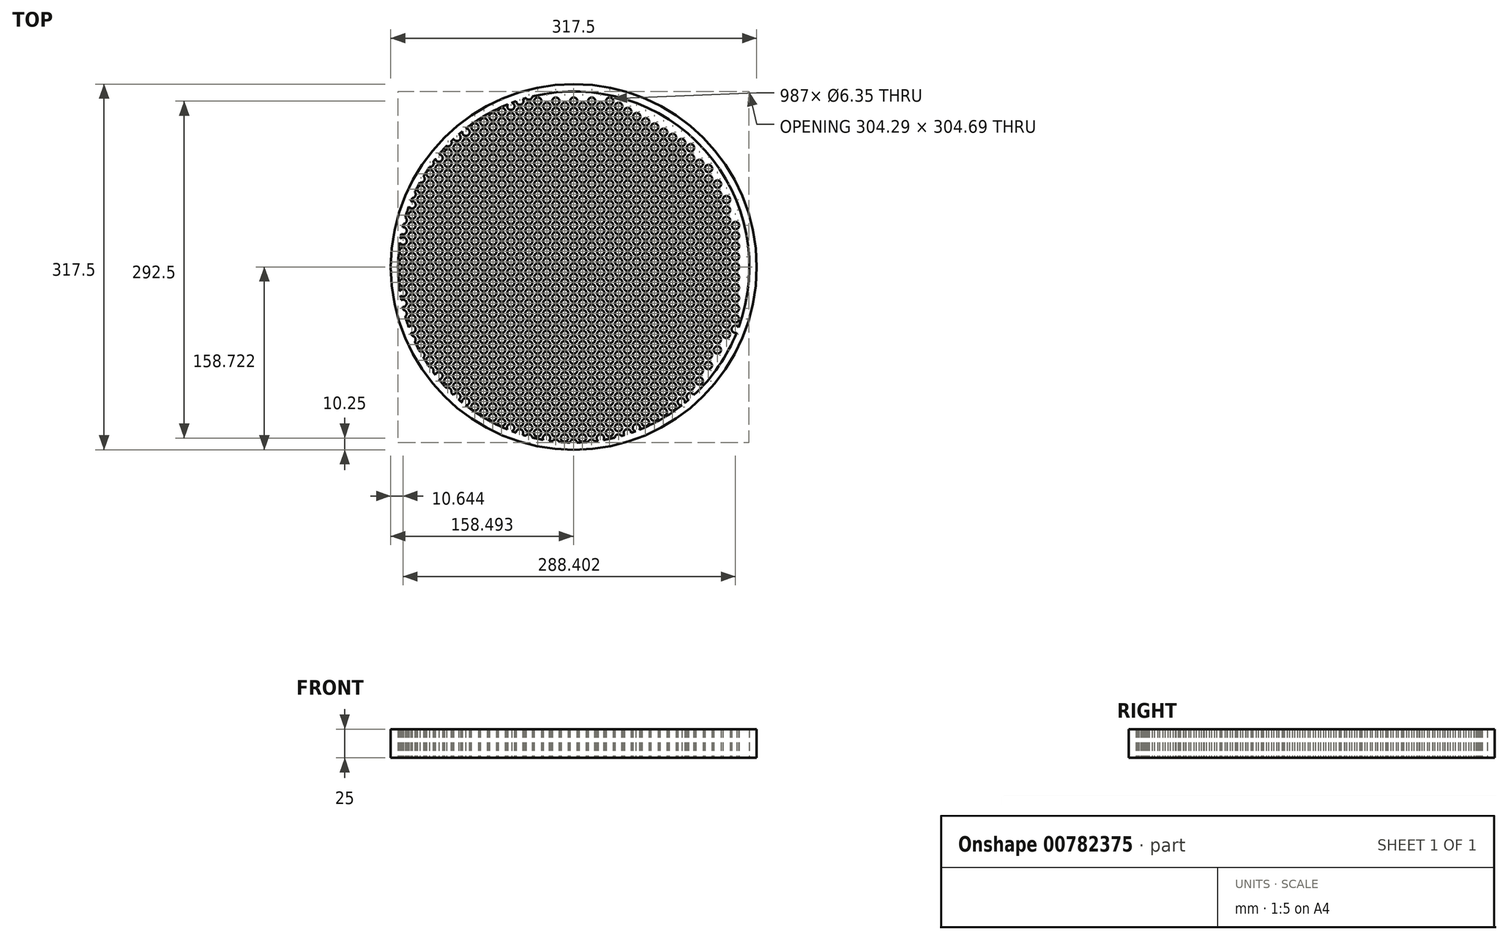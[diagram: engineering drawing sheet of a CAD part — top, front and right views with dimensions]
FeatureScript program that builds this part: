
annotation { "Feature Type Name" : "Feature", "Feature Type Description" : "" }
export const myFeature = defineFeature(function(context is Context, id is Id, definition is map)
    precondition{}
    {
        {
            var Q0;
            Q0=qCreatedBy(makeId("Top.planeOp"),FACE);
            var sketch = newSketch(context, id + "F0", { "sketchPlane" : qUnion([Q0])});
            skCircle(sketch, "E0", {"center": v(0, 0) * mm, "radius": 152.4 * mm});
            skCircle(sketch, "E1", {"center": v(0, 0) * mm, "radius": 3.18 * mm});
            skCircle(sketch, "E2", {"center": v(0, 9) * mm, "radius": 3.18 * mm});
            skCircle(sketch, "E3", {"center": v(7.8, 4.5) * mm, "radius": 3.18 * mm});
            skCircle(sketch, "E4", {"center": v(7.8, -4.5) * mm, "radius": 3.18 * mm});
            skCircle(sketch, "E5.0.1.0", {"center": v(7.8, 22.5) * mm, "radius": 3.18 * mm});
            skCircle(sketch, "E5.0.1.1", {"center": v(7.8, 13.5) * mm, "radius": 3.18 * mm});
            skCircle(sketch, "E5.0.1.2", {"center": v(0, 18) * mm, "radius": 3.18 * mm});
            skCircle(sketch, "E5.0.1.3", {"center": v(0, 27) * mm, "radius": 3.18 * mm});
            skCircle(sketch, "E5.0.2.0", {"center": v(7.8, 40.5) * mm, "radius": 3.18 * mm});
            skCircle(sketch, "E5.0.2.1", {"center": v(7.8, 31.5) * mm, "radius": 3.18 * mm});
            skCircle(sketch, "E5.0.2.2", {"center": v(0, 36) * mm, "radius": 3.18 * mm});
            skCircle(sketch, "E5.0.2.3", {"center": v(0, 45) * mm, "radius": 3.18 * mm});
            skCircle(sketch, "E5.0.3.0", {"center": v(7.8, 58.5) * mm, "radius": 3.18 * mm});
            skCircle(sketch, "E5.0.3.1", {"center": v(7.8, 49.5) * mm, "radius": 3.18 * mm});
            skCircle(sketch, "E5.0.3.2", {"center": v(0, 54) * mm, "radius": 3.18 * mm});
            skCircle(sketch, "E5.0.3.3", {"center": v(0, 63) * mm, "radius": 3.18 * mm});
            skCircle(sketch, "E5.0.4.0", {"center": v(7.8, 76.5) * mm, "radius": 3.18 * mm});
            skCircle(sketch, "E5.0.4.1", {"center": v(7.8, 67.5) * mm, "radius": 3.18 * mm});
            skCircle(sketch, "E5.0.4.2", {"center": v(0, 72) * mm, "radius": 3.18 * mm});
            skCircle(sketch, "E5.0.4.3", {"center": v(0, 81) * mm, "radius": 3.18 * mm});
            skCircle(sketch, "E5.0.5.0", {"center": v(7.8, 94.5) * mm, "radius": 3.18 * mm});
            skCircle(sketch, "E5.0.5.1", {"center": v(7.8, 85.5) * mm, "radius": 3.18 * mm});
            skCircle(sketch, "E5.0.5.2", {"center": v(0, 90) * mm, "radius": 3.18 * mm});
            skCircle(sketch, "E5.0.5.3", {"center": v(0, 99) * mm, "radius": 3.18 * mm});
            skCircle(sketch, "E5.0.6.0", {"center": v(7.8, 112.5) * mm, "radius": 3.18 * mm});
            skCircle(sketch, "E5.0.6.1", {"center": v(7.8, 103.5) * mm, "radius": 3.18 * mm});
            skCircle(sketch, "E5.0.6.2", {"center": v(0, 108) * mm, "radius": 3.18 * mm});
            skCircle(sketch, "E5.0.6.3", {"center": v(0, 117) * mm, "radius": 3.18 * mm});
            skCircle(sketch, "E5.0.7.0", {"center": v(7.8, 130.5) * mm, "radius": 3.18 * mm});
            skCircle(sketch, "E5.0.7.1", {"center": v(7.8, 121.5) * mm, "radius": 3.18 * mm});
            skCircle(sketch, "E5.0.7.2", {"center": v(0, 126) * mm, "radius": 3.18 * mm});
            skCircle(sketch, "E5.0.7.3", {"center": v(0, 135) * mm, "radius": 3.18 * mm});
            skCircle(sketch, "E5.0.8.1", {"center": v(7.8, 139.5) * mm, "radius": 3.18 * mm});
            skCircle(sketch, "E5.0.8.2", {"center": v(0, 144) * mm, "radius": 3.18 * mm});
            skCircle(sketch, "E5.1.0.0", {"center": v(23.38, 4.5) * mm, "radius": 3.18 * mm});
            skCircle(sketch, "E5.1.0.1", {"center": v(23.38, -4.5) * mm, "radius": 3.18 * mm});
            skCircle(sketch, "E5.1.0.2", {"center": v(15.59, 0) * mm, "radius": 3.18 * mm});
            skCircle(sketch, "E5.1.0.3", {"center": v(15.59, 9) * mm, "radius": 3.18 * mm});
            skCircle(sketch, "E5.1.1.0", {"center": v(23.38, 22.5) * mm, "radius": 3.18 * mm});
            skCircle(sketch, "E5.1.1.1", {"center": v(23.38, 13.5) * mm, "radius": 3.18 * mm});
            skCircle(sketch, "E5.1.1.2", {"center": v(15.59, 18) * mm, "radius": 3.18 * mm});
            skCircle(sketch, "E5.1.1.3", {"center": v(15.59, 27) * mm, "radius": 3.18 * mm});
            skCircle(sketch, "E5.1.2.0", {"center": v(23.38, 40.5) * mm, "radius": 3.18 * mm});
            skCircle(sketch, "E5.1.2.1", {"center": v(23.38, 31.5) * mm, "radius": 3.18 * mm});
            skCircle(sketch, "E5.1.2.2", {"center": v(15.59, 36) * mm, "radius": 3.18 * mm});
            skCircle(sketch, "E5.1.2.3", {"center": v(15.59, 45) * mm, "radius": 3.18 * mm});
            skCircle(sketch, "E5.1.3.0", {"center": v(23.38, 58.5) * mm, "radius": 3.18 * mm});
            skCircle(sketch, "E5.1.3.1", {"center": v(23.38, 49.5) * mm, "radius": 3.18 * mm});
            skCircle(sketch, "E5.1.3.2", {"center": v(15.59, 54) * mm, "radius": 3.18 * mm});
            skCircle(sketch, "E5.1.3.3", {"center": v(15.59, 63) * mm, "radius": 3.18 * mm});
            skCircle(sketch, "E5.1.4.0", {"center": v(23.38, 76.5) * mm, "radius": 3.18 * mm});
            skCircle(sketch, "E5.1.4.1", {"center": v(23.38, 67.5) * mm, "radius": 3.18 * mm});
            skCircle(sketch, "E5.1.4.2", {"center": v(15.59, 72) * mm, "radius": 3.18 * mm});
            skCircle(sketch, "E5.1.4.3", {"center": v(15.59, 81) * mm, "radius": 3.18 * mm});
            skCircle(sketch, "E5.1.5.0", {"center": v(23.38, 94.5) * mm, "radius": 3.18 * mm});
            skCircle(sketch, "E5.1.5.1", {"center": v(23.38, 85.5) * mm, "radius": 3.18 * mm});
            skCircle(sketch, "E5.1.5.2", {"center": v(15.59, 90) * mm, "radius": 3.18 * mm});
            skCircle(sketch, "E5.1.5.3", {"center": v(15.59, 99) * mm, "radius": 3.18 * mm});
            skCircle(sketch, "E5.1.6.0", {"center": v(23.38, 112.5) * mm, "radius": 3.18 * mm});
            skCircle(sketch, "E5.1.6.1", {"center": v(23.38, 103.5) * mm, "radius": 3.18 * mm});
            skCircle(sketch, "E5.1.6.2", {"center": v(15.59, 108) * mm, "radius": 3.18 * mm});
            skCircle(sketch, "E5.1.6.3", {"center": v(15.59, 117) * mm, "radius": 3.18 * mm});
            skCircle(sketch, "E5.1.7.0", {"center": v(23.38, 130.5) * mm, "radius": 3.18 * mm});
            skCircle(sketch, "E5.1.7.1", {"center": v(23.38, 121.5) * mm, "radius": 3.18 * mm});
            skCircle(sketch, "E5.1.7.2", {"center": v(15.59, 126) * mm, "radius": 3.18 * mm});
            skCircle(sketch, "E5.1.7.3", {"center": v(15.59, 135) * mm, "radius": 3.18 * mm});
            skCircle(sketch, "E5.1.8.1", {"center": v(23.38, 139.5) * mm, "radius": 3.18 * mm});
            skCircle(sketch, "E5.1.8.2", {"center": v(15.59, 144) * mm, "radius": 3.18 * mm});
            skCircle(sketch, "E5.2.0.0", {"center": v(38.97, 4.5) * mm, "radius": 3.18 * mm});
            skCircle(sketch, "E5.2.0.1", {"center": v(38.97, -4.5) * mm, "radius": 3.18 * mm});
            skCircle(sketch, "E5.2.0.2", {"center": v(31.18, 0) * mm, "radius": 3.18 * mm});
            skCircle(sketch, "E5.2.0.3", {"center": v(31.18, 9) * mm, "radius": 3.18 * mm});
            skCircle(sketch, "E5.2.1.0", {"center": v(38.97, 22.5) * mm, "radius": 3.18 * mm});
            skCircle(sketch, "E5.2.1.1", {"center": v(38.97, 13.5) * mm, "radius": 3.18 * mm});
            skCircle(sketch, "E5.2.1.2", {"center": v(31.18, 18) * mm, "radius": 3.18 * mm});
            skCircle(sketch, "E5.2.1.3", {"center": v(31.18, 27) * mm, "radius": 3.18 * mm});
            skCircle(sketch, "E5.2.2.0", {"center": v(38.97, 40.5) * mm, "radius": 3.18 * mm});
            skCircle(sketch, "E5.2.2.1", {"center": v(38.97, 31.5) * mm, "radius": 3.18 * mm});
            skCircle(sketch, "E5.2.2.2", {"center": v(31.18, 36) * mm, "radius": 3.18 * mm});
            skCircle(sketch, "E5.2.2.3", {"center": v(31.18, 45) * mm, "radius": 3.18 * mm});
            skCircle(sketch, "E5.2.3.0", {"center": v(38.97, 58.5) * mm, "radius": 3.18 * mm});
            skCircle(sketch, "E5.2.3.1", {"center": v(38.97, 49.5) * mm, "radius": 3.18 * mm});
            skCircle(sketch, "E5.2.3.2", {"center": v(31.18, 54) * mm, "radius": 3.18 * mm});
            skCircle(sketch, "E5.2.3.3", {"center": v(31.18, 63) * mm, "radius": 3.18 * mm});
            skCircle(sketch, "E5.2.4.0", {"center": v(38.97, 76.5) * mm, "radius": 3.18 * mm});
            skCircle(sketch, "E5.2.4.1", {"center": v(38.97, 67.5) * mm, "radius": 3.18 * mm});
            skCircle(sketch, "E5.2.4.2", {"center": v(31.18, 72) * mm, "radius": 3.18 * mm});
            skCircle(sketch, "E5.2.4.3", {"center": v(31.18, 81) * mm, "radius": 3.18 * mm});
            skCircle(sketch, "E5.2.5.0", {"center": v(38.97, 94.5) * mm, "radius": 3.18 * mm});
            skCircle(sketch, "E5.2.5.1", {"center": v(38.97, 85.5) * mm, "radius": 3.18 * mm});
            skCircle(sketch, "E5.2.5.2", {"center": v(31.18, 90) * mm, "radius": 3.18 * mm});
            skCircle(sketch, "E5.2.5.3", {"center": v(31.18, 99) * mm, "radius": 3.18 * mm});
            skCircle(sketch, "E5.2.6.0", {"center": v(38.97, 112.5) * mm, "radius": 3.18 * mm});
            skCircle(sketch, "E5.2.6.1", {"center": v(38.97, 103.5) * mm, "radius": 3.18 * mm});
            skCircle(sketch, "E5.2.6.2", {"center": v(31.18, 108) * mm, "radius": 3.18 * mm});
            skCircle(sketch, "E5.2.6.3", {"center": v(31.18, 117) * mm, "radius": 3.18 * mm});
            skCircle(sketch, "E5.2.7.0", {"center": v(38.97, 130.5) * mm, "radius": 3.18 * mm});
            skCircle(sketch, "E5.2.7.1", {"center": v(38.97, 121.5) * mm, "radius": 3.18 * mm});
            skCircle(sketch, "E5.2.7.2", {"center": v(31.18, 126) * mm, "radius": 3.18 * mm});
            skCircle(sketch, "E5.2.7.3", {"center": v(31.18, 135) * mm, "radius": 3.18 * mm});
            skCircle(sketch, "E5.2.8.1", {"center": v(38.97, 139.5) * mm, "radius": 3.18 * mm});
            skCircle(sketch, "E5.2.8.2", {"center": v(31.18, 144) * mm, "radius": 3.18 * mm});
            skCircle(sketch, "E5.3.0.0", {"center": v(54.56, 4.5) * mm, "radius": 3.18 * mm});
            skCircle(sketch, "E5.3.0.1", {"center": v(54.56, -4.5) * mm, "radius": 3.18 * mm});
            skCircle(sketch, "E5.3.0.2", {"center": v(46.77, 0) * mm, "radius": 3.18 * mm});
            skCircle(sketch, "E5.3.0.3", {"center": v(46.77, 9) * mm, "radius": 3.18 * mm});
            skCircle(sketch, "E5.3.1.0", {"center": v(54.56, 22.5) * mm, "radius": 3.18 * mm});
            skCircle(sketch, "E5.3.1.1", {"center": v(54.56, 13.5) * mm, "radius": 3.18 * mm});
            skCircle(sketch, "E5.3.1.2", {"center": v(46.77, 18) * mm, "radius": 3.18 * mm});
            skCircle(sketch, "E5.3.1.3", {"center": v(46.77, 27) * mm, "radius": 3.18 * mm});
            skCircle(sketch, "E5.3.2.0", {"center": v(54.56, 40.5) * mm, "radius": 3.18 * mm});
            skCircle(sketch, "E5.3.2.1", {"center": v(54.56, 31.5) * mm, "radius": 3.18 * mm});
            skCircle(sketch, "E5.3.2.2", {"center": v(46.77, 36) * mm, "radius": 3.18 * mm});
            skCircle(sketch, "E5.3.2.3", {"center": v(46.77, 45) * mm, "radius": 3.18 * mm});
            skCircle(sketch, "E5.3.3.0", {"center": v(54.56, 58.5) * mm, "radius": 3.18 * mm});
            skCircle(sketch, "E5.3.3.1", {"center": v(54.56, 49.5) * mm, "radius": 3.18 * mm});
            skCircle(sketch, "E5.3.3.2", {"center": v(46.77, 54) * mm, "radius": 3.18 * mm});
            skCircle(sketch, "E5.3.3.3", {"center": v(46.77, 63) * mm, "radius": 3.18 * mm});
            skCircle(sketch, "E5.3.4.0", {"center": v(54.56, 76.5) * mm, "radius": 3.18 * mm});
            skCircle(sketch, "E5.3.4.1", {"center": v(54.56, 67.5) * mm, "radius": 3.18 * mm});
            skCircle(sketch, "E5.3.4.2", {"center": v(46.77, 72) * mm, "radius": 3.18 * mm});
            skCircle(sketch, "E5.3.4.3", {"center": v(46.77, 81) * mm, "radius": 3.18 * mm});
            skCircle(sketch, "E5.3.5.0", {"center": v(54.56, 94.5) * mm, "radius": 3.18 * mm});
            skCircle(sketch, "E5.3.5.1", {"center": v(54.56, 85.5) * mm, "radius": 3.18 * mm});
            skCircle(sketch, "E5.3.5.2", {"center": v(46.77, 90) * mm, "radius": 3.18 * mm});
            skCircle(sketch, "E5.3.5.3", {"center": v(46.77, 99) * mm, "radius": 3.18 * mm});
            skCircle(sketch, "E5.3.6.0", {"center": v(54.56, 112.5) * mm, "radius": 3.18 * mm});
            skCircle(sketch, "E5.3.6.1", {"center": v(54.56, 103.5) * mm, "radius": 3.18 * mm});
            skCircle(sketch, "E5.3.6.2", {"center": v(46.77, 108) * mm, "radius": 3.18 * mm});
            skCircle(sketch, "E5.3.6.3", {"center": v(46.77, 117) * mm, "radius": 3.18 * mm});
            skCircle(sketch, "E5.3.7.0", {"center": v(54.56, 130.5) * mm, "radius": 3.18 * mm});
            skCircle(sketch, "E5.3.7.1", {"center": v(54.56, 121.5) * mm, "radius": 3.18 * mm});
            skCircle(sketch, "E5.3.7.2", {"center": v(46.77, 126) * mm, "radius": 3.18 * mm});
            skCircle(sketch, "E5.3.7.3", {"center": v(46.77, 135) * mm, "radius": 3.18 * mm});
            skCircle(sketch, "E5.4.0.0", {"center": v(70.15, 4.5) * mm, "radius": 3.18 * mm});
            skCircle(sketch, "E5.4.0.1", {"center": v(70.15, -4.5) * mm, "radius": 3.18 * mm});
            skCircle(sketch, "E5.4.0.2", {"center": v(62.35, 0) * mm, "radius": 3.18 * mm});
            skCircle(sketch, "E5.4.0.3", {"center": v(62.35, 9) * mm, "radius": 3.18 * mm});
            skCircle(sketch, "E5.4.1.0", {"center": v(70.15, 22.5) * mm, "radius": 3.18 * mm});
            skCircle(sketch, "E5.4.1.1", {"center": v(70.15, 13.5) * mm, "radius": 3.18 * mm});
            skCircle(sketch, "E5.4.1.2", {"center": v(62.35, 18) * mm, "radius": 3.18 * mm});
            skCircle(sketch, "E5.4.1.3", {"center": v(62.35, 27) * mm, "radius": 3.18 * mm});
            skCircle(sketch, "E5.4.2.0", {"center": v(70.15, 40.5) * mm, "radius": 3.18 * mm});
            skCircle(sketch, "E5.4.2.1", {"center": v(70.15, 31.5) * mm, "radius": 3.18 * mm});
            skCircle(sketch, "E5.4.2.2", {"center": v(62.35, 36) * mm, "radius": 3.18 * mm});
            skCircle(sketch, "E5.4.2.3", {"center": v(62.35, 45) * mm, "radius": 3.18 * mm});
            skCircle(sketch, "E5.4.3.0", {"center": v(70.15, 58.5) * mm, "radius": 3.18 * mm});
            skCircle(sketch, "E5.4.3.1", {"center": v(70.15, 49.5) * mm, "radius": 3.18 * mm});
            skCircle(sketch, "E5.4.3.2", {"center": v(62.35, 54) * mm, "radius": 3.18 * mm});
            skCircle(sketch, "E5.4.3.3", {"center": v(62.35, 63) * mm, "radius": 3.18 * mm});
            skCircle(sketch, "E5.4.4.0", {"center": v(70.15, 76.5) * mm, "radius": 3.18 * mm});
            skCircle(sketch, "E5.4.4.1", {"center": v(70.15, 67.5) * mm, "radius": 3.18 * mm});
            skCircle(sketch, "E5.4.4.2", {"center": v(62.35, 72) * mm, "radius": 3.18 * mm});
            skCircle(sketch, "E5.4.4.3", {"center": v(62.35, 81) * mm, "radius": 3.18 * mm});
            skCircle(sketch, "E5.4.5.0", {"center": v(70.15, 94.5) * mm, "radius": 3.18 * mm});
            skCircle(sketch, "E5.4.5.1", {"center": v(70.15, 85.5) * mm, "radius": 3.18 * mm});
            skCircle(sketch, "E5.4.5.2", {"center": v(62.35, 90) * mm, "radius": 3.18 * mm});
            skCircle(sketch, "E5.4.5.3", {"center": v(62.35, 99) * mm, "radius": 3.18 * mm});
            skCircle(sketch, "E5.4.6.0", {"center": v(70.15, 112.5) * mm, "radius": 3.18 * mm});
            skCircle(sketch, "E5.4.6.1", {"center": v(70.15, 103.5) * mm, "radius": 3.18 * mm});
            skCircle(sketch, "E5.4.6.2", {"center": v(62.35, 108) * mm, "radius": 3.18 * mm});
            skCircle(sketch, "E5.4.6.3", {"center": v(62.35, 117) * mm, "radius": 3.18 * mm});
            skCircle(sketch, "E5.4.7.1", {"center": v(70.15, 121.5) * mm, "radius": 3.18 * mm});
            skCircle(sketch, "E5.4.7.2", {"center": v(62.35, 126) * mm, "radius": 3.18 * mm});
            skCircle(sketch, "E5.5.0.0", {"center": v(85.74, 4.5) * mm, "radius": 3.18 * mm});
            skCircle(sketch, "E5.5.0.1", {"center": v(85.74, -4.5) * mm, "radius": 3.18 * mm});
            skCircle(sketch, "E5.5.0.2", {"center": v(77.94, 0) * mm, "radius": 3.18 * mm});
            skCircle(sketch, "E5.5.0.3", {"center": v(77.94, 9) * mm, "radius": 3.18 * mm});
            skCircle(sketch, "E5.5.1.0", {"center": v(85.74, 22.5) * mm, "radius": 3.18 * mm});
            skCircle(sketch, "E5.5.1.1", {"center": v(85.74, 13.5) * mm, "radius": 3.18 * mm});
            skCircle(sketch, "E5.5.1.2", {"center": v(77.94, 18) * mm, "radius": 3.18 * mm});
            skCircle(sketch, "E5.5.1.3", {"center": v(77.94, 27) * mm, "radius": 3.18 * mm});
            skCircle(sketch, "E5.5.2.0", {"center": v(85.74, 40.5) * mm, "radius": 3.18 * mm});
            skCircle(sketch, "E5.5.2.1", {"center": v(85.74, 31.5) * mm, "radius": 3.18 * mm});
            skCircle(sketch, "E5.5.2.2", {"center": v(77.94, 36) * mm, "radius": 3.18 * mm});
            skCircle(sketch, "E5.5.2.3", {"center": v(77.94, 45) * mm, "radius": 3.18 * mm});
            skCircle(sketch, "E5.5.3.0", {"center": v(85.74, 58.5) * mm, "radius": 3.18 * mm});
            skCircle(sketch, "E5.5.3.1", {"center": v(85.74, 49.5) * mm, "radius": 3.18 * mm});
            skCircle(sketch, "E5.5.3.2", {"center": v(77.94, 54) * mm, "radius": 3.18 * mm});
            skCircle(sketch, "E5.5.3.3", {"center": v(77.94, 63) * mm, "radius": 3.18 * mm});
            skCircle(sketch, "E5.5.4.0", {"center": v(85.74, 76.5) * mm, "radius": 3.18 * mm});
            skCircle(sketch, "E5.5.4.1", {"center": v(85.74, 67.5) * mm, "radius": 3.18 * mm});
            skCircle(sketch, "E5.5.4.2", {"center": v(77.94, 72) * mm, "radius": 3.18 * mm});
            skCircle(sketch, "E5.5.4.3", {"center": v(77.94, 81) * mm, "radius": 3.18 * mm});
            skCircle(sketch, "E5.5.5.0", {"center": v(85.74, 94.5) * mm, "radius": 3.18 * mm});
            skCircle(sketch, "E5.5.5.1", {"center": v(85.74, 85.5) * mm, "radius": 3.18 * mm});
            skCircle(sketch, "E5.5.5.2", {"center": v(77.94, 90) * mm, "radius": 3.18 * mm});
            skCircle(sketch, "E5.5.5.3", {"center": v(77.94, 99) * mm, "radius": 3.18 * mm});
            skCircle(sketch, "E5.5.6.0", {"center": v(85.74, 112.5) * mm, "radius": 3.18 * mm});
            skCircle(sketch, "E5.5.6.1", {"center": v(85.74, 103.5) * mm, "radius": 3.18 * mm});
            skCircle(sketch, "E5.5.6.2", {"center": v(77.94, 108) * mm, "radius": 3.18 * mm});
            skCircle(sketch, "E5.5.6.3", {"center": v(77.94, 117) * mm, "radius": 3.18 * mm});
            skCircle(sketch, "E5.6.0.0", {"center": v(101.32, 4.5) * mm, "radius": 3.18 * mm});
            skCircle(sketch, "E5.6.0.1", {"center": v(101.32, -4.5) * mm, "radius": 3.18 * mm});
            skCircle(sketch, "E5.6.0.2", {"center": v(93.53, 0) * mm, "radius": 3.18 * mm});
            skCircle(sketch, "E5.6.0.3", {"center": v(93.53, 9) * mm, "radius": 3.18 * mm});
            skCircle(sketch, "E5.6.1.0", {"center": v(101.32, 22.5) * mm, "radius": 3.18 * mm});
            skCircle(sketch, "E5.6.1.1", {"center": v(101.32, 13.5) * mm, "radius": 3.18 * mm});
            skCircle(sketch, "E5.6.1.2", {"center": v(93.53, 18) * mm, "radius": 3.18 * mm});
            skCircle(sketch, "E5.6.1.3", {"center": v(93.53, 27) * mm, "radius": 3.18 * mm});
            skCircle(sketch, "E5.6.2.0", {"center": v(101.32, 40.5) * mm, "radius": 3.18 * mm});
            skCircle(sketch, "E5.6.2.1", {"center": v(101.32, 31.5) * mm, "radius": 3.18 * mm});
            skCircle(sketch, "E5.6.2.2", {"center": v(93.53, 36) * mm, "radius": 3.18 * mm});
            skCircle(sketch, "E5.6.2.3", {"center": v(93.53, 45) * mm, "radius": 3.18 * mm});
            skCircle(sketch, "E5.6.3.0", {"center": v(101.32, 58.5) * mm, "radius": 3.18 * mm});
            skCircle(sketch, "E5.6.3.1", {"center": v(101.32, 49.5) * mm, "radius": 3.18 * mm});
            skCircle(sketch, "E5.6.3.2", {"center": v(93.53, 54) * mm, "radius": 3.18 * mm});
            skCircle(sketch, "E5.6.3.3", {"center": v(93.53, 63) * mm, "radius": 3.18 * mm});
            skCircle(sketch, "E5.6.4.0", {"center": v(101.32, 76.5) * mm, "radius": 3.18 * mm});
            skCircle(sketch, "E5.6.4.1", {"center": v(101.32, 67.5) * mm, "radius": 3.18 * mm});
            skCircle(sketch, "E5.6.4.2", {"center": v(93.53, 72) * mm, "radius": 3.18 * mm});
            skCircle(sketch, "E5.6.4.3", {"center": v(93.53, 81) * mm, "radius": 3.18 * mm});
            skCircle(sketch, "E5.6.5.0", {"center": v(101.32, 94.5) * mm, "radius": 3.18 * mm});
            skCircle(sketch, "E5.6.5.1", {"center": v(101.32, 85.5) * mm, "radius": 3.18 * mm});
            skCircle(sketch, "E5.6.5.2", {"center": v(93.53, 90) * mm, "radius": 3.18 * mm});
            skCircle(sketch, "E5.6.5.3", {"center": v(93.53, 99) * mm, "radius": 3.18 * mm});
            skCircle(sketch, "E5.6.6.1", {"center": v(101.32, 103.5) * mm, "radius": 3.18 * mm});
            skCircle(sketch, "E5.6.6.2", {"center": v(93.53, 108) * mm, "radius": 3.18 * mm});
            skCircle(sketch, "E5.7.0.0", {"center": v(116.91, 4.5) * mm, "radius": 3.18 * mm});
            skCircle(sketch, "E5.7.0.1", {"center": v(116.91, -4.5) * mm, "radius": 3.18 * mm});
            skCircle(sketch, "E5.7.0.2", {"center": v(109.12, 0) * mm, "radius": 3.18 * mm});
            skCircle(sketch, "E5.7.0.3", {"center": v(109.12, 9) * mm, "radius": 3.18 * mm});
            skCircle(sketch, "E5.7.1.0", {"center": v(116.91, 22.5) * mm, "radius": 3.18 * mm});
            skCircle(sketch, "E5.7.1.1", {"center": v(116.91, 13.5) * mm, "radius": 3.18 * mm});
            skCircle(sketch, "E5.7.1.2", {"center": v(109.12, 18) * mm, "radius": 3.18 * mm});
            skCircle(sketch, "E5.7.1.3", {"center": v(109.12, 27) * mm, "radius": 3.18 * mm});
            skCircle(sketch, "E5.7.2.0", {"center": v(116.91, 40.5) * mm, "radius": 3.18 * mm});
            skCircle(sketch, "E5.7.2.1", {"center": v(116.91, 31.5) * mm, "radius": 3.18 * mm});
            skCircle(sketch, "E5.7.2.2", {"center": v(109.12, 36) * mm, "radius": 3.18 * mm});
            skCircle(sketch, "E5.7.2.3", {"center": v(109.12, 45) * mm, "radius": 3.18 * mm});
            skCircle(sketch, "E5.7.3.0", {"center": v(116.91, 58.5) * mm, "radius": 3.18 * mm});
            skCircle(sketch, "E5.7.3.1", {"center": v(116.91, 49.5) * mm, "radius": 3.18 * mm});
            skCircle(sketch, "E5.7.3.2", {"center": v(109.12, 54) * mm, "radius": 3.18 * mm});
            skCircle(sketch, "E5.7.3.3", {"center": v(109.12, 63) * mm, "radius": 3.18 * mm});
            skCircle(sketch, "E5.7.4.0", {"center": v(116.91, 76.5) * mm, "radius": 3.18 * mm});
            skCircle(sketch, "E5.7.4.1", {"center": v(116.91, 67.5) * mm, "radius": 3.18 * mm});
            skCircle(sketch, "E5.7.4.2", {"center": v(109.12, 72) * mm, "radius": 3.18 * mm});
            skCircle(sketch, "E5.7.4.3", {"center": v(109.12, 81) * mm, "radius": 3.18 * mm});
            skCircle(sketch, "E5.7.5.1", {"center": v(116.91, 85.5) * mm, "radius": 3.18 * mm});
            skCircle(sketch, "E5.7.5.2", {"center": v(109.12, 90) * mm, "radius": 3.18 * mm});
            skCircle(sketch, "E5.8.0.0", {"center": v(132.5, 4.5) * mm, "radius": 3.18 * mm});
            skCircle(sketch, "E5.8.0.1", {"center": v(132.5, -4.5) * mm, "radius": 3.18 * mm});
            skCircle(sketch, "E5.8.0.2", {"center": v(124.7, 0) * mm, "radius": 3.18 * mm});
            skCircle(sketch, "E5.8.0.3", {"center": v(124.7, 9) * mm, "radius": 3.18 * mm});
            skCircle(sketch, "E5.8.1.0", {"center": v(132.5, 22.5) * mm, "radius": 3.18 * mm});
            skCircle(sketch, "E5.8.1.1", {"center": v(132.5, 13.5) * mm, "radius": 3.18 * mm});
            skCircle(sketch, "E5.8.1.2", {"center": v(124.7, 18) * mm, "radius": 3.18 * mm});
            skCircle(sketch, "E5.8.1.3", {"center": v(124.7, 27) * mm, "radius": 3.18 * mm});
            skCircle(sketch, "E5.8.2.0", {"center": v(132.5, 40.5) * mm, "radius": 3.18 * mm});
            skCircle(sketch, "E5.8.2.1", {"center": v(132.5, 31.5) * mm, "radius": 3.18 * mm});
            skCircle(sketch, "E5.8.2.2", {"center": v(124.7, 36) * mm, "radius": 3.18 * mm});
            skCircle(sketch, "E5.8.2.3", {"center": v(124.7, 45) * mm, "radius": 3.18 * mm});
            skCircle(sketch, "E5.8.3.0", {"center": v(132.5, 58.5) * mm, "radius": 3.18 * mm});
            skCircle(sketch, "E5.8.3.1", {"center": v(132.5, 49.5) * mm, "radius": 3.18 * mm});
            skCircle(sketch, "E5.8.3.2", {"center": v(124.7, 54) * mm, "radius": 3.18 * mm});
            skCircle(sketch, "E5.8.3.3", {"center": v(124.7, 63) * mm, "radius": 3.18 * mm});
            skCircle(sketch, "E5.8.4.2", {"center": v(124.7, 72) * mm, "radius": 3.18 * mm});
            skCircle(sketch, "E5.9.0.2", {"center": v(140.3, 0) * mm, "radius": 3.18 * mm});
            skCircle(sketch, "E5.9.0.3", {"center": v(140.3, 9) * mm, "radius": 3.18 * mm});
            skCircle(sketch, "E5.9.1.2", {"center": v(140.3, 18) * mm, "radius": 3.18 * mm});
            skCircle(sketch, "E5.9.1.3", {"center": v(140.3, 27) * mm, "radius": 3.18 * mm});
            skCircle(sketch, "E5.9.2.2", {"center": v(140.3, 36) * mm, "radius": 3.18 * mm});
            skLineSegment(sketch, "E5.direction1", {"start": v(0, 0) * mm, "end": v(15.59, 0) * mm, "construction": true});
            skLineSegment(sketch, "E5.direction2", {"start": v(0, 0) * mm, "end": v(0, 18) * mm, "construction": true});
            skCircle(sketch, "E6.1.0.0", {"center": v(-7.8, 76.5) * mm, "radius": 3.18 * mm});
            skCircle(sketch, "E6.1.0.2", {"center": v(-15.59, 135) * mm, "radius": 3.18 * mm});
            skCircle(sketch, "E6.1.0.3", {"center": v(-15.59, 63) * mm, "radius": 3.18 * mm});
            skCircle(sketch, "E6.1.0.4", {"center": v(-7.8, 139.5) * mm, "radius": 3.18 * mm});
            skCircle(sketch, "E6.1.0.5", {"center": v(-7.8, 67.5) * mm, "radius": 3.18 * mm});
            skCircle(sketch, "E6.1.0.6", {"center": v(-15.59, 144) * mm, "radius": 3.18 * mm});
            skCircle(sketch, "E6.1.0.7", {"center": v(-15.59, 72) * mm, "radius": 3.18 * mm});
            skCircle(sketch, "E6.1.0.8", {"center": v(-15.59, 81) * mm, "radius": 3.18 * mm});
            skCircle(sketch, "E6.1.0.10", {"center": v(-7.8, 94.5) * mm, "radius": 3.18 * mm});
            skCircle(sketch, "E6.1.0.12", {"center": v(-7.8, 85.5) * mm, "radius": 3.18 * mm});
            skCircle(sketch, "E6.1.0.14", {"center": v(-15.59, 90) * mm, "radius": 3.18 * mm});
            skCircle(sketch, "E6.1.0.16", {"center": v(-15.59, 99) * mm, "radius": 3.18 * mm});
            skCircle(sketch, "E6.1.0.18", {"center": v(-7.8, 130.5) * mm, "radius": 3.18 * mm});
            skCircle(sketch, "E6.1.0.19", {"center": v(-7.8, 112.5) * mm, "radius": 3.18 * mm});
            skCircle(sketch, "E6.1.0.20", {"center": v(-15.59, 108) * mm, "radius": 3.18 * mm});
            skCircle(sketch, "E6.1.0.21", {"center": v(-7.8, 103.5) * mm, "radius": 3.18 * mm});
            skCircle(sketch, "E6.1.0.22", {"center": v(-15.59, 117) * mm, "radius": 3.18 * mm});
            skCircle(sketch, "E6.1.0.23", {"center": v(-7.8, 58.5) * mm, "radius": 3.18 * mm});
            skCircle(sketch, "E6.1.0.24", {"center": v(-15.59, 36) * mm, "radius": 3.18 * mm});
            skCircle(sketch, "E6.1.0.25", {"center": v(-15.59, 45) * mm, "radius": 3.18 * mm});
            skLineSegment(sketch, "E6.1.0.26", {"start": v(-15.59, 0) * mm, "end": v(-15.59, 18) * mm, "construction": true});
            skCircle(sketch, "E6.1.0.27", {"center": v(-15.59, 9) * mm, "radius": 3.18 * mm});
            skCircle(sketch, "E6.1.0.28", {"center": v(-7.8, 4.5) * mm, "radius": 3.18 * mm});
            skCircle(sketch, "E6.1.0.29", {"center": v(-7.8, -4.5) * mm, "radius": 3.18 * mm});
            skCircle(sketch, "E6.1.0.30", {"center": v(-7.8, 22.5) * mm, "radius": 3.18 * mm});
            skCircle(sketch, "E6.1.0.31", {"center": v(-7.8, 13.5) * mm, "radius": 3.18 * mm});
            skCircle(sketch, "E6.1.0.32", {"center": v(-15.59, 27) * mm, "radius": 3.18 * mm});
            skCircle(sketch, "E6.1.0.33", {"center": v(-7.8, 40.5) * mm, "radius": 3.18 * mm});
            skCircle(sketch, "E6.1.0.34", {"center": v(-7.8, 31.5) * mm, "radius": 3.18 * mm});
            skCircle(sketch, "E6.1.0.35", {"center": v(-7.8, 121.5) * mm, "radius": 3.18 * mm});
            skCircle(sketch, "E6.1.0.36", {"center": v(-7.8, 49.5) * mm, "radius": 3.18 * mm});
            skCircle(sketch, "E6.1.0.37", {"center": v(-15.59, 126) * mm, "radius": 3.18 * mm});
            skCircle(sketch, "E6.1.0.38", {"center": v(-15.59, 54) * mm, "radius": 3.18 * mm});
            skCircle(sketch, "E6.1.0.39", {"center": v(-15.59, 18) * mm, "radius": 3.18 * mm});
            skCircle(sketch, "E6.1.0.40", {"center": v(-15.59, 0) * mm, "radius": 3.18 * mm});
            skCircle(sketch, "E6.2.0.0", {"center": v(-23.38, 76.5) * mm, "radius": 3.18 * mm});
            skCircle(sketch, "E6.2.0.2", {"center": v(-31.18, 135) * mm, "radius": 3.18 * mm});
            skCircle(sketch, "E6.2.0.3", {"center": v(-31.18, 63) * mm, "radius": 3.18 * mm});
            skCircle(sketch, "E6.2.0.4", {"center": v(-23.38, 139.5) * mm, "radius": 3.18 * mm});
            skCircle(sketch, "E6.2.0.5", {"center": v(-23.38, 67.5) * mm, "radius": 3.18 * mm});
            skCircle(sketch, "E6.2.0.6", {"center": v(-31.18, 144) * mm, "radius": 3.18 * mm});
            skCircle(sketch, "E6.2.0.7", {"center": v(-31.18, 72) * mm, "radius": 3.18 * mm});
            skCircle(sketch, "E6.2.0.8", {"center": v(-31.18, 81) * mm, "radius": 3.18 * mm});
            skCircle(sketch, "E6.2.0.10", {"center": v(-23.38, 94.5) * mm, "radius": 3.18 * mm});
            skCircle(sketch, "E6.2.0.12", {"center": v(-23.38, 85.5) * mm, "radius": 3.18 * mm});
            skCircle(sketch, "E6.2.0.14", {"center": v(-31.18, 90) * mm, "radius": 3.18 * mm});
            skCircle(sketch, "E6.2.0.16", {"center": v(-31.18, 99) * mm, "radius": 3.18 * mm});
            skCircle(sketch, "E6.2.0.18", {"center": v(-23.38, 130.5) * mm, "radius": 3.18 * mm});
            skCircle(sketch, "E6.2.0.19", {"center": v(-23.38, 112.5) * mm, "radius": 3.18 * mm});
            skCircle(sketch, "E6.2.0.20", {"center": v(-31.18, 108) * mm, "radius": 3.18 * mm});
            skCircle(sketch, "E6.2.0.21", {"center": v(-23.38, 103.5) * mm, "radius": 3.18 * mm});
            skCircle(sketch, "E6.2.0.22", {"center": v(-31.18, 117) * mm, "radius": 3.18 * mm});
            skCircle(sketch, "E6.2.0.23", {"center": v(-23.38, 58.5) * mm, "radius": 3.18 * mm});
            skCircle(sketch, "E6.2.0.24", {"center": v(-31.18, 36) * mm, "radius": 3.18 * mm});
            skCircle(sketch, "E6.2.0.25", {"center": v(-31.18, 45) * mm, "radius": 3.18 * mm});
            skLineSegment(sketch, "E6.2.0.26", {"start": v(-31.18, 0) * mm, "end": v(-31.18, 18) * mm, "construction": true});
            skCircle(sketch, "E6.2.0.27", {"center": v(-31.18, 9) * mm, "radius": 3.18 * mm});
            skCircle(sketch, "E6.2.0.28", {"center": v(-23.38, 4.5) * mm, "radius": 3.18 * mm});
            skCircle(sketch, "E6.2.0.29", {"center": v(-23.38, -4.5) * mm, "radius": 3.18 * mm});
            skCircle(sketch, "E6.2.0.30", {"center": v(-23.38, 22.5) * mm, "radius": 3.18 * mm});
            skCircle(sketch, "E6.2.0.31", {"center": v(-23.38, 13.5) * mm, "radius": 3.18 * mm});
            skCircle(sketch, "E6.2.0.32", {"center": v(-31.18, 27) * mm, "radius": 3.18 * mm});
            skCircle(sketch, "E6.2.0.33", {"center": v(-23.38, 40.5) * mm, "radius": 3.18 * mm});
            skCircle(sketch, "E6.2.0.34", {"center": v(-23.38, 31.5) * mm, "radius": 3.18 * mm});
            skCircle(sketch, "E6.2.0.35", {"center": v(-23.38, 121.5) * mm, "radius": 3.18 * mm});
            skCircle(sketch, "E6.2.0.36", {"center": v(-23.38, 49.5) * mm, "radius": 3.18 * mm});
            skCircle(sketch, "E6.2.0.37", {"center": v(-31.18, 126) * mm, "radius": 3.18 * mm});
            skCircle(sketch, "E6.2.0.38", {"center": v(-31.18, 54) * mm, "radius": 3.18 * mm});
            skCircle(sketch, "E6.2.0.39", {"center": v(-31.18, 18) * mm, "radius": 3.18 * mm});
            skCircle(sketch, "E6.2.0.40", {"center": v(-31.18, 0) * mm, "radius": 3.18 * mm});
            skCircle(sketch, "E6.3.0.0", {"center": v(-38.97, 76.5) * mm, "radius": 3.18 * mm});
            skCircle(sketch, "E6.3.0.1", {"center": v(-38.97, 148.5) * mm, "radius": 3.18 * mm});
            skCircle(sketch, "E6.3.0.2", {"center": v(-46.77, 135) * mm, "radius": 3.18 * mm});
            skCircle(sketch, "E6.3.0.3", {"center": v(-46.77, 63) * mm, "radius": 3.18 * mm});
            skCircle(sketch, "E6.3.0.4", {"center": v(-38.97, 139.5) * mm, "radius": 3.18 * mm});
            skCircle(sketch, "E6.3.0.5", {"center": v(-38.97, 67.5) * mm, "radius": 3.18 * mm});
            skCircle(sketch, "E6.3.0.6", {"center": v(-46.77, 144) * mm, "radius": 3.18 * mm});
            skCircle(sketch, "E6.3.0.7", {"center": v(-46.77, 72) * mm, "radius": 3.18 * mm});
            skCircle(sketch, "E6.3.0.8", {"center": v(-46.77, 81) * mm, "radius": 3.18 * mm});
            skCircle(sketch, "E6.3.0.9", {"center": v(-46.77, 153) * mm, "radius": 3.18 * mm});
            skCircle(sketch, "E6.3.0.10", {"center": v(-38.97, 94.5) * mm, "radius": 3.18 * mm});
            skCircle(sketch, "E6.3.0.12", {"center": v(-38.97, 85.5) * mm, "radius": 3.18 * mm});
            skCircle(sketch, "E6.3.0.14", {"center": v(-46.77, 90) * mm, "radius": 3.18 * mm});
            skCircle(sketch, "E6.3.0.15", {"center": v(-46.77, 162) * mm, "radius": 3.18 * mm});
            skCircle(sketch, "E6.3.0.16", {"center": v(-46.77, 99) * mm, "radius": 3.18 * mm});
            skCircle(sketch, "E6.3.0.17", {"center": v(-46.77, 171) * mm, "radius": 3.18 * mm});
            skCircle(sketch, "E6.3.0.18", {"center": v(-38.97, 130.5) * mm, "radius": 3.18 * mm});
            skCircle(sketch, "E6.3.0.19", {"center": v(-38.97, 112.5) * mm, "radius": 3.18 * mm});
            skCircle(sketch, "E6.3.0.20", {"center": v(-46.77, 108) * mm, "radius": 3.18 * mm});
            skCircle(sketch, "E6.3.0.21", {"center": v(-38.97, 103.5) * mm, "radius": 3.18 * mm});
            skCircle(sketch, "E6.3.0.22", {"center": v(-46.77, 117) * mm, "radius": 3.18 * mm});
            skCircle(sketch, "E6.3.0.23", {"center": v(-38.97, 58.5) * mm, "radius": 3.18 * mm});
            skCircle(sketch, "E6.3.0.24", {"center": v(-46.77, 36) * mm, "radius": 3.18 * mm});
            skCircle(sketch, "E6.3.0.25", {"center": v(-46.77, 45) * mm, "radius": 3.18 * mm});
            skLineSegment(sketch, "E6.3.0.26", {"start": v(-46.77, 0) * mm, "end": v(-46.77, 18) * mm, "construction": true});
            skCircle(sketch, "E6.3.0.27", {"center": v(-46.77, 9) * mm, "radius": 3.18 * mm});
            skCircle(sketch, "E6.3.0.28", {"center": v(-38.97, 4.5) * mm, "radius": 3.18 * mm});
            skCircle(sketch, "E6.3.0.29", {"center": v(-38.97, -4.5) * mm, "radius": 3.18 * mm});
            skCircle(sketch, "E6.3.0.30", {"center": v(-38.97, 22.5) * mm, "radius": 3.18 * mm});
            skCircle(sketch, "E6.3.0.31", {"center": v(-38.97, 13.5) * mm, "radius": 3.18 * mm});
            skCircle(sketch, "E6.3.0.32", {"center": v(-46.77, 27) * mm, "radius": 3.18 * mm});
            skCircle(sketch, "E6.3.0.33", {"center": v(-38.97, 40.5) * mm, "radius": 3.18 * mm});
            skCircle(sketch, "E6.3.0.34", {"center": v(-38.97, 31.5) * mm, "radius": 3.18 * mm});
            skCircle(sketch, "E6.3.0.35", {"center": v(-38.97, 121.5) * mm, "radius": 3.18 * mm});
            skCircle(sketch, "E6.3.0.36", {"center": v(-38.97, 49.5) * mm, "radius": 3.18 * mm});
            skCircle(sketch, "E6.3.0.37", {"center": v(-46.77, 126) * mm, "radius": 3.18 * mm});
            skCircle(sketch, "E6.3.0.38", {"center": v(-46.77, 54) * mm, "radius": 3.18 * mm});
            skCircle(sketch, "E6.3.0.39", {"center": v(-46.77, 18) * mm, "radius": 3.18 * mm});
            skCircle(sketch, "E6.3.0.40", {"center": v(-46.77, 0) * mm, "radius": 3.18 * mm});
            skCircle(sketch, "E6.4.0.0", {"center": v(-54.56, 76.5) * mm, "radius": 3.18 * mm});
            skCircle(sketch, "E6.4.0.1", {"center": v(-54.56, 148.5) * mm, "radius": 3.18 * mm});
            skCircle(sketch, "E6.4.0.2", {"center": v(-62.35, 135) * mm, "radius": 3.18 * mm});
            skCircle(sketch, "E6.4.0.3", {"center": v(-62.35, 63) * mm, "radius": 3.18 * mm});
            skCircle(sketch, "E6.4.0.4", {"center": v(-54.56, 139.5) * mm, "radius": 3.18 * mm});
            skCircle(sketch, "E6.4.0.5", {"center": v(-54.56, 67.5) * mm, "radius": 3.18 * mm});
            skCircle(sketch, "E6.4.0.6", {"center": v(-62.35, 144) * mm, "radius": 3.18 * mm});
            skCircle(sketch, "E6.4.0.7", {"center": v(-62.35, 72) * mm, "radius": 3.18 * mm});
            skCircle(sketch, "E6.4.0.8", {"center": v(-62.35, 81) * mm, "radius": 3.18 * mm});
            skCircle(sketch, "E6.4.0.9", {"center": v(-62.35, 153) * mm, "radius": 3.18 * mm});
            skCircle(sketch, "E6.4.0.10", {"center": v(-54.56, 94.5) * mm, "radius": 3.18 * mm});
            skCircle(sketch, "E6.4.0.11", {"center": v(-54.56, 166.5) * mm, "radius": 3.18 * mm});
            skCircle(sketch, "E6.4.0.12", {"center": v(-54.56, 85.5) * mm, "radius": 3.18 * mm});
            skCircle(sketch, "E6.4.0.13", {"center": v(-54.56, 157.5) * mm, "radius": 3.18 * mm});
            skCircle(sketch, "E6.4.0.14", {"center": v(-62.35, 90) * mm, "radius": 3.18 * mm});
            skCircle(sketch, "E6.4.0.15", {"center": v(-62.35, 162) * mm, "radius": 3.18 * mm});
            skCircle(sketch, "E6.4.0.16", {"center": v(-62.35, 99) * mm, "radius": 3.18 * mm});
            skCircle(sketch, "E6.4.0.17", {"center": v(-62.35, 171) * mm, "radius": 3.18 * mm});
            skCircle(sketch, "E6.4.0.18", {"center": v(-54.56, 130.5) * mm, "radius": 3.18 * mm});
            skCircle(sketch, "E6.4.0.19", {"center": v(-54.56, 112.5) * mm, "radius": 3.18 * mm});
            skCircle(sketch, "E6.4.0.20", {"center": v(-62.35, 108) * mm, "radius": 3.18 * mm});
            skCircle(sketch, "E6.4.0.21", {"center": v(-54.56, 103.5) * mm, "radius": 3.18 * mm});
            skCircle(sketch, "E6.4.0.22", {"center": v(-62.35, 117) * mm, "radius": 3.18 * mm});
            skCircle(sketch, "E6.4.0.23", {"center": v(-54.56, 58.5) * mm, "radius": 3.18 * mm});
            skCircle(sketch, "E6.4.0.24", {"center": v(-62.35, 36) * mm, "radius": 3.18 * mm});
            skCircle(sketch, "E6.4.0.25", {"center": v(-62.35, 45) * mm, "radius": 3.18 * mm});
            skLineSegment(sketch, "E6.4.0.26", {"start": v(-62.35, 0) * mm, "end": v(-62.35, 18) * mm, "construction": true});
            skCircle(sketch, "E6.4.0.27", {"center": v(-62.35, 9) * mm, "radius": 3.18 * mm});
            skCircle(sketch, "E6.4.0.28", {"center": v(-54.56, 4.5) * mm, "radius": 3.18 * mm});
            skCircle(sketch, "E6.4.0.29", {"center": v(-54.56, -4.5) * mm, "radius": 3.18 * mm});
            skCircle(sketch, "E6.4.0.30", {"center": v(-54.56, 22.5) * mm, "radius": 3.18 * mm});
            skCircle(sketch, "E6.4.0.31", {"center": v(-54.56, 13.5) * mm, "radius": 3.18 * mm});
            skCircle(sketch, "E6.4.0.32", {"center": v(-62.35, 27) * mm, "radius": 3.18 * mm});
            skCircle(sketch, "E6.4.0.33", {"center": v(-54.56, 40.5) * mm, "radius": 3.18 * mm});
            skCircle(sketch, "E6.4.0.34", {"center": v(-54.56, 31.5) * mm, "radius": 3.18 * mm});
            skCircle(sketch, "E6.4.0.35", {"center": v(-54.56, 121.5) * mm, "radius": 3.18 * mm});
            skCircle(sketch, "E6.4.0.36", {"center": v(-54.56, 49.5) * mm, "radius": 3.18 * mm});
            skCircle(sketch, "E6.4.0.37", {"center": v(-62.35, 126) * mm, "radius": 3.18 * mm});
            skCircle(sketch, "E6.4.0.38", {"center": v(-62.35, 54) * mm, "radius": 3.18 * mm});
            skCircle(sketch, "E6.4.0.39", {"center": v(-62.35, 18) * mm, "radius": 3.18 * mm});
            skCircle(sketch, "E6.4.0.40", {"center": v(-62.35, 0) * mm, "radius": 3.18 * mm});
            skCircle(sketch, "E6.5.0.0", {"center": v(-70.15, 76.5) * mm, "radius": 3.18 * mm});
            skCircle(sketch, "E6.5.0.1", {"center": v(-70.15, 148.5) * mm, "radius": 3.18 * mm});
            skCircle(sketch, "E6.5.0.2", {"center": v(-77.94, 135) * mm, "radius": 3.18 * mm});
            skCircle(sketch, "E6.5.0.3", {"center": v(-77.94, 63) * mm, "radius": 3.18 * mm});
            skCircle(sketch, "E6.5.0.4", {"center": v(-70.15, 139.5) * mm, "radius": 3.18 * mm});
            skCircle(sketch, "E6.5.0.5", {"center": v(-70.15, 67.5) * mm, "radius": 3.18 * mm});
            skCircle(sketch, "E6.5.0.6", {"center": v(-77.94, 144) * mm, "radius": 3.18 * mm});
            skCircle(sketch, "E6.5.0.7", {"center": v(-77.94, 72) * mm, "radius": 3.18 * mm});
            skCircle(sketch, "E6.5.0.8", {"center": v(-77.94, 81) * mm, "radius": 3.18 * mm});
            skCircle(sketch, "E6.5.0.9", {"center": v(-77.94, 153) * mm, "radius": 3.18 * mm});
            skCircle(sketch, "E6.5.0.10", {"center": v(-70.15, 94.5) * mm, "radius": 3.18 * mm});
            skCircle(sketch, "E6.5.0.11", {"center": v(-70.15, 166.5) * mm, "radius": 3.18 * mm});
            skCircle(sketch, "E6.5.0.12", {"center": v(-70.15, 85.5) * mm, "radius": 3.18 * mm});
            skCircle(sketch, "E6.5.0.13", {"center": v(-70.15, 157.5) * mm, "radius": 3.18 * mm});
            skCircle(sketch, "E6.5.0.14", {"center": v(-77.94, 90) * mm, "radius": 3.18 * mm});
            skCircle(sketch, "E6.5.0.15", {"center": v(-77.94, 162) * mm, "radius": 3.18 * mm});
            skCircle(sketch, "E6.5.0.16", {"center": v(-77.94, 99) * mm, "radius": 3.18 * mm});
            skCircle(sketch, "E6.5.0.17", {"center": v(-77.94, 171) * mm, "radius": 3.18 * mm});
            skCircle(sketch, "E6.5.0.18", {"center": v(-70.15, 130.5) * mm, "radius": 3.18 * mm});
            skCircle(sketch, "E6.5.0.19", {"center": v(-70.15, 112.5) * mm, "radius": 3.18 * mm});
            skCircle(sketch, "E6.5.0.20", {"center": v(-77.94, 108) * mm, "radius": 3.18 * mm});
            skCircle(sketch, "E6.5.0.21", {"center": v(-70.15, 103.5) * mm, "radius": 3.18 * mm});
            skCircle(sketch, "E6.5.0.22", {"center": v(-77.94, 117) * mm, "radius": 3.18 * mm});
            skCircle(sketch, "E6.5.0.23", {"center": v(-70.15, 58.5) * mm, "radius": 3.18 * mm});
            skCircle(sketch, "E6.5.0.24", {"center": v(-77.94, 36) * mm, "radius": 3.18 * mm});
            skCircle(sketch, "E6.5.0.25", {"center": v(-77.94, 45) * mm, "radius": 3.18 * mm});
            skLineSegment(sketch, "E6.5.0.26", {"start": v(-77.94, 0) * mm, "end": v(-77.94, 18) * mm, "construction": true});
            skCircle(sketch, "E6.5.0.27", {"center": v(-77.94, 9) * mm, "radius": 3.18 * mm});
            skCircle(sketch, "E6.5.0.28", {"center": v(-70.15, 4.5) * mm, "radius": 3.18 * mm});
            skCircle(sketch, "E6.5.0.29", {"center": v(-70.15, -4.5) * mm, "radius": 3.18 * mm});
            skCircle(sketch, "E6.5.0.30", {"center": v(-70.15, 22.5) * mm, "radius": 3.18 * mm});
            skCircle(sketch, "E6.5.0.31", {"center": v(-70.15, 13.5) * mm, "radius": 3.18 * mm});
            skCircle(sketch, "E6.5.0.32", {"center": v(-77.94, 27) * mm, "radius": 3.18 * mm});
            skCircle(sketch, "E6.5.0.33", {"center": v(-70.15, 40.5) * mm, "radius": 3.18 * mm});
            skCircle(sketch, "E6.5.0.34", {"center": v(-70.15, 31.5) * mm, "radius": 3.18 * mm});
            skCircle(sketch, "E6.5.0.35", {"center": v(-70.15, 121.5) * mm, "radius": 3.18 * mm});
            skCircle(sketch, "E6.5.0.36", {"center": v(-70.15, 49.5) * mm, "radius": 3.18 * mm});
            skCircle(sketch, "E6.5.0.37", {"center": v(-77.94, 126) * mm, "radius": 3.18 * mm});
            skCircle(sketch, "E6.5.0.38", {"center": v(-77.94, 54) * mm, "radius": 3.18 * mm});
            skCircle(sketch, "E6.5.0.39", {"center": v(-77.94, 18) * mm, "radius": 3.18 * mm});
            skCircle(sketch, "E6.5.0.40", {"center": v(-77.94, 0) * mm, "radius": 3.18 * mm});
            skCircle(sketch, "E6.6.0.0", {"center": v(-85.74, 76.5) * mm, "radius": 3.18 * mm});
            skCircle(sketch, "E6.6.0.1", {"center": v(-85.74, 148.5) * mm, "radius": 3.18 * mm});
            skCircle(sketch, "E6.6.0.2", {"center": v(-93.53, 135) * mm, "radius": 3.18 * mm});
            skCircle(sketch, "E6.6.0.3", {"center": v(-93.53, 63) * mm, "radius": 3.18 * mm});
            skCircle(sketch, "E6.6.0.4", {"center": v(-85.74, 139.5) * mm, "radius": 3.18 * mm});
            skCircle(sketch, "E6.6.0.5", {"center": v(-85.74, 67.5) * mm, "radius": 3.18 * mm});
            skCircle(sketch, "E6.6.0.6", {"center": v(-93.53, 144) * mm, "radius": 3.18 * mm});
            skCircle(sketch, "E6.6.0.7", {"center": v(-93.53, 72) * mm, "radius": 3.18 * mm});
            skCircle(sketch, "E6.6.0.8", {"center": v(-93.53, 81) * mm, "radius": 3.18 * mm});
            skCircle(sketch, "E6.6.0.9", {"center": v(-93.53, 153) * mm, "radius": 3.18 * mm});
            skCircle(sketch, "E6.6.0.10", {"center": v(-85.74, 94.5) * mm, "radius": 3.18 * mm});
            skCircle(sketch, "E6.6.0.11", {"center": v(-85.74, 166.5) * mm, "radius": 3.18 * mm});
            skCircle(sketch, "E6.6.0.12", {"center": v(-85.74, 85.5) * mm, "radius": 3.18 * mm});
            skCircle(sketch, "E6.6.0.13", {"center": v(-85.74, 157.5) * mm, "radius": 3.18 * mm});
            skCircle(sketch, "E6.6.0.14", {"center": v(-93.53, 90) * mm, "radius": 3.18 * mm});
            skCircle(sketch, "E6.6.0.15", {"center": v(-93.53, 162) * mm, "radius": 3.18 * mm});
            skCircle(sketch, "E6.6.0.16", {"center": v(-93.53, 99) * mm, "radius": 3.18 * mm});
            skCircle(sketch, "E6.6.0.17", {"center": v(-93.53, 171) * mm, "radius": 3.18 * mm});
            skCircle(sketch, "E6.6.0.18", {"center": v(-85.74, 130.5) * mm, "radius": 3.18 * mm});
            skCircle(sketch, "E6.6.0.19", {"center": v(-85.74, 112.5) * mm, "radius": 3.18 * mm});
            skCircle(sketch, "E6.6.0.20", {"center": v(-93.53, 108) * mm, "radius": 3.18 * mm});
            skCircle(sketch, "E6.6.0.21", {"center": v(-85.74, 103.5) * mm, "radius": 3.18 * mm});
            skCircle(sketch, "E6.6.0.22", {"center": v(-93.53, 117) * mm, "radius": 3.18 * mm});
            skCircle(sketch, "E6.6.0.23", {"center": v(-85.74, 58.5) * mm, "radius": 3.18 * mm});
            skCircle(sketch, "E6.6.0.24", {"center": v(-93.53, 36) * mm, "radius": 3.18 * mm});
            skCircle(sketch, "E6.6.0.25", {"center": v(-93.53, 45) * mm, "radius": 3.18 * mm});
            skLineSegment(sketch, "E6.6.0.26", {"start": v(-93.53, 0) * mm, "end": v(-93.53, 18) * mm, "construction": true});
            skCircle(sketch, "E6.6.0.27", {"center": v(-93.53, 9) * mm, "radius": 3.18 * mm});
            skCircle(sketch, "E6.6.0.28", {"center": v(-85.74, 4.5) * mm, "radius": 3.18 * mm});
            skCircle(sketch, "E6.6.0.29", {"center": v(-85.74, -4.5) * mm, "radius": 3.18 * mm});
            skCircle(sketch, "E6.6.0.30", {"center": v(-85.74, 22.5) * mm, "radius": 3.18 * mm});
            skCircle(sketch, "E6.6.0.31", {"center": v(-85.74, 13.5) * mm, "radius": 3.18 * mm});
            skCircle(sketch, "E6.6.0.32", {"center": v(-93.53, 27) * mm, "radius": 3.18 * mm});
            skCircle(sketch, "E6.6.0.33", {"center": v(-85.74, 40.5) * mm, "radius": 3.18 * mm});
            skCircle(sketch, "E6.6.0.34", {"center": v(-85.74, 31.5) * mm, "radius": 3.18 * mm});
            skCircle(sketch, "E6.6.0.35", {"center": v(-85.74, 121.5) * mm, "radius": 3.18 * mm});
            skCircle(sketch, "E6.6.0.36", {"center": v(-85.74, 49.5) * mm, "radius": 3.18 * mm});
            skCircle(sketch, "E6.6.0.37", {"center": v(-93.53, 126) * mm, "radius": 3.18 * mm});
            skCircle(sketch, "E6.6.0.38", {"center": v(-93.53, 54) * mm, "radius": 3.18 * mm});
            skCircle(sketch, "E6.6.0.39", {"center": v(-93.53, 18) * mm, "radius": 3.18 * mm});
            skCircle(sketch, "E6.6.0.40", {"center": v(-93.53, 0) * mm, "radius": 3.18 * mm});
            skCircle(sketch, "E6.7.0.0", {"center": v(-101.32, 76.5) * mm, "radius": 3.18 * mm});
            skCircle(sketch, "E6.7.0.1", {"center": v(-101.32, 148.5) * mm, "radius": 3.18 * mm});
            skCircle(sketch, "E6.7.0.2", {"center": v(-109.12, 135) * mm, "radius": 3.18 * mm});
            skCircle(sketch, "E6.7.0.3", {"center": v(-109.12, 63) * mm, "radius": 3.18 * mm});
            skCircle(sketch, "E6.7.0.4", {"center": v(-101.32, 139.5) * mm, "radius": 3.18 * mm});
            skCircle(sketch, "E6.7.0.5", {"center": v(-101.32, 67.5) * mm, "radius": 3.18 * mm});
            skCircle(sketch, "E6.7.0.6", {"center": v(-109.12, 144) * mm, "radius": 3.18 * mm});
            skCircle(sketch, "E6.7.0.7", {"center": v(-109.12, 72) * mm, "radius": 3.18 * mm});
            skCircle(sketch, "E6.7.0.8", {"center": v(-109.12, 81) * mm, "radius": 3.18 * mm});
            skCircle(sketch, "E6.7.0.9", {"center": v(-109.12, 153) * mm, "radius": 3.18 * mm});
            skCircle(sketch, "E6.7.0.10", {"center": v(-101.32, 94.5) * mm, "radius": 3.18 * mm});
            skCircle(sketch, "E6.7.0.11", {"center": v(-101.32, 166.5) * mm, "radius": 3.18 * mm});
            skCircle(sketch, "E6.7.0.12", {"center": v(-101.32, 85.5) * mm, "radius": 3.18 * mm});
            skCircle(sketch, "E6.7.0.13", {"center": v(-101.32, 157.5) * mm, "radius": 3.18 * mm});
            skCircle(sketch, "E6.7.0.14", {"center": v(-109.12, 90) * mm, "radius": 3.18 * mm});
            skCircle(sketch, "E6.7.0.15", {"center": v(-109.12, 162) * mm, "radius": 3.18 * mm});
            skCircle(sketch, "E6.7.0.16", {"center": v(-109.12, 99) * mm, "radius": 3.18 * mm});
            skCircle(sketch, "E6.7.0.17", {"center": v(-109.12, 171) * mm, "radius": 3.18 * mm});
            skCircle(sketch, "E6.7.0.18", {"center": v(-101.32, 130.5) * mm, "radius": 3.18 * mm});
            skCircle(sketch, "E6.7.0.19", {"center": v(-101.32, 112.5) * mm, "radius": 3.18 * mm});
            skCircle(sketch, "E6.7.0.20", {"center": v(-109.12, 108) * mm, "radius": 3.18 * mm});
            skCircle(sketch, "E6.7.0.21", {"center": v(-101.32, 103.5) * mm, "radius": 3.18 * mm});
            skCircle(sketch, "E6.7.0.22", {"center": v(-109.12, 117) * mm, "radius": 3.18 * mm});
            skCircle(sketch, "E6.7.0.23", {"center": v(-101.32, 58.5) * mm, "radius": 3.18 * mm});
            skCircle(sketch, "E6.7.0.24", {"center": v(-109.12, 36) * mm, "radius": 3.18 * mm});
            skCircle(sketch, "E6.7.0.25", {"center": v(-109.12, 45) * mm, "radius": 3.18 * mm});
            skLineSegment(sketch, "E6.7.0.26", {"start": v(-109.12, 0) * mm, "end": v(-109.12, 18) * mm, "construction": true});
            skCircle(sketch, "E6.7.0.27", {"center": v(-109.12, 9) * mm, "radius": 3.18 * mm});
            skCircle(sketch, "E6.7.0.28", {"center": v(-101.32, 4.5) * mm, "radius": 3.18 * mm});
            skCircle(sketch, "E6.7.0.29", {"center": v(-101.32, -4.5) * mm, "radius": 3.18 * mm});
            skCircle(sketch, "E6.7.0.30", {"center": v(-101.32, 22.5) * mm, "radius": 3.18 * mm});
            skCircle(sketch, "E6.7.0.31", {"center": v(-101.32, 13.5) * mm, "radius": 3.18 * mm});
            skCircle(sketch, "E6.7.0.32", {"center": v(-109.12, 27) * mm, "radius": 3.18 * mm});
            skCircle(sketch, "E6.7.0.33", {"center": v(-101.32, 40.5) * mm, "radius": 3.18 * mm});
            skCircle(sketch, "E6.7.0.34", {"center": v(-101.32, 31.5) * mm, "radius": 3.18 * mm});
            skCircle(sketch, "E6.7.0.35", {"center": v(-101.32, 121.5) * mm, "radius": 3.18 * mm});
            skCircle(sketch, "E6.7.0.36", {"center": v(-101.32, 49.5) * mm, "radius": 3.18 * mm});
            skCircle(sketch, "E6.7.0.37", {"center": v(-109.12, 126) * mm, "radius": 3.18 * mm});
            skCircle(sketch, "E6.7.0.38", {"center": v(-109.12, 54) * mm, "radius": 3.18 * mm});
            skCircle(sketch, "E6.7.0.39", {"center": v(-109.12, 18) * mm, "radius": 3.18 * mm});
            skCircle(sketch, "E6.7.0.40", {"center": v(-109.12, 0) * mm, "radius": 3.18 * mm});
            skCircle(sketch, "E6.8.0.0", {"center": v(-116.91, 76.5) * mm, "radius": 3.18 * mm});
            skCircle(sketch, "E6.8.0.1", {"center": v(-116.91, 148.5) * mm, "radius": 3.18 * mm});
            skCircle(sketch, "E6.8.0.2", {"center": v(-124.7, 135) * mm, "radius": 3.18 * mm});
            skCircle(sketch, "E6.8.0.3", {"center": v(-124.7, 63) * mm, "radius": 3.18 * mm});
            skCircle(sketch, "E6.8.0.4", {"center": v(-116.91, 139.5) * mm, "radius": 3.18 * mm});
            skCircle(sketch, "E6.8.0.5", {"center": v(-116.91, 67.5) * mm, "radius": 3.18 * mm});
            skCircle(sketch, "E6.8.0.6", {"center": v(-124.7, 144) * mm, "radius": 3.18 * mm});
            skCircle(sketch, "E6.8.0.7", {"center": v(-124.7, 72) * mm, "radius": 3.18 * mm});
            skCircle(sketch, "E6.8.0.8", {"center": v(-124.7, 81) * mm, "radius": 3.18 * mm});
            skCircle(sketch, "E6.8.0.9", {"center": v(-124.7, 153) * mm, "radius": 3.18 * mm});
            skCircle(sketch, "E6.8.0.10", {"center": v(-116.91, 94.5) * mm, "radius": 3.18 * mm});
            skCircle(sketch, "E6.8.0.11", {"center": v(-116.91, 166.5) * mm, "radius": 3.18 * mm});
            skCircle(sketch, "E6.8.0.12", {"center": v(-116.91, 85.5) * mm, "radius": 3.18 * mm});
            skCircle(sketch, "E6.8.0.13", {"center": v(-116.91, 157.5) * mm, "radius": 3.18 * mm});
            skCircle(sketch, "E6.8.0.14", {"center": v(-124.7, 90) * mm, "radius": 3.18 * mm});
            skCircle(sketch, "E6.8.0.15", {"center": v(-124.7, 162) * mm, "radius": 3.18 * mm});
            skCircle(sketch, "E6.8.0.16", {"center": v(-124.7, 99) * mm, "radius": 3.18 * mm});
            skCircle(sketch, "E6.8.0.17", {"center": v(-124.7, 171) * mm, "radius": 3.18 * mm});
            skCircle(sketch, "E6.8.0.18", {"center": v(-116.91, 130.5) * mm, "radius": 3.18 * mm});
            skCircle(sketch, "E6.8.0.19", {"center": v(-116.91, 112.5) * mm, "radius": 3.18 * mm});
            skCircle(sketch, "E6.8.0.20", {"center": v(-124.7, 108) * mm, "radius": 3.18 * mm});
            skCircle(sketch, "E6.8.0.21", {"center": v(-116.91, 103.5) * mm, "radius": 3.18 * mm});
            skCircle(sketch, "E6.8.0.22", {"center": v(-124.7, 117) * mm, "radius": 3.18 * mm});
            skCircle(sketch, "E6.8.0.23", {"center": v(-116.91, 58.5) * mm, "radius": 3.18 * mm});
            skCircle(sketch, "E6.8.0.24", {"center": v(-124.7, 36) * mm, "radius": 3.18 * mm});
            skCircle(sketch, "E6.8.0.25", {"center": v(-124.7, 45) * mm, "radius": 3.18 * mm});
            skLineSegment(sketch, "E6.8.0.26", {"start": v(-124.7, 0) * mm, "end": v(-124.7, 18) * mm, "construction": true});
            skCircle(sketch, "E6.8.0.27", {"center": v(-124.7, 9) * mm, "radius": 3.18 * mm});
            skCircle(sketch, "E6.8.0.28", {"center": v(-116.91, 4.5) * mm, "radius": 3.18 * mm});
            skCircle(sketch, "E6.8.0.29", {"center": v(-116.91, -4.5) * mm, "radius": 3.18 * mm});
            skCircle(sketch, "E6.8.0.30", {"center": v(-116.91, 22.5) * mm, "radius": 3.18 * mm});
            skCircle(sketch, "E6.8.0.31", {"center": v(-116.91, 13.5) * mm, "radius": 3.18 * mm});
            skCircle(sketch, "E6.8.0.32", {"center": v(-124.7, 27) * mm, "radius": 3.18 * mm});
            skCircle(sketch, "E6.8.0.33", {"center": v(-116.91, 40.5) * mm, "radius": 3.18 * mm});
            skCircle(sketch, "E6.8.0.34", {"center": v(-116.91, 31.5) * mm, "radius": 3.18 * mm});
            skCircle(sketch, "E6.8.0.35", {"center": v(-116.91, 121.5) * mm, "radius": 3.18 * mm});
            skCircle(sketch, "E6.8.0.36", {"center": v(-116.91, 49.5) * mm, "radius": 3.18 * mm});
            skCircle(sketch, "E6.8.0.37", {"center": v(-124.7, 126) * mm, "radius": 3.18 * mm});
            skCircle(sketch, "E6.8.0.38", {"center": v(-124.7, 54) * mm, "radius": 3.18 * mm});
            skCircle(sketch, "E6.8.0.39", {"center": v(-124.7, 18) * mm, "radius": 3.18 * mm});
            skCircle(sketch, "E6.8.0.40", {"center": v(-124.7, 0) * mm, "radius": 3.18 * mm});
            skCircle(sketch, "E6.9.0.0", {"center": v(-132.5, 76.5) * mm, "radius": 3.18 * mm});
            skCircle(sketch, "E6.9.0.1", {"center": v(-132.5, 148.5) * mm, "radius": 3.18 * mm});
            skCircle(sketch, "E6.9.0.2", {"center": v(-140.3, 135) * mm, "radius": 3.18 * mm});
            skCircle(sketch, "E6.9.0.3", {"center": v(-140.3, 63) * mm, "radius": 3.18 * mm});
            skCircle(sketch, "E6.9.0.4", {"center": v(-132.5, 139.5) * mm, "radius": 3.18 * mm});
            skCircle(sketch, "E6.9.0.5", {"center": v(-132.5, 67.5) * mm, "radius": 3.18 * mm});
            skCircle(sketch, "E6.9.0.6", {"center": v(-140.3, 144) * mm, "radius": 3.18 * mm});
            skCircle(sketch, "E6.9.0.7", {"center": v(-140.3, 72) * mm, "radius": 3.18 * mm});
            skCircle(sketch, "E6.9.0.8", {"center": v(-140.3, 81) * mm, "radius": 3.18 * mm});
            skCircle(sketch, "E6.9.0.9", {"center": v(-140.3, 153) * mm, "radius": 3.18 * mm});
            skCircle(sketch, "E6.9.0.10", {"center": v(-132.5, 94.5) * mm, "radius": 3.18 * mm});
            skCircle(sketch, "E6.9.0.11", {"center": v(-132.5, 166.5) * mm, "radius": 3.18 * mm});
            skCircle(sketch, "E6.9.0.12", {"center": v(-132.5, 85.5) * mm, "radius": 3.18 * mm});
            skCircle(sketch, "E6.9.0.13", {"center": v(-132.5, 157.5) * mm, "radius": 3.18 * mm});
            skCircle(sketch, "E6.9.0.14", {"center": v(-140.3, 90) * mm, "radius": 3.18 * mm});
            skCircle(sketch, "E6.9.0.15", {"center": v(-140.3, 162) * mm, "radius": 3.18 * mm});
            skCircle(sketch, "E6.9.0.16", {"center": v(-140.3, 99) * mm, "radius": 3.18 * mm});
            skCircle(sketch, "E6.9.0.17", {"center": v(-140.3, 171) * mm, "radius": 3.18 * mm});
            skCircle(sketch, "E6.9.0.18", {"center": v(-132.5, 130.5) * mm, "radius": 3.18 * mm});
            skCircle(sketch, "E6.9.0.19", {"center": v(-132.5, 112.5) * mm, "radius": 3.18 * mm});
            skCircle(sketch, "E6.9.0.20", {"center": v(-140.3, 108) * mm, "radius": 3.18 * mm});
            skCircle(sketch, "E6.9.0.21", {"center": v(-132.5, 103.5) * mm, "radius": 3.18 * mm});
            skCircle(sketch, "E6.9.0.22", {"center": v(-140.3, 117) * mm, "radius": 3.18 * mm});
            skCircle(sketch, "E6.9.0.23", {"center": v(-132.5, 58.5) * mm, "radius": 3.18 * mm});
            skCircle(sketch, "E6.9.0.24", {"center": v(-140.3, 36) * mm, "radius": 3.18 * mm});
            skCircle(sketch, "E6.9.0.25", {"center": v(-140.3, 45) * mm, "radius": 3.18 * mm});
            skLineSegment(sketch, "E6.9.0.26", {"start": v(-140.3, 0) * mm, "end": v(-140.3, 18) * mm, "construction": true});
            skCircle(sketch, "E6.9.0.27", {"center": v(-140.3, 9) * mm, "radius": 3.18 * mm});
            skCircle(sketch, "E6.9.0.28", {"center": v(-132.5, 4.5) * mm, "radius": 3.18 * mm});
            skCircle(sketch, "E6.9.0.29", {"center": v(-132.5, -4.5) * mm, "radius": 3.18 * mm});
            skCircle(sketch, "E6.9.0.30", {"center": v(-132.5, 22.5) * mm, "radius": 3.18 * mm});
            skCircle(sketch, "E6.9.0.31", {"center": v(-132.5, 13.5) * mm, "radius": 3.18 * mm});
            skCircle(sketch, "E6.9.0.32", {"center": v(-140.3, 27) * mm, "radius": 3.18 * mm});
            skCircle(sketch, "E6.9.0.33", {"center": v(-132.5, 40.5) * mm, "radius": 3.18 * mm});
            skCircle(sketch, "E6.9.0.34", {"center": v(-132.5, 31.5) * mm, "radius": 3.18 * mm});
            skCircle(sketch, "E6.9.0.35", {"center": v(-132.5, 121.5) * mm, "radius": 3.18 * mm});
            skCircle(sketch, "E6.9.0.36", {"center": v(-132.5, 49.5) * mm, "radius": 3.18 * mm});
            skCircle(sketch, "E6.9.0.37", {"center": v(-140.3, 126) * mm, "radius": 3.18 * mm});
            skCircle(sketch, "E6.9.0.38", {"center": v(-140.3, 54) * mm, "radius": 3.18 * mm});
            skCircle(sketch, "E6.9.0.39", {"center": v(-140.3, 18) * mm, "radius": 3.18 * mm});
            skCircle(sketch, "E6.9.0.40", {"center": v(-140.3, 0) * mm, "radius": 3.18 * mm});
            skCircle(sketch, "E6.10.0.0", {"center": v(-148.1, 76.5) * mm, "radius": 3.18 * mm});
            skCircle(sketch, "E6.10.0.1", {"center": v(-148.1, 148.5) * mm, "radius": 3.18 * mm});
            skCircle(sketch, "E6.10.0.2", {"center": v(-155.88, 135) * mm, "radius": 3.18 * mm});
            skCircle(sketch, "E6.10.0.3", {"center": v(-155.88, 63) * mm, "radius": 3.18 * mm});
            skCircle(sketch, "E6.10.0.4", {"center": v(-148.1, 139.5) * mm, "radius": 3.18 * mm});
            skCircle(sketch, "E6.10.0.5", {"center": v(-148.1, 67.5) * mm, "radius": 3.18 * mm});
            skCircle(sketch, "E6.10.0.6", {"center": v(-155.88, 144) * mm, "radius": 3.18 * mm});
            skCircle(sketch, "E6.10.0.7", {"center": v(-155.88, 72) * mm, "radius": 3.18 * mm});
            skCircle(sketch, "E6.10.0.8", {"center": v(-155.88, 81) * mm, "radius": 3.18 * mm});
            skCircle(sketch, "E6.10.0.9", {"center": v(-155.88, 153) * mm, "radius": 3.18 * mm});
            skCircle(sketch, "E6.10.0.10", {"center": v(-148.1, 94.5) * mm, "radius": 3.18 * mm});
            skCircle(sketch, "E6.10.0.11", {"center": v(-148.1, 166.5) * mm, "radius": 3.18 * mm});
            skCircle(sketch, "E6.10.0.12", {"center": v(-148.1, 85.5) * mm, "radius": 3.18 * mm});
            skCircle(sketch, "E6.10.0.13", {"center": v(-148.1, 157.5) * mm, "radius": 3.18 * mm});
            skCircle(sketch, "E6.10.0.14", {"center": v(-155.88, 90) * mm, "radius": 3.18 * mm});
            skCircle(sketch, "E6.10.0.15", {"center": v(-155.88, 162) * mm, "radius": 3.18 * mm});
            skCircle(sketch, "E6.10.0.16", {"center": v(-155.88, 99) * mm, "radius": 3.18 * mm});
            skCircle(sketch, "E6.10.0.17", {"center": v(-155.88, 171) * mm, "radius": 3.18 * mm});
            skCircle(sketch, "E6.10.0.18", {"center": v(-148.1, 130.5) * mm, "radius": 3.18 * mm});
            skCircle(sketch, "E6.10.0.19", {"center": v(-148.1, 112.5) * mm, "radius": 3.18 * mm});
            skCircle(sketch, "E6.10.0.20", {"center": v(-155.88, 108) * mm, "radius": 3.18 * mm});
            skCircle(sketch, "E6.10.0.21", {"center": v(-148.1, 103.5) * mm, "radius": 3.18 * mm});
            skCircle(sketch, "E6.10.0.22", {"center": v(-155.88, 117) * mm, "radius": 3.18 * mm});
            skCircle(sketch, "E6.10.0.23", {"center": v(-148.1, 58.5) * mm, "radius": 3.18 * mm});
            skCircle(sketch, "E6.10.0.24", {"center": v(-155.88, 36) * mm, "radius": 3.18 * mm});
            skCircle(sketch, "E6.10.0.25", {"center": v(-155.88, 45) * mm, "radius": 3.18 * mm});
            skLineSegment(sketch, "E6.10.0.26", {"start": v(-155.88, 0) * mm, "end": v(-155.88, 18) * mm, "construction": true});
            skCircle(sketch, "E6.10.0.27", {"center": v(-155.88, 9) * mm, "radius": 3.18 * mm});
            skCircle(sketch, "E6.10.0.28", {"center": v(-148.1, 4.5) * mm, "radius": 3.18 * mm});
            skCircle(sketch, "E6.10.0.29", {"center": v(-148.1, -4.5) * mm, "radius": 3.18 * mm});
            skCircle(sketch, "E6.10.0.30", {"center": v(-148.1, 22.5) * mm, "radius": 3.18 * mm});
            skCircle(sketch, "E6.10.0.31", {"center": v(-148.1, 13.5) * mm, "radius": 3.18 * mm});
            skCircle(sketch, "E6.10.0.32", {"center": v(-155.88, 27) * mm, "radius": 3.18 * mm});
            skCircle(sketch, "E6.10.0.33", {"center": v(-148.1, 40.5) * mm, "radius": 3.18 * mm});
            skCircle(sketch, "E6.10.0.34", {"center": v(-148.1, 31.5) * mm, "radius": 3.18 * mm});
            skCircle(sketch, "E6.10.0.35", {"center": v(-148.1, 121.5) * mm, "radius": 3.18 * mm});
            skCircle(sketch, "E6.10.0.36", {"center": v(-148.1, 49.5) * mm, "radius": 3.18 * mm});
            skCircle(sketch, "E6.10.0.37", {"center": v(-155.88, 126) * mm, "radius": 3.18 * mm});
            skCircle(sketch, "E6.10.0.38", {"center": v(-155.88, 54) * mm, "radius": 3.18 * mm});
            skCircle(sketch, "E6.10.0.39", {"center": v(-155.88, 18) * mm, "radius": 3.18 * mm});
            skCircle(sketch, "E6.10.0.40", {"center": v(-155.88, 0) * mm, "radius": 3.18 * mm});
            skLineSegment(sketch, "E6.direction1", {"start": v(0, 0) * mm, "end": v(-15.59, 0) * mm, "construction": true});
            skCircle(sketch, "E7.0.1.0", {"center": v(54.54, -13.5) * mm, "radius": 3.18 * mm});
            skCircle(sketch, "E7.0.1.1", {"center": v(23.37, -13.5) * mm, "radius": 3.18 * mm});
            skCircle(sketch, "E7.0.1.2", {"center": v(-7.8, -13.5) * mm, "radius": 3.18 * mm});
            skCircle(sketch, "E7.0.1.3", {"center": v(-70.16, -13.5) * mm, "radius": 3.18 * mm});
            skCircle(sketch, "E7.0.1.4", {"center": v(-38.99, -13.5) * mm, "radius": 3.18 * mm});
            skCircle(sketch, "E7.0.1.5", {"center": v(7.78, -13.5) * mm, "radius": 3.18 * mm});
            skCircle(sketch, "E7.0.1.6", {"center": v(124.7, -9) * mm, "radius": 3.18 * mm});
            skCircle(sketch, "E7.0.1.8", {"center": v(-132.52, -13.5) * mm, "radius": 3.18 * mm});
            skCircle(sketch, "E7.0.1.9", {"center": v(-101.34, -13.5) * mm, "radius": 3.18 * mm});
            skCircle(sketch, "E7.0.1.10", {"center": v(31.16, -9) * mm, "radius": 3.18 * mm});
            skCircle(sketch, "E7.0.1.11", {"center": v(101.3, -13.5) * mm, "radius": 3.18 * mm});
            skCircle(sketch, "E7.0.1.12", {"center": v(93.52, -9) * mm, "radius": 3.18 * mm});
            skCircle(sketch, "E7.0.1.13", {"center": v(62.34, -9) * mm, "radius": 3.18 * mm});
            skCircle(sketch, "E7.0.1.14", {"center": v(70.13, -13.5) * mm, "radius": 3.18 * mm});
            skCircle(sketch, "E7.0.1.15", {"center": v(38.96, -13.5) * mm, "radius": 3.18 * mm});
            skCircle(sketch, "E7.0.1.17", {"center": v(132.49, -13.5) * mm, "radius": 3.18 * mm});
            skCircle(sketch, "E7.0.1.18", {"center": v(85.72, -13.5) * mm, "radius": 3.18 * mm});
            skCircle(sketch, "E7.0.1.19", {"center": v(116.9, -13.5) * mm, "radius": 3.18 * mm});
            skCircle(sketch, "E7.0.1.21", {"center": v(46.75, -9) * mm, "radius": 3.18 * mm});
            skCircle(sketch, "E7.0.1.22", {"center": v(77.93, -9) * mm, "radius": 3.18 * mm});
            skCircle(sketch, "E7.0.1.23", {"center": v(109.1, -9) * mm, "radius": 3.18 * mm});
            skCircle(sketch, "E7.0.1.24", {"center": v(140.28, -9) * mm, "radius": 3.18 * mm});
            skCircle(sketch, "E7.0.1.25", {"center": v(-148.1, -13.5) * mm, "radius": 3.18 * mm});
            skCircle(sketch, "E7.0.1.26", {"center": v(-23.4, -13.5) * mm, "radius": 3.18 * mm});
            skCircle(sketch, "E7.0.1.27", {"center": v(-54.57, -13.5) * mm, "radius": 3.18 * mm});
            skCircle(sketch, "E7.0.1.28", {"center": v(-85.75, -13.5) * mm, "radius": 3.18 * mm});
            skCircle(sketch, "E7.0.1.29", {"center": v(-116.93, -13.5) * mm, "radius": 3.18 * mm});
            skLineSegment(sketch, "E7.0.1.30", {"start": v(-0.02, -9) * mm, "end": v(15.57, -9) * mm, "construction": true});
            skLineSegment(sketch, "E7.0.1.31", {"start": v(-0.02, -9) * mm, "end": v(-15.6, -9) * mm, "construction": true});
            skCircle(sketch, "E7.0.1.32", {"center": v(-31.2, -9) * mm, "radius": 3.18 * mm});
            skCircle(sketch, "E7.0.1.33", {"center": v(-155.9, -9) * mm, "radius": 3.18 * mm});
            skCircle(sketch, "E7.0.1.34", {"center": v(-62.37, -9) * mm, "radius": 3.18 * mm});
            skCircle(sketch, "E7.0.1.35", {"center": v(-140.31, -9) * mm, "radius": 3.18 * mm});
            skCircle(sketch, "E7.0.1.36", {"center": v(-77.96, -9) * mm, "radius": 3.18 * mm});
            skCircle(sketch, "E7.0.1.37", {"center": v(-46.78, -9) * mm, "radius": 3.18 * mm});
            skCircle(sketch, "E7.0.1.38", {"center": v(-109.13, -9) * mm, "radius": 3.18 * mm});
            skCircle(sketch, "E7.0.1.39", {"center": v(-124.72, -9) * mm, "radius": 3.18 * mm});
            skCircle(sketch, "E7.0.1.40", {"center": v(-93.55, -9) * mm, "radius": 3.18 * mm});
            skCircle(sketch, "E7.0.1.41", {"center": v(15.57, -9) * mm, "radius": 3.18 * mm});
            skCircle(sketch, "E7.0.1.42", {"center": v(-15.6, -9) * mm, "radius": 3.18 * mm});
            skCircle(sketch, "E7.0.1.43", {"center": v(-0.02, -9) * mm, "radius": 3.18 * mm});
            skCircle(sketch, "E7.0.2.0", {"center": v(54.53, -22.5) * mm, "radius": 3.18 * mm});
            skCircle(sketch, "E7.0.2.1", {"center": v(23.35, -22.5) * mm, "radius": 3.18 * mm});
            skCircle(sketch, "E7.0.2.2", {"center": v(-7.82, -22.5) * mm, "radius": 3.18 * mm});
            skCircle(sketch, "E7.0.2.3", {"center": v(-70.18, -22.5) * mm, "radius": 3.18 * mm});
            skCircle(sketch, "E7.0.2.4", {"center": v(-39, -22.5) * mm, "radius": 3.18 * mm});
            skCircle(sketch, "E7.0.2.5", {"center": v(7.76, -22.5) * mm, "radius": 3.18 * mm});
            skCircle(sketch, "E7.0.2.6", {"center": v(124.68, -18) * mm, "radius": 3.18 * mm});
            skCircle(sketch, "E7.0.2.8", {"center": v(-132.53, -22.5) * mm, "radius": 3.18 * mm});
            skCircle(sketch, "E7.0.2.9", {"center": v(-101.36, -22.5) * mm, "radius": 3.18 * mm});
            skCircle(sketch, "E7.0.2.10", {"center": v(31.15, -18) * mm, "radius": 3.18 * mm});
            skCircle(sketch, "E7.0.2.11", {"center": v(101.3, -22.5) * mm, "radius": 3.18 * mm});
            skCircle(sketch, "E7.0.2.12", {"center": v(93.5, -18) * mm, "radius": 3.18 * mm});
            skCircle(sketch, "E7.0.2.13", {"center": v(62.32, -18) * mm, "radius": 3.18 * mm});
            skCircle(sketch, "E7.0.2.14", {"center": v(70.12, -22.5) * mm, "radius": 3.18 * mm});
            skCircle(sketch, "E7.0.2.15", {"center": v(38.94, -22.5) * mm, "radius": 3.18 * mm});
            skCircle(sketch, "E7.0.2.17", {"center": v(132.47, -22.5) * mm, "radius": 3.18 * mm});
            skCircle(sketch, "E7.0.2.18", {"center": v(85.7, -22.5) * mm, "radius": 3.18 * mm});
            skCircle(sketch, "E7.0.2.19", {"center": v(116.88, -22.5) * mm, "radius": 3.18 * mm});
            skCircle(sketch, "E7.0.2.21", {"center": v(46.73, -18) * mm, "radius": 3.18 * mm});
            skCircle(sketch, "E7.0.2.22", {"center": v(77.91, -18) * mm, "radius": 3.18 * mm});
            skCircle(sketch, "E7.0.2.23", {"center": v(109.09, -18) * mm, "radius": 3.18 * mm});
            skCircle(sketch, "E7.0.2.24", {"center": v(140.27, -18) * mm, "radius": 3.18 * mm});
            skCircle(sketch, "E7.0.2.25", {"center": v(-148.12, -22.5) * mm, "radius": 3.18 * mm});
            skCircle(sketch, "E7.0.2.26", {"center": v(-23.41, -22.5) * mm, "radius": 3.18 * mm});
            skCircle(sketch, "E7.0.2.27", {"center": v(-54.6, -22.5) * mm, "radius": 3.18 * mm});
            skCircle(sketch, "E7.0.2.28", {"center": v(-85.77, -22.5) * mm, "radius": 3.18 * mm});
            skCircle(sketch, "E7.0.2.29", {"center": v(-116.94, -22.5) * mm, "radius": 3.18 * mm});
            skLineSegment(sketch, "E7.0.2.30", {"start": v(-0.03, -18) * mm, "end": v(15.56, -18) * mm, "construction": true});
            skLineSegment(sketch, "E7.0.2.31", {"start": v(-0.03, -18) * mm, "end": v(-15.62, -18) * mm, "construction": true});
            skCircle(sketch, "E7.0.2.32", {"center": v(-31.2, -18) * mm, "radius": 3.18 * mm});
            skCircle(sketch, "E7.0.2.33", {"center": v(-155.92, -18) * mm, "radius": 3.18 * mm});
            skCircle(sketch, "E7.0.2.34", {"center": v(-62.38, -18) * mm, "radius": 3.18 * mm});
            skCircle(sketch, "E7.0.2.35", {"center": v(-140.33, -18) * mm, "radius": 3.18 * mm});
            skCircle(sketch, "E7.0.2.36", {"center": v(-77.97, -18) * mm, "radius": 3.18 * mm});
            skCircle(sketch, "E7.0.2.37", {"center": v(-46.8, -18) * mm, "radius": 3.18 * mm});
            skCircle(sketch, "E7.0.2.38", {"center": v(-109.15, -18) * mm, "radius": 3.18 * mm});
            skCircle(sketch, "E7.0.2.39", {"center": v(-124.74, -18) * mm, "radius": 3.18 * mm});
            skCircle(sketch, "E7.0.2.40", {"center": v(-93.56, -18) * mm, "radius": 3.18 * mm});
            skCircle(sketch, "E7.0.2.41", {"center": v(15.56, -18) * mm, "radius": 3.18 * mm});
            skCircle(sketch, "E7.0.2.42", {"center": v(-15.62, -18) * mm, "radius": 3.18 * mm});
            skCircle(sketch, "E7.0.2.43", {"center": v(-0.03, -18) * mm, "radius": 3.18 * mm});
            skCircle(sketch, "E7.0.3.0", {"center": v(54.51, -31.5) * mm, "radius": 3.18 * mm});
            skCircle(sketch, "E7.0.3.1", {"center": v(23.34, -31.5) * mm, "radius": 3.18 * mm});
            skCircle(sketch, "E7.0.3.2", {"center": v(-7.84, -31.5) * mm, "radius": 3.18 * mm});
            skCircle(sketch, "E7.0.3.3", {"center": v(-70.2, -31.5) * mm, "radius": 3.18 * mm});
            skCircle(sketch, "E7.0.3.4", {"center": v(-39.02, -31.5) * mm, "radius": 3.18 * mm});
            skCircle(sketch, "E7.0.3.5", {"center": v(7.75, -31.5) * mm, "radius": 3.18 * mm});
            skCircle(sketch, "E7.0.3.6", {"center": v(124.66, -27) * mm, "radius": 3.18 * mm});
            skCircle(sketch, "E7.0.3.8", {"center": v(-132.55, -31.5) * mm, "radius": 3.18 * mm});
            skCircle(sketch, "E7.0.3.9", {"center": v(-101.37, -31.5) * mm, "radius": 3.18 * mm});
            skCircle(sketch, "E7.0.3.10", {"center": v(31.13, -27) * mm, "radius": 3.18 * mm});
            skCircle(sketch, "E7.0.3.11", {"center": v(101.28, -31.5) * mm, "radius": 3.18 * mm});
            skCircle(sketch, "E7.0.3.12", {"center": v(93.48, -27) * mm, "radius": 3.18 * mm});
            skCircle(sketch, "E7.0.3.13", {"center": v(62.3, -27) * mm, "radius": 3.18 * mm});
            skCircle(sketch, "E7.0.3.14", {"center": v(70.1, -31.5) * mm, "radius": 3.18 * mm});
            skCircle(sketch, "E7.0.3.15", {"center": v(38.93, -31.5) * mm, "radius": 3.18 * mm});
            skCircle(sketch, "E7.0.3.17", {"center": v(132.46, -31.5) * mm, "radius": 3.18 * mm});
            skCircle(sketch, "E7.0.3.18", {"center": v(85.7, -31.5) * mm, "radius": 3.18 * mm});
            skCircle(sketch, "E7.0.3.19", {"center": v(116.87, -31.5) * mm, "radius": 3.18 * mm});
            skCircle(sketch, "E7.0.3.21", {"center": v(46.72, -27) * mm, "radius": 3.18 * mm});
            skCircle(sketch, "E7.0.3.22", {"center": v(77.9, -27) * mm, "radius": 3.18 * mm});
            skCircle(sketch, "E7.0.3.23", {"center": v(109.07, -27) * mm, "radius": 3.18 * mm});
            skCircle(sketch, "E7.0.3.24", {"center": v(140.25, -27) * mm, "radius": 3.18 * mm});
            skCircle(sketch, "E7.0.3.25", {"center": v(-148.14, -31.5) * mm, "radius": 3.18 * mm});
            skCircle(sketch, "E7.0.3.26", {"center": v(-23.43, -31.5) * mm, "radius": 3.18 * mm});
            skCircle(sketch, "E7.0.3.27", {"center": v(-54.6, -31.5) * mm, "radius": 3.18 * mm});
            skCircle(sketch, "E7.0.3.28", {"center": v(-85.78, -31.5) * mm, "radius": 3.18 * mm});
            skCircle(sketch, "E7.0.3.29", {"center": v(-116.96, -31.5) * mm, "radius": 3.18 * mm});
            skLineSegment(sketch, "E7.0.3.30", {"start": v(-0.05, -27) * mm, "end": v(15.54, -27) * mm, "construction": true});
            skLineSegment(sketch, "E7.0.3.31", {"start": v(-0.05, -27) * mm, "end": v(-15.63, -27) * mm, "construction": true});
            skCircle(sketch, "E7.0.3.32", {"center": v(-31.22, -27) * mm, "radius": 3.18 * mm});
            skCircle(sketch, "E7.0.3.33", {"center": v(-155.93, -27) * mm, "radius": 3.18 * mm});
            skCircle(sketch, "E7.0.3.34", {"center": v(-62.4, -27) * mm, "radius": 3.18 * mm});
            skCircle(sketch, "E7.0.3.35", {"center": v(-140.34, -27) * mm, "radius": 3.18 * mm});
            skCircle(sketch, "E7.0.3.36", {"center": v(-77.99, -27) * mm, "radius": 3.18 * mm});
            skCircle(sketch, "E7.0.3.37", {"center": v(-46.81, -27) * mm, "radius": 3.18 * mm});
            skCircle(sketch, "E7.0.3.38", {"center": v(-109.17, -27) * mm, "radius": 3.18 * mm});
            skCircle(sketch, "E7.0.3.39", {"center": v(-124.75, -27) * mm, "radius": 3.18 * mm});
            skCircle(sketch, "E7.0.3.40", {"center": v(-93.58, -27) * mm, "radius": 3.18 * mm});
            skCircle(sketch, "E7.0.3.41", {"center": v(15.54, -27) * mm, "radius": 3.18 * mm});
            skCircle(sketch, "E7.0.3.42", {"center": v(-15.63, -27) * mm, "radius": 3.18 * mm});
            skCircle(sketch, "E7.0.3.43", {"center": v(-0.05, -27) * mm, "radius": 3.18 * mm});
            skCircle(sketch, "E7.0.4.0", {"center": v(54.5, -40.5) * mm, "radius": 3.18 * mm});
            skCircle(sketch, "E7.0.4.1", {"center": v(23.32, -40.5) * mm, "radius": 3.18 * mm});
            skCircle(sketch, "E7.0.4.2", {"center": v(-7.86, -40.5) * mm, "radius": 3.18 * mm});
            skCircle(sketch, "E7.0.4.3", {"center": v(-70.2, -40.5) * mm, "radius": 3.18 * mm});
            skCircle(sketch, "E7.0.4.4", {"center": v(-39.03, -40.5) * mm, "radius": 3.18 * mm});
            skCircle(sketch, "E7.0.4.5", {"center": v(7.73, -40.5) * mm, "radius": 3.18 * mm});
            skCircle(sketch, "E7.0.4.6", {"center": v(124.65, -36) * mm, "radius": 3.18 * mm});
            skCircle(sketch, "E7.0.4.8", {"center": v(-132.56, -40.5) * mm, "radius": 3.18 * mm});
            skCircle(sketch, "E7.0.4.9", {"center": v(-101.39, -40.5) * mm, "radius": 3.18 * mm});
            skCircle(sketch, "E7.0.4.10", {"center": v(31.12, -36) * mm, "radius": 3.18 * mm});
            skCircle(sketch, "E7.0.4.11", {"center": v(101.26, -40.5) * mm, "radius": 3.18 * mm});
            skCircle(sketch, "E7.0.4.12", {"center": v(93.47, -36) * mm, "radius": 3.18 * mm});
            skCircle(sketch, "E7.0.4.13", {"center": v(62.3, -36) * mm, "radius": 3.18 * mm});
            skCircle(sketch, "E7.0.4.14", {"center": v(70.09, -40.5) * mm, "radius": 3.18 * mm});
            skCircle(sketch, "E7.0.4.15", {"center": v(38.91, -40.5) * mm, "radius": 3.18 * mm});
            skCircle(sketch, "E7.0.4.17", {"center": v(132.44, -40.5) * mm, "radius": 3.18 * mm});
            skCircle(sketch, "E7.0.4.18", {"center": v(85.68, -40.5) * mm, "radius": 3.18 * mm});
            skCircle(sketch, "E7.0.4.19", {"center": v(116.85, -40.5) * mm, "radius": 3.18 * mm});
            skCircle(sketch, "E7.0.4.21", {"center": v(46.7, -36) * mm, "radius": 3.18 * mm});
            skCircle(sketch, "E7.0.4.22", {"center": v(77.88, -36) * mm, "radius": 3.18 * mm});
            skCircle(sketch, "E7.0.4.23", {"center": v(109.06, -36) * mm, "radius": 3.18 * mm});
            skCircle(sketch, "E7.0.4.24", {"center": v(140.24, -36) * mm, "radius": 3.18 * mm});
            skCircle(sketch, "E7.0.4.25", {"center": v(-148.15, -40.5) * mm, "radius": 3.18 * mm});
            skCircle(sketch, "E7.0.4.26", {"center": v(-23.44, -40.5) * mm, "radius": 3.18 * mm});
            skCircle(sketch, "E7.0.4.27", {"center": v(-54.62, -40.5) * mm, "radius": 3.18 * mm});
            skCircle(sketch, "E7.0.4.28", {"center": v(-85.8, -40.5) * mm, "radius": 3.18 * mm});
            skCircle(sketch, "E7.0.4.29", {"center": v(-116.97, -40.5) * mm, "radius": 3.18 * mm});
            skLineSegment(sketch, "E7.0.4.30", {"start": v(-0.06, -36) * mm, "end": v(15.53, -36) * mm, "construction": true});
            skLineSegment(sketch, "E7.0.4.31", {"start": v(-0.06, -36) * mm, "end": v(-15.65, -36) * mm, "construction": true});
            skCircle(sketch, "E7.0.4.32", {"center": v(-31.24, -36) * mm, "radius": 3.18 * mm});
            skCircle(sketch, "E7.0.4.33", {"center": v(-155.95, -36) * mm, "radius": 3.18 * mm});
            skCircle(sketch, "E7.0.4.34", {"center": v(-62.41, -36) * mm, "radius": 3.18 * mm});
            skCircle(sketch, "E7.0.4.35", {"center": v(-140.36, -36) * mm, "radius": 3.18 * mm});
            skCircle(sketch, "E7.0.4.36", {"center": v(-78, -36) * mm, "radius": 3.18 * mm});
            skCircle(sketch, "E7.0.4.37", {"center": v(-46.83, -36) * mm, "radius": 3.18 * mm});
            skCircle(sketch, "E7.0.4.38", {"center": v(-109.18, -36) * mm, "radius": 3.18 * mm});
            skCircle(sketch, "E7.0.4.39", {"center": v(-124.77, -36) * mm, "radius": 3.18 * mm});
            skCircle(sketch, "E7.0.4.40", {"center": v(-93.6, -36) * mm, "radius": 3.18 * mm});
            skCircle(sketch, "E7.0.4.41", {"center": v(15.53, -36) * mm, "radius": 3.18 * mm});
            skCircle(sketch, "E7.0.4.42", {"center": v(-15.65, -36) * mm, "radius": 3.18 * mm});
            skCircle(sketch, "E7.0.4.43", {"center": v(-0.06, -36) * mm, "radius": 3.18 * mm});
            skCircle(sketch, "E7.0.5.0", {"center": v(54.48, -49.5) * mm, "radius": 3.18 * mm});
            skCircle(sketch, "E7.0.5.1", {"center": v(23.3, -49.5) * mm, "radius": 3.18 * mm});
            skCircle(sketch, "E7.0.5.2", {"center": v(-7.87, -49.5) * mm, "radius": 3.18 * mm});
            skCircle(sketch, "E7.0.5.3", {"center": v(-70.22, -49.5) * mm, "radius": 3.18 * mm});
            skCircle(sketch, "E7.0.5.4", {"center": v(-39.05, -49.5) * mm, "radius": 3.18 * mm});
            skCircle(sketch, "E7.0.5.5", {"center": v(7.72, -49.5) * mm, "radius": 3.18 * mm});
            skCircle(sketch, "E7.0.5.6", {"center": v(124.63, -45) * mm, "radius": 3.18 * mm});
            skCircle(sketch, "E7.0.5.8", {"center": v(-132.58, -49.5) * mm, "radius": 3.18 * mm});
            skCircle(sketch, "E7.0.5.9", {"center": v(-101.4, -49.5) * mm, "radius": 3.18 * mm});
            skCircle(sketch, "E7.0.5.10", {"center": v(31.1, -45) * mm, "radius": 3.18 * mm});
            skCircle(sketch, "E7.0.5.11", {"center": v(101.25, -49.5) * mm, "radius": 3.18 * mm});
            skCircle(sketch, "E7.0.5.12", {"center": v(93.45, -45) * mm, "radius": 3.18 * mm});
            skCircle(sketch, "E7.0.5.13", {"center": v(62.28, -45) * mm, "radius": 3.18 * mm});
            skCircle(sketch, "E7.0.5.14", {"center": v(70.07, -49.5) * mm, "radius": 3.18 * mm});
            skCircle(sketch, "E7.0.5.15", {"center": v(38.9, -49.5) * mm, "radius": 3.18 * mm});
            skCircle(sketch, "E7.0.5.17", {"center": v(132.43, -49.5) * mm, "radius": 3.18 * mm});
            skCircle(sketch, "E7.0.5.18", {"center": v(85.66, -49.5) * mm, "radius": 3.18 * mm});
            skCircle(sketch, "E7.0.5.19", {"center": v(116.84, -49.5) * mm, "radius": 3.18 * mm});
            skCircle(sketch, "E7.0.5.21", {"center": v(46.69, -45) * mm, "radius": 3.18 * mm});
            skCircle(sketch, "E7.0.5.22", {"center": v(77.87, -45) * mm, "radius": 3.18 * mm});
            skCircle(sketch, "E7.0.5.23", {"center": v(109.04, -45) * mm, "radius": 3.18 * mm});
            skCircle(sketch, "E7.0.5.24", {"center": v(140.22, -45) * mm, "radius": 3.18 * mm});
            skCircle(sketch, "E7.0.5.25", {"center": v(-148.17, -49.5) * mm, "radius": 3.18 * mm});
            skCircle(sketch, "E7.0.5.26", {"center": v(-23.46, -49.5) * mm, "radius": 3.18 * mm});
            skCircle(sketch, "E7.0.5.27", {"center": v(-54.64, -49.5) * mm, "radius": 3.18 * mm});
            skCircle(sketch, "E7.0.5.28", {"center": v(-85.81, -49.5) * mm, "radius": 3.18 * mm});
            skCircle(sketch, "E7.0.5.29", {"center": v(-116.99, -49.5) * mm, "radius": 3.18 * mm});
            skLineSegment(sketch, "E7.0.5.30", {"start": v(-0.08, -45) * mm, "end": v(15.51, -45) * mm, "construction": true});
            skLineSegment(sketch, "E7.0.5.31", {"start": v(-0.08, -45) * mm, "end": v(-15.66, -45) * mm, "construction": true});
            skCircle(sketch, "E7.0.5.32", {"center": v(-31.25, -45) * mm, "radius": 3.18 * mm});
            skCircle(sketch, "E7.0.5.33", {"center": v(-155.96, -45) * mm, "radius": 3.18 * mm});
            skCircle(sketch, "E7.0.5.34", {"center": v(-62.43, -45) * mm, "radius": 3.18 * mm});
            skCircle(sketch, "E7.0.5.35", {"center": v(-140.37, -45) * mm, "radius": 3.18 * mm});
            skCircle(sketch, "E7.0.5.36", {"center": v(-78.02, -45) * mm, "radius": 3.18 * mm});
            skCircle(sketch, "E7.0.5.37", {"center": v(-46.84, -45) * mm, "radius": 3.18 * mm});
            skCircle(sketch, "E7.0.5.38", {"center": v(-109.2, -45) * mm, "radius": 3.18 * mm});
            skCircle(sketch, "E7.0.5.39", {"center": v(-124.78, -45) * mm, "radius": 3.18 * mm});
            skCircle(sketch, "E7.0.5.40", {"center": v(-93.6, -45) * mm, "radius": 3.18 * mm});
            skCircle(sketch, "E7.0.5.41", {"center": v(15.51, -45) * mm, "radius": 3.18 * mm});
            skCircle(sketch, "E7.0.5.42", {"center": v(-15.66, -45) * mm, "radius": 3.18 * mm});
            skCircle(sketch, "E7.0.5.43", {"center": v(-0.08, -45) * mm, "radius": 3.18 * mm});
            skCircle(sketch, "E7.0.6.0", {"center": v(54.47, -58.5) * mm, "radius": 3.18 * mm});
            skCircle(sketch, "E7.0.6.1", {"center": v(23.3, -58.5) * mm, "radius": 3.18 * mm});
            skCircle(sketch, "E7.0.6.2", {"center": v(-7.89, -58.5) * mm, "radius": 3.18 * mm});
            skCircle(sketch, "E7.0.6.3", {"center": v(-70.24, -58.5) * mm, "radius": 3.18 * mm});
            skCircle(sketch, "E7.0.6.4", {"center": v(-39.06, -58.5) * mm, "radius": 3.18 * mm});
            skCircle(sketch, "E7.0.6.5", {"center": v(7.7, -58.5) * mm, "radius": 3.18 * mm});
            skCircle(sketch, "E7.0.6.6", {"center": v(124.62, -54) * mm, "radius": 3.18 * mm});
            skCircle(sketch, "E7.0.6.8", {"center": v(-132.6, -58.5) * mm, "radius": 3.18 * mm});
            skCircle(sketch, "E7.0.6.9", {"center": v(-101.42, -58.5) * mm, "radius": 3.18 * mm});
            skCircle(sketch, "E7.0.6.10", {"center": v(31.09, -54) * mm, "radius": 3.18 * mm});
            skCircle(sketch, "E7.0.6.11", {"center": v(101.23, -58.5) * mm, "radius": 3.18 * mm});
            skCircle(sketch, "E7.0.6.12", {"center": v(93.44, -54) * mm, "radius": 3.18 * mm});
            skCircle(sketch, "E7.0.6.13", {"center": v(62.26, -54) * mm, "radius": 3.18 * mm});
            skCircle(sketch, "E7.0.6.14", {"center": v(70.06, -58.5) * mm, "radius": 3.18 * mm});
            skCircle(sketch, "E7.0.6.15", {"center": v(38.88, -58.5) * mm, "radius": 3.18 * mm});
            skCircle(sketch, "E7.0.6.17", {"center": v(132.41, -58.5) * mm, "radius": 3.18 * mm});
            skCircle(sketch, "E7.0.6.18", {"center": v(85.64, -58.5) * mm, "radius": 3.18 * mm});
            skCircle(sketch, "E7.0.6.19", {"center": v(116.82, -58.5) * mm, "radius": 3.18 * mm});
            skCircle(sketch, "E7.0.6.21", {"center": v(46.67, -54) * mm, "radius": 3.18 * mm});
            skCircle(sketch, "E7.0.6.22", {"center": v(77.85, -54) * mm, "radius": 3.18 * mm});
            skCircle(sketch, "E7.0.6.23", {"center": v(109.03, -54) * mm, "radius": 3.18 * mm});
            skCircle(sketch, "E7.0.6.24", {"center": v(140.2, -54) * mm, "radius": 3.18 * mm});
            skCircle(sketch, "E7.0.6.25", {"center": v(-148.18, -58.5) * mm, "radius": 3.18 * mm});
            skCircle(sketch, "E7.0.6.26", {"center": v(-23.47, -58.5) * mm, "radius": 3.18 * mm});
            skCircle(sketch, "E7.0.6.27", {"center": v(-54.65, -58.5) * mm, "radius": 3.18 * mm});
            skCircle(sketch, "E7.0.6.28", {"center": v(-85.83, -58.5) * mm, "radius": 3.18 * mm});
            skCircle(sketch, "E7.0.6.29", {"center": v(-117, -58.5) * mm, "radius": 3.18 * mm});
            skLineSegment(sketch, "E7.0.6.30", {"start": v(-0.1, -54) * mm, "end": v(15.5, -54) * mm, "construction": true});
            skLineSegment(sketch, "E7.0.6.31", {"start": v(-0.1, -54) * mm, "end": v(-15.68, -54) * mm, "construction": true});
            skCircle(sketch, "E7.0.6.32", {"center": v(-31.27, -54) * mm, "radius": 3.18 * mm});
            skCircle(sketch, "E7.0.6.33", {"center": v(-155.98, -54) * mm, "radius": 3.18 * mm});
            skCircle(sketch, "E7.0.6.34", {"center": v(-62.45, -54) * mm, "radius": 3.18 * mm});
            skCircle(sketch, "E7.0.6.35", {"center": v(-140.39, -54) * mm, "radius": 3.18 * mm});
            skCircle(sketch, "E7.0.6.36", {"center": v(-78.03, -54) * mm, "radius": 3.18 * mm});
            skCircle(sketch, "E7.0.6.37", {"center": v(-46.86, -54) * mm, "radius": 3.18 * mm});
            skCircle(sketch, "E7.0.6.38", {"center": v(-109.21, -54) * mm, "radius": 3.18 * mm});
            skCircle(sketch, "E7.0.6.39", {"center": v(-124.8, -54) * mm, "radius": 3.18 * mm});
            skCircle(sketch, "E7.0.6.40", {"center": v(-93.62, -54) * mm, "radius": 3.18 * mm});
            skCircle(sketch, "E7.0.6.41", {"center": v(15.5, -54) * mm, "radius": 3.18 * mm});
            skCircle(sketch, "E7.0.6.42", {"center": v(-15.68, -54) * mm, "radius": 3.18 * mm});
            skCircle(sketch, "E7.0.6.43", {"center": v(-0.1, -54) * mm, "radius": 3.18 * mm});
            skCircle(sketch, "E7.0.7.0", {"center": v(54.45, -67.5) * mm, "radius": 3.18 * mm});
            skCircle(sketch, "E7.0.7.1", {"center": v(23.28, -67.5) * mm, "radius": 3.18 * mm});
            skCircle(sketch, "E7.0.7.2", {"center": v(-7.9, -67.5) * mm, "radius": 3.18 * mm});
            skCircle(sketch, "E7.0.7.3", {"center": v(-70.25, -67.5) * mm, "radius": 3.18 * mm});
            skCircle(sketch, "E7.0.7.4", {"center": v(-39.08, -67.5) * mm, "radius": 3.18 * mm});
            skCircle(sketch, "E7.0.7.5", {"center": v(7.69, -67.5) * mm, "radius": 3.18 * mm});
            skCircle(sketch, "E7.0.7.6", {"center": v(124.6, -63) * mm, "radius": 3.18 * mm});
            skCircle(sketch, "E7.0.7.8", {"center": v(-132.6, -67.5) * mm, "radius": 3.18 * mm});
            skCircle(sketch, "E7.0.7.9", {"center": v(-101.43, -67.5) * mm, "radius": 3.18 * mm});
            skCircle(sketch, "E7.0.7.10", {"center": v(31.07, -63) * mm, "radius": 3.18 * mm});
            skCircle(sketch, "E7.0.7.11", {"center": v(101.22, -67.5) * mm, "radius": 3.18 * mm});
            skCircle(sketch, "E7.0.7.12", {"center": v(93.42, -63) * mm, "radius": 3.18 * mm});
            skCircle(sketch, "E7.0.7.13", {"center": v(62.25, -63) * mm, "radius": 3.18 * mm});
            skCircle(sketch, "E7.0.7.14", {"center": v(70.04, -67.5) * mm, "radius": 3.18 * mm});
            skCircle(sketch, "E7.0.7.15", {"center": v(38.86, -67.5) * mm, "radius": 3.18 * mm});
            skCircle(sketch, "E7.0.7.18", {"center": v(85.63, -67.5) * mm, "radius": 3.18 * mm});
            skCircle(sketch, "E7.0.7.19", {"center": v(116.8, -67.5) * mm, "radius": 3.18 * mm});
            skCircle(sketch, "E7.0.7.21", {"center": v(46.66, -63) * mm, "radius": 3.18 * mm});
            skCircle(sketch, "E7.0.7.22", {"center": v(77.84, -63) * mm, "radius": 3.18 * mm});
            skCircle(sketch, "E7.0.7.23", {"center": v(109.01, -63) * mm, "radius": 3.18 * mm});
            skCircle(sketch, "E7.0.7.25", {"center": v(-148.2, -67.5) * mm, "radius": 3.18 * mm});
            skCircle(sketch, "E7.0.7.26", {"center": v(-23.49, -67.5) * mm, "radius": 3.18 * mm});
            skCircle(sketch, "E7.0.7.27", {"center": v(-54.67, -67.5) * mm, "radius": 3.18 * mm});
            skCircle(sketch, "E7.0.7.28", {"center": v(-85.84, -67.5) * mm, "radius": 3.18 * mm});
            skCircle(sketch, "E7.0.7.29", {"center": v(-117.02, -67.5) * mm, "radius": 3.18 * mm});
            skLineSegment(sketch, "E7.0.7.30", {"start": v(-0.1, -63) * mm, "end": v(15.48, -63) * mm, "construction": true});
            skLineSegment(sketch, "E7.0.7.31", {"start": v(-0.1, -63) * mm, "end": v(-15.7, -63) * mm, "construction": true});
            skCircle(sketch, "E7.0.7.32", {"center": v(-31.28, -63) * mm, "radius": 3.18 * mm});
            skCircle(sketch, "E7.0.7.33", {"center": v(-156, -63) * mm, "radius": 3.18 * mm});
            skCircle(sketch, "E7.0.7.34", {"center": v(-62.46, -63) * mm, "radius": 3.18 * mm});
            skCircle(sketch, "E7.0.7.35", {"center": v(-140.4, -63) * mm, "radius": 3.18 * mm});
            skCircle(sketch, "E7.0.7.36", {"center": v(-78.05, -63) * mm, "radius": 3.18 * mm});
            skCircle(sketch, "E7.0.7.37", {"center": v(-46.87, -63) * mm, "radius": 3.18 * mm});
            skCircle(sketch, "E7.0.7.38", {"center": v(-109.23, -63) * mm, "radius": 3.18 * mm});
            skCircle(sketch, "E7.0.7.39", {"center": v(-124.81, -63) * mm, "radius": 3.18 * mm});
            skCircle(sketch, "E7.0.7.40", {"center": v(-93.64, -63) * mm, "radius": 3.18 * mm});
            skCircle(sketch, "E7.0.7.41", {"center": v(15.48, -63) * mm, "radius": 3.18 * mm});
            skCircle(sketch, "E7.0.7.42", {"center": v(-15.7, -63) * mm, "radius": 3.18 * mm});
            skCircle(sketch, "E7.0.7.43", {"center": v(-0.1, -63) * mm, "radius": 3.18 * mm});
            skCircle(sketch, "E7.0.8.0", {"center": v(54.44, -76.5) * mm, "radius": 3.18 * mm});
            skCircle(sketch, "E7.0.8.1", {"center": v(23.26, -76.5) * mm, "radius": 3.18 * mm});
            skCircle(sketch, "E7.0.8.2", {"center": v(-7.92, -76.5) * mm, "radius": 3.18 * mm});
            skCircle(sketch, "E7.0.8.3", {"center": v(-70.27, -76.5) * mm, "radius": 3.18 * mm});
            skCircle(sketch, "E7.0.8.4", {"center": v(-39.1, -76.5) * mm, "radius": 3.18 * mm});
            skCircle(sketch, "E7.0.8.5", {"center": v(7.67, -76.5) * mm, "radius": 3.18 * mm});
            skCircle(sketch, "E7.0.8.6", {"center": v(124.59, -72) * mm, "radius": 3.18 * mm});
            skCircle(sketch, "E7.0.8.8", {"center": v(-132.62, -76.5) * mm, "radius": 3.18 * mm});
            skCircle(sketch, "E7.0.8.9", {"center": v(-101.45, -76.5) * mm, "radius": 3.18 * mm});
            skCircle(sketch, "E7.0.8.10", {"center": v(31.05, -72) * mm, "radius": 3.18 * mm});
            skCircle(sketch, "E7.0.8.11", {"center": v(101.2, -76.5) * mm, "radius": 3.18 * mm});
            skCircle(sketch, "E7.0.8.12", {"center": v(93.4, -72) * mm, "radius": 3.18 * mm});
            skCircle(sketch, "E7.0.8.13", {"center": v(62.23, -72) * mm, "radius": 3.18 * mm});
            skCircle(sketch, "E7.0.8.14", {"center": v(70.03, -76.5) * mm, "radius": 3.18 * mm});
            skCircle(sketch, "E7.0.8.15", {"center": v(38.85, -76.5) * mm, "radius": 3.18 * mm});
            skCircle(sketch, "E7.0.8.18", {"center": v(85.61, -76.5) * mm, "radius": 3.18 * mm});
            skCircle(sketch, "E7.0.8.19", {"center": v(116.8, -76.5) * mm, "radius": 3.18 * mm});
            skCircle(sketch, "E7.0.8.21", {"center": v(46.64, -72) * mm, "radius": 3.18 * mm});
            skCircle(sketch, "E7.0.8.22", {"center": v(77.82, -72) * mm, "radius": 3.18 * mm});
            skCircle(sketch, "E7.0.8.23", {"center": v(109, -72) * mm, "radius": 3.18 * mm});
            skCircle(sketch, "E7.0.8.25", {"center": v(-148.21, -76.5) * mm, "radius": 3.18 * mm});
            skCircle(sketch, "E7.0.8.26", {"center": v(-23.5, -76.5) * mm, "radius": 3.18 * mm});
            skCircle(sketch, "E7.0.8.27", {"center": v(-54.68, -76.5) * mm, "radius": 3.18 * mm});
            skCircle(sketch, "E7.0.8.28", {"center": v(-85.86, -76.5) * mm, "radius": 3.18 * mm});
            skCircle(sketch, "E7.0.8.29", {"center": v(-117.04, -76.5) * mm, "radius": 3.18 * mm});
            skLineSegment(sketch, "E7.0.8.30", {"start": v(-0.12, -72) * mm, "end": v(15.47, -72) * mm, "construction": true});
            skLineSegment(sketch, "E7.0.8.31", {"start": v(-0.12, -72) * mm, "end": v(-15.71, -72) * mm, "construction": true});
            skCircle(sketch, "E7.0.8.32", {"center": v(-31.3, -72) * mm, "radius": 3.18 * mm});
            skCircle(sketch, "E7.0.8.33", {"center": v(-156, -72) * mm, "radius": 3.18 * mm});
            skCircle(sketch, "E7.0.8.34", {"center": v(-62.48, -72) * mm, "radius": 3.18 * mm});
            skCircle(sketch, "E7.0.8.35", {"center": v(-140.42, -72) * mm, "radius": 3.18 * mm});
            skCircle(sketch, "E7.0.8.36", {"center": v(-78.06, -72) * mm, "radius": 3.18 * mm});
            skCircle(sketch, "E7.0.8.37", {"center": v(-46.89, -72) * mm, "radius": 3.18 * mm});
            skCircle(sketch, "E7.0.8.38", {"center": v(-109.24, -72) * mm, "radius": 3.18 * mm});
            skCircle(sketch, "E7.0.8.39", {"center": v(-124.83, -72) * mm, "radius": 3.18 * mm});
            skCircle(sketch, "E7.0.8.40", {"center": v(-93.65, -72) * mm, "radius": 3.18 * mm});
            skCircle(sketch, "E7.0.8.41", {"center": v(15.47, -72) * mm, "radius": 3.18 * mm});
            skCircle(sketch, "E7.0.8.42", {"center": v(-15.71, -72) * mm, "radius": 3.18 * mm});
            skCircle(sketch, "E7.0.8.43", {"center": v(-0.12, -72) * mm, "radius": 3.18 * mm});
            skCircle(sketch, "E7.0.9.0", {"center": v(54.42, -85.5) * mm, "radius": 3.18 * mm});
            skCircle(sketch, "E7.0.9.1", {"center": v(23.25, -85.5) * mm, "radius": 3.18 * mm});
            skCircle(sketch, "E7.0.9.2", {"center": v(-7.93, -85.5) * mm, "radius": 3.18 * mm});
            skCircle(sketch, "E7.0.9.3", {"center": v(-70.29, -85.5) * mm, "radius": 3.18 * mm});
            skCircle(sketch, "E7.0.9.4", {"center": v(-39.1, -85.5) * mm, "radius": 3.18 * mm});
            skCircle(sketch, "E7.0.9.5", {"center": v(7.66, -85.5) * mm, "radius": 3.18 * mm});
            skCircle(sketch, "E7.0.9.8", {"center": v(-132.64, -85.5) * mm, "radius": 3.18 * mm});
            skCircle(sketch, "E7.0.9.9", {"center": v(-101.46, -85.5) * mm, "radius": 3.18 * mm});
            skCircle(sketch, "E7.0.9.10", {"center": v(31.04, -81) * mm, "radius": 3.18 * mm});
            skCircle(sketch, "E7.0.9.11", {"center": v(101.19, -85.5) * mm, "radius": 3.18 * mm});
            skCircle(sketch, "E7.0.9.12", {"center": v(93.4, -81) * mm, "radius": 3.18 * mm});
            skCircle(sketch, "E7.0.9.13", {"center": v(62.22, -81) * mm, "radius": 3.18 * mm});
            skCircle(sketch, "E7.0.9.14", {"center": v(70.01, -85.5) * mm, "radius": 3.18 * mm});
            skCircle(sketch, "E7.0.9.15", {"center": v(38.83, -85.5) * mm, "radius": 3.18 * mm});
            skCircle(sketch, "E7.0.9.18", {"center": v(85.6, -85.5) * mm, "radius": 3.18 * mm});
            skCircle(sketch, "E7.0.9.19", {"center": v(116.78, -85.5) * mm, "radius": 3.18 * mm});
            skCircle(sketch, "E7.0.9.21", {"center": v(46.63, -81) * mm, "radius": 3.18 * mm});
            skCircle(sketch, "E7.0.9.22", {"center": v(77.8, -81) * mm, "radius": 3.18 * mm});
            skCircle(sketch, "E7.0.9.23", {"center": v(108.98, -81) * mm, "radius": 3.18 * mm});
            skCircle(sketch, "E7.0.9.25", {"center": v(-148.23, -85.5) * mm, "radius": 3.18 * mm});
            skCircle(sketch, "E7.0.9.26", {"center": v(-23.52, -85.5) * mm, "radius": 3.18 * mm});
            skCircle(sketch, "E7.0.9.27", {"center": v(-54.7, -85.5) * mm, "radius": 3.18 * mm});
            skCircle(sketch, "E7.0.9.28", {"center": v(-85.87, -85.5) * mm, "radius": 3.18 * mm});
            skCircle(sketch, "E7.0.9.29", {"center": v(-117.05, -85.5) * mm, "radius": 3.18 * mm});
            skLineSegment(sketch, "E7.0.9.30", {"start": v(-0.14, -81) * mm, "end": v(15.45, -81) * mm, "construction": true});
            skLineSegment(sketch, "E7.0.9.31", {"start": v(-0.14, -81) * mm, "end": v(-15.73, -81) * mm, "construction": true});
            skCircle(sketch, "E7.0.9.32", {"center": v(-31.31, -81) * mm, "radius": 3.18 * mm});
            skCircle(sketch, "E7.0.9.33", {"center": v(-156.02, -81) * mm, "radius": 3.18 * mm});
            skCircle(sketch, "E7.0.9.34", {"center": v(-62.5, -81) * mm, "radius": 3.18 * mm});
            skCircle(sketch, "E7.0.9.35", {"center": v(-140.43, -81) * mm, "radius": 3.18 * mm});
            skCircle(sketch, "E7.0.9.36", {"center": v(-78.08, -81) * mm, "radius": 3.18 * mm});
            skCircle(sketch, "E7.0.9.37", {"center": v(-46.9, -81) * mm, "radius": 3.18 * mm});
            skCircle(sketch, "E7.0.9.38", {"center": v(-109.26, -81) * mm, "radius": 3.18 * mm});
            skCircle(sketch, "E7.0.9.39", {"center": v(-124.85, -81) * mm, "radius": 3.18 * mm});
            skCircle(sketch, "E7.0.9.40", {"center": v(-93.67, -81) * mm, "radius": 3.18 * mm});
            skCircle(sketch, "E7.0.9.41", {"center": v(15.45, -81) * mm, "radius": 3.18 * mm});
            skCircle(sketch, "E7.0.9.42", {"center": v(-15.73, -81) * mm, "radius": 3.18 * mm});
            skCircle(sketch, "E7.0.9.43", {"center": v(-0.14, -81) * mm, "radius": 3.18 * mm});
            skCircle(sketch, "E7.0.10.0", {"center": v(54.4, -94.5) * mm, "radius": 3.18 * mm});
            skCircle(sketch, "E7.0.10.1", {"center": v(23.23, -94.5) * mm, "radius": 3.18 * mm});
            skCircle(sketch, "E7.0.10.2", {"center": v(-7.95, -94.5) * mm, "radius": 3.18 * mm});
            skCircle(sketch, "E7.0.10.3", {"center": v(-70.3, -94.5) * mm, "radius": 3.18 * mm});
            skCircle(sketch, "E7.0.10.4", {"center": v(-39.12, -94.5) * mm, "radius": 3.18 * mm});
            skCircle(sketch, "E7.0.10.5", {"center": v(7.64, -94.5) * mm, "radius": 3.18 * mm});
            skCircle(sketch, "E7.0.10.8", {"center": v(-132.65, -94.5) * mm, "radius": 3.18 * mm});
            skCircle(sketch, "E7.0.10.9", {"center": v(-101.48, -94.5) * mm, "radius": 3.18 * mm});
            skCircle(sketch, "E7.0.10.10", {"center": v(31.02, -90) * mm, "radius": 3.18 * mm});
            skCircle(sketch, "E7.0.10.11", {"center": v(101.17, -94.5) * mm, "radius": 3.18 * mm});
            skCircle(sketch, "E7.0.10.12", {"center": v(93.38, -90) * mm, "radius": 3.18 * mm});
            skCircle(sketch, "E7.0.10.13", {"center": v(62.2, -90) * mm, "radius": 3.18 * mm});
            skCircle(sketch, "E7.0.10.14", {"center": v(70, -94.5) * mm, "radius": 3.18 * mm});
            skCircle(sketch, "E7.0.10.15", {"center": v(38.82, -94.5) * mm, "radius": 3.18 * mm});
            skCircle(sketch, "E7.0.10.18", {"center": v(85.58, -94.5) * mm, "radius": 3.18 * mm});
            skCircle(sketch, "E7.0.10.21", {"center": v(46.61, -90) * mm, "radius": 3.18 * mm});
            skCircle(sketch, "E7.0.10.22", {"center": v(77.79, -90) * mm, "radius": 3.18 * mm});
            skCircle(sketch, "E7.0.10.23", {"center": v(108.97, -90) * mm, "radius": 3.18 * mm});
            skCircle(sketch, "E7.0.10.25", {"center": v(-148.24, -94.5) * mm, "radius": 3.18 * mm});
            skCircle(sketch, "E7.0.10.26", {"center": v(-23.54, -94.5) * mm, "radius": 3.18 * mm});
            skCircle(sketch, "E7.0.10.27", {"center": v(-54.71, -94.5) * mm, "radius": 3.18 * mm});
            skCircle(sketch, "E7.0.10.28", {"center": v(-85.89, -94.5) * mm, "radius": 3.18 * mm});
            skCircle(sketch, "E7.0.10.29", {"center": v(-117.07, -94.5) * mm, "radius": 3.18 * mm});
            skLineSegment(sketch, "E7.0.10.30", {"start": v(-0.15, -90) * mm, "end": v(15.44, -90) * mm, "construction": true});
            skLineSegment(sketch, "E7.0.10.31", {"start": v(-0.15, -90) * mm, "end": v(-15.74, -90) * mm, "construction": true});
            skCircle(sketch, "E7.0.10.32", {"center": v(-31.33, -90) * mm, "radius": 3.18 * mm});
            skCircle(sketch, "E7.0.10.33", {"center": v(-156.04, -90) * mm, "radius": 3.18 * mm});
            skCircle(sketch, "E7.0.10.34", {"center": v(-62.5, -90) * mm, "radius": 3.18 * mm});
            skCircle(sketch, "E7.0.10.35", {"center": v(-140.45, -90) * mm, "radius": 3.18 * mm});
            skCircle(sketch, "E7.0.10.36", {"center": v(-78.1, -90) * mm, "radius": 3.18 * mm});
            skCircle(sketch, "E7.0.10.37", {"center": v(-46.92, -90) * mm, "radius": 3.18 * mm});
            skCircle(sketch, "E7.0.10.38", {"center": v(-109.27, -90) * mm, "radius": 3.18 * mm});
            skCircle(sketch, "E7.0.10.39", {"center": v(-124.86, -90) * mm, "radius": 3.18 * mm});
            skCircle(sketch, "E7.0.10.40", {"center": v(-93.68, -90) * mm, "radius": 3.18 * mm});
            skCircle(sketch, "E7.0.10.41", {"center": v(15.44, -90) * mm, "radius": 3.18 * mm});
            skCircle(sketch, "E7.0.10.42", {"center": v(-15.74, -90) * mm, "radius": 3.18 * mm});
            skCircle(sketch, "E7.0.10.43", {"center": v(-0.15, -90) * mm, "radius": 3.18 * mm});
            skCircle(sketch, "E7.0.11.0", {"center": v(54.4, -103.5) * mm, "radius": 3.18 * mm});
            skCircle(sketch, "E7.0.11.1", {"center": v(23.21, -103.5) * mm, "radius": 3.18 * mm});
            skCircle(sketch, "E7.0.11.2", {"center": v(-7.96, -103.5) * mm, "radius": 3.18 * mm});
            skCircle(sketch, "E7.0.11.3", {"center": v(-70.32, -103.5) * mm, "radius": 3.18 * mm});
            skCircle(sketch, "E7.0.11.4", {"center": v(-39.14, -103.5) * mm, "radius": 3.18 * mm});
            skCircle(sketch, "E7.0.11.5", {"center": v(7.63, -103.5) * mm, "radius": 3.18 * mm});
            skCircle(sketch, "E7.0.11.8", {"center": v(-132.67, -103.5) * mm, "radius": 3.18 * mm});
            skCircle(sketch, "E7.0.11.9", {"center": v(-101.5, -103.5) * mm, "radius": 3.18 * mm});
            skCircle(sketch, "E7.0.11.10", {"center": v(31, -99) * mm, "radius": 3.18 * mm});
            skCircle(sketch, "E7.0.11.11", {"center": v(101.16, -103.5) * mm, "radius": 3.18 * mm});
            skCircle(sketch, "E7.0.11.12", {"center": v(93.36, -99) * mm, "radius": 3.18 * mm});
            skCircle(sketch, "E7.0.11.13", {"center": v(62.19, -99) * mm, "radius": 3.18 * mm});
            skCircle(sketch, "E7.0.11.14", {"center": v(69.98, -103.5) * mm, "radius": 3.18 * mm});
            skCircle(sketch, "E7.0.11.15", {"center": v(38.8, -103.5) * mm, "radius": 3.18 * mm});
            skCircle(sketch, "E7.0.11.18", {"center": v(85.57, -103.5) * mm, "radius": 3.18 * mm});
            skCircle(sketch, "E7.0.11.21", {"center": v(46.6, -99) * mm, "radius": 3.18 * mm});
            skCircle(sketch, "E7.0.11.22", {"center": v(77.77, -99) * mm, "radius": 3.18 * mm});
            skCircle(sketch, "E7.0.11.23", {"center": v(108.95, -99) * mm, "radius": 3.18 * mm});
            skCircle(sketch, "E7.0.11.25", {"center": v(-148.26, -103.5) * mm, "radius": 3.18 * mm});
            skCircle(sketch, "E7.0.11.26", {"center": v(-23.55, -103.5) * mm, "radius": 3.18 * mm});
            skCircle(sketch, "E7.0.11.27", {"center": v(-54.73, -103.5) * mm, "radius": 3.18 * mm});
            skCircle(sketch, "E7.0.11.28", {"center": v(-85.9, -103.5) * mm, "radius": 3.18 * mm});
            skCircle(sketch, "E7.0.11.29", {"center": v(-117.08, -103.5) * mm, "radius": 3.18 * mm});
            skLineSegment(sketch, "E7.0.11.30", {"start": v(-0.17, -99) * mm, "end": v(15.42, -99) * mm, "construction": true});
            skLineSegment(sketch, "E7.0.11.31", {"start": v(-0.17, -99) * mm, "end": v(-15.76, -99) * mm, "construction": true});
            skCircle(sketch, "E7.0.11.32", {"center": v(-31.34, -99) * mm, "radius": 3.18 * mm});
            skCircle(sketch, "E7.0.11.33", {"center": v(-156.05, -99) * mm, "radius": 3.18 * mm});
            skCircle(sketch, "E7.0.11.34", {"center": v(-62.52, -99) * mm, "radius": 3.18 * mm});
            skCircle(sketch, "E7.0.11.35", {"center": v(-140.46, -99) * mm, "radius": 3.18 * mm});
            skCircle(sketch, "E7.0.11.36", {"center": v(-78.11, -99) * mm, "radius": 3.18 * mm});
            skCircle(sketch, "E7.0.11.37", {"center": v(-46.93, -99) * mm, "radius": 3.18 * mm});
            skCircle(sketch, "E7.0.11.38", {"center": v(-109.29, -99) * mm, "radius": 3.18 * mm});
            skCircle(sketch, "E7.0.11.39", {"center": v(-124.88, -99) * mm, "radius": 3.18 * mm});
            skCircle(sketch, "E7.0.11.40", {"center": v(-93.7, -99) * mm, "radius": 3.18 * mm});
            skCircle(sketch, "E7.0.11.41", {"center": v(15.42, -99) * mm, "radius": 3.18 * mm});
            skCircle(sketch, "E7.0.11.42", {"center": v(-15.76, -99) * mm, "radius": 3.18 * mm});
            skCircle(sketch, "E7.0.11.43", {"center": v(-0.17, -99) * mm, "radius": 3.18 * mm});
            skCircle(sketch, "E7.0.12.0", {"center": v(54.38, -112.5) * mm, "radius": 3.18 * mm});
            skCircle(sketch, "E7.0.12.1", {"center": v(23.2, -112.5) * mm, "radius": 3.18 * mm});
            skCircle(sketch, "E7.0.12.2", {"center": v(-7.98, -112.5) * mm, "radius": 3.18 * mm});
            skCircle(sketch, "E7.0.12.3", {"center": v(-70.33, -112.5) * mm, "radius": 3.18 * mm});
            skCircle(sketch, "E7.0.12.4", {"center": v(-39.15, -112.5) * mm, "radius": 3.18 * mm});
            skCircle(sketch, "E7.0.12.5", {"center": v(7.61, -112.5) * mm, "radius": 3.18 * mm});
            skCircle(sketch, "E7.0.12.8", {"center": v(-132.69, -112.5) * mm, "radius": 3.18 * mm});
            skCircle(sketch, "E7.0.12.9", {"center": v(-101.5, -112.5) * mm, "radius": 3.18 * mm});
            skCircle(sketch, "E7.0.12.10", {"center": v(31, -108) * mm, "radius": 3.18 * mm});
            skCircle(sketch, "E7.0.12.11", {"center": v(101.14, -112.5) * mm, "radius": 3.18 * mm});
            skCircle(sketch, "E7.0.12.12", {"center": v(93.35, -108) * mm, "radius": 3.18 * mm});
            skCircle(sketch, "E7.0.12.13", {"center": v(62.17, -108) * mm, "radius": 3.18 * mm});
            skCircle(sketch, "E7.0.12.14", {"center": v(69.96, -112.5) * mm, "radius": 3.18 * mm});
            skCircle(sketch, "E7.0.12.15", {"center": v(38.79, -112.5) * mm, "radius": 3.18 * mm});
            skCircle(sketch, "E7.0.12.18", {"center": v(85.55, -112.5) * mm, "radius": 3.18 * mm});
            skCircle(sketch, "E7.0.12.21", {"center": v(46.58, -108) * mm, "radius": 3.18 * mm});
            skCircle(sketch, "E7.0.12.22", {"center": v(77.76, -108) * mm, "radius": 3.18 * mm});
            skCircle(sketch, "E7.0.12.25", {"center": v(-148.27, -112.5) * mm, "radius": 3.18 * mm});
            skCircle(sketch, "E7.0.12.26", {"center": v(-23.57, -112.5) * mm, "radius": 3.18 * mm});
            skCircle(sketch, "E7.0.12.27", {"center": v(-54.74, -112.5) * mm, "radius": 3.18 * mm});
            skCircle(sketch, "E7.0.12.28", {"center": v(-85.92, -112.5) * mm, "radius": 3.18 * mm});
            skCircle(sketch, "E7.0.12.29", {"center": v(-117.1, -112.5) * mm, "radius": 3.18 * mm});
            skLineSegment(sketch, "E7.0.12.30", {"start": v(-0.18, -108) * mm, "end": v(15.4, -108) * mm, "construction": true});
            skLineSegment(sketch, "E7.0.12.31", {"start": v(-0.18, -108) * mm, "end": v(-15.77, -108) * mm, "construction": true});
            skCircle(sketch, "E7.0.12.32", {"center": v(-31.36, -108) * mm, "radius": 3.18 * mm});
            skCircle(sketch, "E7.0.12.33", {"center": v(-156.07, -108) * mm, "radius": 3.18 * mm});
            skCircle(sketch, "E7.0.12.34", {"center": v(-62.54, -108) * mm, "radius": 3.18 * mm});
            skCircle(sketch, "E7.0.12.35", {"center": v(-140.48, -108) * mm, "radius": 3.18 * mm});
            skCircle(sketch, "E7.0.12.36", {"center": v(-78.13, -108) * mm, "radius": 3.18 * mm});
            skCircle(sketch, "E7.0.12.37", {"center": v(-46.95, -108) * mm, "radius": 3.18 * mm});
            skCircle(sketch, "E7.0.12.38", {"center": v(-109.3, -108) * mm, "radius": 3.18 * mm});
            skCircle(sketch, "E7.0.12.39", {"center": v(-124.9, -108) * mm, "radius": 3.18 * mm});
            skCircle(sketch, "E7.0.12.40", {"center": v(-93.71, -108) * mm, "radius": 3.18 * mm});
            skCircle(sketch, "E7.0.12.41", {"center": v(15.4, -108) * mm, "radius": 3.18 * mm});
            skCircle(sketch, "E7.0.12.42", {"center": v(-15.77, -108) * mm, "radius": 3.18 * mm});
            skCircle(sketch, "E7.0.12.43", {"center": v(-0.18, -108) * mm, "radius": 3.18 * mm});
            skCircle(sketch, "E7.0.13.0", {"center": v(54.36, -121.5) * mm, "radius": 3.18 * mm});
            skCircle(sketch, "E7.0.13.1", {"center": v(23.18, -121.5) * mm, "radius": 3.18 * mm});
            skCircle(sketch, "E7.0.13.2", {"center": v(-8, -121.5) * mm, "radius": 3.18 * mm});
            skCircle(sketch, "E7.0.13.3", {"center": v(-70.35, -121.5) * mm, "radius": 3.18 * mm});
            skCircle(sketch, "E7.0.13.4", {"center": v(-39.17, -121.5) * mm, "radius": 3.18 * mm});
            skCircle(sketch, "E7.0.13.5", {"center": v(7.6, -121.5) * mm, "radius": 3.18 * mm});
            skCircle(sketch, "E7.0.13.8", {"center": v(-132.7, -121.5) * mm, "radius": 3.18 * mm});
            skCircle(sketch, "E7.0.13.9", {"center": v(-101.52, -121.5) * mm, "radius": 3.18 * mm});
            skCircle(sketch, "E7.0.13.10", {"center": v(30.98, -117) * mm, "radius": 3.18 * mm});
            skCircle(sketch, "E7.0.13.11", {"center": v(101.13, -121.5) * mm, "radius": 3.18 * mm});
            skCircle(sketch, "E7.0.13.12", {"center": v(93.33, -117) * mm, "radius": 3.18 * mm});
            skCircle(sketch, "E7.0.13.13", {"center": v(62.16, -117) * mm, "radius": 3.18 * mm});
            skCircle(sketch, "E7.0.13.14", {"center": v(69.95, -121.5) * mm, "radius": 3.18 * mm});
            skCircle(sketch, "E7.0.13.15", {"center": v(38.77, -121.5) * mm, "radius": 3.18 * mm});
            skCircle(sketch, "E7.0.13.18", {"center": v(85.54, -121.5) * mm, "radius": 3.18 * mm});
            skCircle(sketch, "E7.0.13.21", {"center": v(46.57, -117) * mm, "radius": 3.18 * mm});
            skCircle(sketch, "E7.0.13.22", {"center": v(77.74, -117) * mm, "radius": 3.18 * mm});
            skCircle(sketch, "E7.0.13.25", {"center": v(-148.29, -121.5) * mm, "radius": 3.18 * mm});
            skCircle(sketch, "E7.0.13.26", {"center": v(-23.58, -121.5) * mm, "radius": 3.18 * mm});
            skCircle(sketch, "E7.0.13.27", {"center": v(-54.76, -121.5) * mm, "radius": 3.18 * mm});
            skCircle(sketch, "E7.0.13.28", {"center": v(-85.94, -121.5) * mm, "radius": 3.18 * mm});
            skCircle(sketch, "E7.0.13.29", {"center": v(-117.11, -121.5) * mm, "radius": 3.18 * mm});
            skLineSegment(sketch, "E7.0.13.30", {"start": v(-0.2, -117) * mm, "end": v(15.39, -117) * mm, "construction": true});
            skLineSegment(sketch, "E7.0.13.31", {"start": v(-0.2, -117) * mm, "end": v(-15.79, -117) * mm, "construction": true});
            skCircle(sketch, "E7.0.13.32", {"center": v(-31.38, -117) * mm, "radius": 3.18 * mm});
            skCircle(sketch, "E7.0.13.33", {"center": v(-156.08, -117) * mm, "radius": 3.18 * mm});
            skCircle(sketch, "E7.0.13.34", {"center": v(-62.55, -117) * mm, "radius": 3.18 * mm});
            skCircle(sketch, "E7.0.13.35", {"center": v(-140.5, -117) * mm, "radius": 3.18 * mm});
            skCircle(sketch, "E7.0.13.36", {"center": v(-78.14, -117) * mm, "radius": 3.18 * mm});
            skCircle(sketch, "E7.0.13.37", {"center": v(-46.96, -117) * mm, "radius": 3.18 * mm});
            skCircle(sketch, "E7.0.13.38", {"center": v(-109.32, -117) * mm, "radius": 3.18 * mm});
            skCircle(sketch, "E7.0.13.39", {"center": v(-124.9, -117) * mm, "radius": 3.18 * mm});
            skCircle(sketch, "E7.0.13.40", {"center": v(-93.73, -117) * mm, "radius": 3.18 * mm});
            skCircle(sketch, "E7.0.13.41", {"center": v(15.39, -117) * mm, "radius": 3.18 * mm});
            skCircle(sketch, "E7.0.13.42", {"center": v(-15.79, -117) * mm, "radius": 3.18 * mm});
            skCircle(sketch, "E7.0.13.43", {"center": v(-0.2, -117) * mm, "radius": 3.18 * mm});
            skCircle(sketch, "E7.0.14.0", {"center": v(54.35, -130.5) * mm, "radius": 3.18 * mm});
            skCircle(sketch, "E7.0.14.1", {"center": v(23.17, -130.5) * mm, "radius": 3.18 * mm});
            skCircle(sketch, "E7.0.14.2", {"center": v(-8, -130.5) * mm, "radius": 3.18 * mm});
            skCircle(sketch, "E7.0.14.3", {"center": v(-70.36, -130.5) * mm, "radius": 3.18 * mm});
            skCircle(sketch, "E7.0.14.4", {"center": v(-39.18, -130.5) * mm, "radius": 3.18 * mm});
            skCircle(sketch, "E7.0.14.5", {"center": v(7.58, -130.5) * mm, "radius": 3.18 * mm});
            skCircle(sketch, "E7.0.14.8", {"center": v(-132.72, -130.5) * mm, "radius": 3.18 * mm});
            skCircle(sketch, "E7.0.14.9", {"center": v(-101.54, -130.5) * mm, "radius": 3.18 * mm});
            skCircle(sketch, "E7.0.14.10", {"center": v(30.96, -126) * mm, "radius": 3.18 * mm});
            skCircle(sketch, "E7.0.14.11", {"center": v(101.11, -130.5) * mm, "radius": 3.18 * mm});
            skCircle(sketch, "E7.0.14.12", {"center": v(93.32, -126) * mm, "radius": 3.18 * mm});
            skCircle(sketch, "E7.0.14.13", {"center": v(62.14, -126) * mm, "radius": 3.18 * mm});
            skCircle(sketch, "E7.0.14.14", {"center": v(69.93, -130.5) * mm, "radius": 3.18 * mm});
            skCircle(sketch, "E7.0.14.15", {"center": v(38.76, -130.5) * mm, "radius": 3.18 * mm});
            skCircle(sketch, "E7.0.14.18", {"center": v(85.52, -130.5) * mm, "radius": 3.18 * mm});
            skCircle(sketch, "E7.0.14.21", {"center": v(46.55, -126) * mm, "radius": 3.18 * mm});
            skCircle(sketch, "E7.0.14.22", {"center": v(77.73, -126) * mm, "radius": 3.18 * mm});
            skCircle(sketch, "E7.0.14.25", {"center": v(-148.3, -130.5) * mm, "radius": 3.18 * mm});
            skCircle(sketch, "E7.0.14.26", {"center": v(-23.6, -130.5) * mm, "radius": 3.18 * mm});
            skCircle(sketch, "E7.0.14.27", {"center": v(-54.77, -130.5) * mm, "radius": 3.18 * mm});
            skCircle(sketch, "E7.0.14.28", {"center": v(-85.95, -130.5) * mm, "radius": 3.18 * mm});
            skCircle(sketch, "E7.0.14.29", {"center": v(-117.13, -130.5) * mm, "radius": 3.18 * mm});
            skLineSegment(sketch, "E7.0.14.30", {"start": v(-0.21, -126) * mm, "end": v(15.37, -126) * mm, "construction": true});
            skLineSegment(sketch, "E7.0.14.31", {"start": v(-0.21, -126) * mm, "end": v(-15.8, -126) * mm, "construction": true});
            skCircle(sketch, "E7.0.14.32", {"center": v(-31.4, -126) * mm, "radius": 3.18 * mm});
            skCircle(sketch, "E7.0.14.33", {"center": v(-156.1, -126) * mm, "radius": 3.18 * mm});
            skCircle(sketch, "E7.0.14.34", {"center": v(-62.57, -126) * mm, "radius": 3.18 * mm});
            skCircle(sketch, "E7.0.14.35", {"center": v(-140.5, -126) * mm, "radius": 3.18 * mm});
            skCircle(sketch, "E7.0.14.36", {"center": v(-78.16, -126) * mm, "radius": 3.18 * mm});
            skCircle(sketch, "E7.0.14.37", {"center": v(-46.98, -126) * mm, "radius": 3.18 * mm});
            skCircle(sketch, "E7.0.14.38", {"center": v(-109.33, -126) * mm, "radius": 3.18 * mm});
            skCircle(sketch, "E7.0.14.39", {"center": v(-124.92, -126) * mm, "radius": 3.18 * mm});
            skCircle(sketch, "E7.0.14.40", {"center": v(-93.74, -126) * mm, "radius": 3.18 * mm});
            skCircle(sketch, "E7.0.14.41", {"center": v(15.37, -126) * mm, "radius": 3.18 * mm});
            skCircle(sketch, "E7.0.14.42", {"center": v(-15.8, -126) * mm, "radius": 3.18 * mm});
            skCircle(sketch, "E7.0.14.43", {"center": v(-0.21, -126) * mm, "radius": 3.18 * mm});
            skCircle(sketch, "E7.0.15.0", {"center": v(54.33, -139.5) * mm, "radius": 3.18 * mm});
            skCircle(sketch, "E7.0.15.1", {"center": v(23.15, -139.5) * mm, "radius": 3.18 * mm});
            skCircle(sketch, "E7.0.15.2", {"center": v(-8.02, -139.5) * mm, "radius": 3.18 * mm});
            skCircle(sketch, "E7.0.15.3", {"center": v(-70.38, -139.5) * mm, "radius": 3.18 * mm});
            skCircle(sketch, "E7.0.15.4", {"center": v(-39.2, -139.5) * mm, "radius": 3.18 * mm});
            skCircle(sketch, "E7.0.15.5", {"center": v(7.57, -139.5) * mm, "radius": 3.18 * mm});
            skCircle(sketch, "E7.0.15.8", {"center": v(-132.73, -139.5) * mm, "radius": 3.18 * mm});
            skCircle(sketch, "E7.0.15.9", {"center": v(-101.55, -139.5) * mm, "radius": 3.18 * mm});
            skCircle(sketch, "E7.0.15.10", {"center": v(30.95, -135) * mm, "radius": 3.18 * mm});
            skCircle(sketch, "E7.0.15.11", {"center": v(101.1, -139.5) * mm, "radius": 3.18 * mm});
            skCircle(sketch, "E7.0.15.12", {"center": v(93.3, -135) * mm, "radius": 3.18 * mm});
            skCircle(sketch, "E7.0.15.13", {"center": v(62.12, -135) * mm, "radius": 3.18 * mm});
            skCircle(sketch, "E7.0.15.14", {"center": v(69.92, -139.5) * mm, "radius": 3.18 * mm});
            skCircle(sketch, "E7.0.15.15", {"center": v(38.74, -139.5) * mm, "radius": 3.18 * mm});
            skCircle(sketch, "E7.0.15.18", {"center": v(85.5, -139.5) * mm, "radius": 3.18 * mm});
            skCircle(sketch, "E7.0.15.21", {"center": v(46.54, -135) * mm, "radius": 3.18 * mm});
            skCircle(sketch, "E7.0.15.22", {"center": v(77.71, -135) * mm, "radius": 3.18 * mm});
            skCircle(sketch, "E7.0.15.25", {"center": v(-148.32, -139.5) * mm, "radius": 3.18 * mm});
            skCircle(sketch, "E7.0.15.26", {"center": v(-23.61, -139.5) * mm, "radius": 3.18 * mm});
            skCircle(sketch, "E7.0.15.27", {"center": v(-54.79, -139.5) * mm, "radius": 3.18 * mm});
            skCircle(sketch, "E7.0.15.28", {"center": v(-85.97, -139.5) * mm, "radius": 3.18 * mm});
            skCircle(sketch, "E7.0.15.29", {"center": v(-117.14, -139.5) * mm, "radius": 3.18 * mm});
            skLineSegment(sketch, "E7.0.15.30", {"start": v(-0.23, -135) * mm, "end": v(15.36, -135) * mm, "construction": true});
            skLineSegment(sketch, "E7.0.15.31", {"start": v(-0.23, -135) * mm, "end": v(-15.82, -135) * mm, "construction": true});
            skCircle(sketch, "E7.0.15.32", {"center": v(-31.4, -135) * mm, "radius": 3.18 * mm});
            skCircle(sketch, "E7.0.15.33", {"center": v(-156.11, -135) * mm, "radius": 3.18 * mm});
            skCircle(sketch, "E7.0.15.34", {"center": v(-62.58, -135) * mm, "radius": 3.18 * mm});
            skCircle(sketch, "E7.0.15.35", {"center": v(-140.53, -135) * mm, "radius": 3.18 * mm});
            skCircle(sketch, "E7.0.15.36", {"center": v(-78.17, -135) * mm, "radius": 3.18 * mm});
            skCircle(sketch, "E7.0.15.37", {"center": v(-47, -135) * mm, "radius": 3.18 * mm});
            skCircle(sketch, "E7.0.15.38", {"center": v(-109.35, -135) * mm, "radius": 3.18 * mm});
            skCircle(sketch, "E7.0.15.39", {"center": v(-124.94, -135) * mm, "radius": 3.18 * mm});
            skCircle(sketch, "E7.0.15.40", {"center": v(-93.76, -135) * mm, "radius": 3.18 * mm});
            skCircle(sketch, "E7.0.15.41", {"center": v(15.36, -135) * mm, "radius": 3.18 * mm});
            skCircle(sketch, "E7.0.15.42", {"center": v(-15.82, -135) * mm, "radius": 3.18 * mm});
            skCircle(sketch, "E7.0.15.43", {"center": v(-0.23, -135) * mm, "radius": 3.18 * mm});
            skCircle(sketch, "E7.0.16.0", {"center": v(54.32, -148.5) * mm, "radius": 3.18 * mm});
            skCircle(sketch, "E7.0.16.1", {"center": v(23.14, -148.5) * mm, "radius": 3.18 * mm});
            skCircle(sketch, "E7.0.16.2", {"center": v(-8.04, -148.5) * mm, "radius": 3.18 * mm});
            skCircle(sketch, "E7.0.16.3", {"center": v(-70.4, -148.5) * mm, "radius": 3.18 * mm});
            skCircle(sketch, "E7.0.16.4", {"center": v(-39.22, -148.5) * mm, "radius": 3.18 * mm});
            skCircle(sketch, "E7.0.16.5", {"center": v(7.55, -148.5) * mm, "radius": 3.18 * mm});
            skCircle(sketch, "E7.0.16.8", {"center": v(-132.75, -148.5) * mm, "radius": 3.18 * mm});
            skCircle(sketch, "E7.0.16.9", {"center": v(-101.57, -148.5) * mm, "radius": 3.18 * mm});
            skCircle(sketch, "E7.0.16.10", {"center": v(30.93, -144) * mm, "radius": 3.18 * mm});
            skCircle(sketch, "E7.0.16.11", {"center": v(101.08, -148.5) * mm, "radius": 3.18 * mm});
            skCircle(sketch, "E7.0.16.12", {"center": v(93.29, -144) * mm, "radius": 3.18 * mm});
            skCircle(sketch, "E7.0.16.13", {"center": v(62.1, -144) * mm, "radius": 3.18 * mm});
            skCircle(sketch, "E7.0.16.14", {"center": v(69.9, -148.5) * mm, "radius": 3.18 * mm});
            skCircle(sketch, "E7.0.16.15", {"center": v(38.73, -148.5) * mm, "radius": 3.18 * mm});
            skCircle(sketch, "E7.0.16.18", {"center": v(85.5, -148.5) * mm, "radius": 3.18 * mm});
            skCircle(sketch, "E7.0.16.21", {"center": v(46.52, -144) * mm, "radius": 3.18 * mm});
            skCircle(sketch, "E7.0.16.22", {"center": v(77.7, -144) * mm, "radius": 3.18 * mm});
            skCircle(sketch, "E7.0.16.25", {"center": v(-148.33, -148.5) * mm, "radius": 3.18 * mm});
            skCircle(sketch, "E7.0.16.26", {"center": v(-23.63, -148.5) * mm, "radius": 3.18 * mm});
            skCircle(sketch, "E7.0.16.27", {"center": v(-54.8, -148.5) * mm, "radius": 3.18 * mm});
            skCircle(sketch, "E7.0.16.28", {"center": v(-85.98, -148.5) * mm, "radius": 3.18 * mm});
            skCircle(sketch, "E7.0.16.29", {"center": v(-117.16, -148.5) * mm, "radius": 3.18 * mm});
            skLineSegment(sketch, "E7.0.16.30", {"start": v(-0.24, -144) * mm, "end": v(15.34, -144) * mm, "construction": true});
            skLineSegment(sketch, "E7.0.16.31", {"start": v(-0.24, -144) * mm, "end": v(-15.83, -144) * mm, "construction": true});
            skCircle(sketch, "E7.0.16.32", {"center": v(-31.42, -144) * mm, "radius": 3.18 * mm});
            skCircle(sketch, "E7.0.16.33", {"center": v(-156.13, -144) * mm, "radius": 3.18 * mm});
            skCircle(sketch, "E7.0.16.34", {"center": v(-62.6, -144) * mm, "radius": 3.18 * mm});
            skCircle(sketch, "E7.0.16.35", {"center": v(-140.54, -144) * mm, "radius": 3.18 * mm});
            skCircle(sketch, "E7.0.16.36", {"center": v(-78.19, -144) * mm, "radius": 3.18 * mm});
            skCircle(sketch, "E7.0.16.37", {"center": v(-47, -144) * mm, "radius": 3.18 * mm});
            skCircle(sketch, "E7.0.16.38", {"center": v(-109.36, -144) * mm, "radius": 3.18 * mm});
            skCircle(sketch, "E7.0.16.39", {"center": v(-124.95, -144) * mm, "radius": 3.18 * mm});
            skCircle(sketch, "E7.0.16.40", {"center": v(-93.78, -144) * mm, "radius": 3.18 * mm});
            skCircle(sketch, "E7.0.16.41", {"center": v(15.34, -144) * mm, "radius": 3.18 * mm});
            skCircle(sketch, "E7.0.16.42", {"center": v(-15.83, -144) * mm, "radius": 3.18 * mm});
            skCircle(sketch, "E7.0.16.43", {"center": v(-0.24, -144) * mm, "radius": 3.18 * mm});
            skCircle(sketch, "E7.0.17.0", {"center": v(54.3, -157.5) * mm, "radius": 3.18 * mm});
            skCircle(sketch, "E7.0.17.1", {"center": v(23.12, -157.5) * mm, "radius": 3.18 * mm});
            skCircle(sketch, "E7.0.17.2", {"center": v(-8.05, -157.5) * mm, "radius": 3.18 * mm});
            skCircle(sketch, "E7.0.17.3", {"center": v(-70.4, -157.5) * mm, "radius": 3.18 * mm});
            skCircle(sketch, "E7.0.17.4", {"center": v(-39.23, -157.5) * mm, "radius": 3.18 * mm});
            skCircle(sketch, "E7.0.17.5", {"center": v(7.53, -157.5) * mm, "radius": 3.18 * mm});
            skCircle(sketch, "E7.0.17.8", {"center": v(-132.76, -157.5) * mm, "radius": 3.18 * mm});
            skCircle(sketch, "E7.0.17.9", {"center": v(-101.58, -157.5) * mm, "radius": 3.18 * mm});
            skCircle(sketch, "E7.0.17.10", {"center": v(30.92, -153) * mm, "radius": 3.18 * mm});
            skCircle(sketch, "E7.0.17.11", {"center": v(101.07, -157.5) * mm, "radius": 3.18 * mm});
            skCircle(sketch, "E7.0.17.12", {"center": v(93.27, -153) * mm, "radius": 3.18 * mm});
            skCircle(sketch, "E7.0.17.13", {"center": v(62.1, -153) * mm, "radius": 3.18 * mm});
            skCircle(sketch, "E7.0.17.14", {"center": v(69.89, -157.5) * mm, "radius": 3.18 * mm});
            skCircle(sketch, "E7.0.17.15", {"center": v(38.71, -157.5) * mm, "radius": 3.18 * mm});
            skCircle(sketch, "E7.0.17.18", {"center": v(85.48, -157.5) * mm, "radius": 3.18 * mm});
            skCircle(sketch, "E7.0.17.21", {"center": v(46.5, -153) * mm, "radius": 3.18 * mm});
            skCircle(sketch, "E7.0.17.22", {"center": v(77.68, -153) * mm, "radius": 3.18 * mm});
            skCircle(sketch, "E7.0.17.25", {"center": v(-148.35, -157.5) * mm, "radius": 3.18 * mm});
            skCircle(sketch, "E7.0.17.26", {"center": v(-23.64, -157.5) * mm, "radius": 3.18 * mm});
            skCircle(sketch, "E7.0.17.27", {"center": v(-54.82, -157.5) * mm, "radius": 3.18 * mm});
            skCircle(sketch, "E7.0.17.28", {"center": v(-86, -157.5) * mm, "radius": 3.18 * mm});
            skCircle(sketch, "E7.0.17.29", {"center": v(-117.17, -157.5) * mm, "radius": 3.18 * mm});
            skLineSegment(sketch, "E7.0.17.30", {"start": v(-0.26, -153) * mm, "end": v(15.33, -153) * mm, "construction": true});
            skLineSegment(sketch, "E7.0.17.31", {"start": v(-0.26, -153) * mm, "end": v(-15.85, -153) * mm, "construction": true});
            skCircle(sketch, "E7.0.17.32", {"center": v(-31.44, -153) * mm, "radius": 3.18 * mm});
            skCircle(sketch, "E7.0.17.33", {"center": v(-156.14, -153) * mm, "radius": 3.18 * mm});
            skCircle(sketch, "E7.0.17.34", {"center": v(-62.61, -153) * mm, "radius": 3.18 * mm});
            skCircle(sketch, "E7.0.17.35", {"center": v(-140.56, -153) * mm, "radius": 3.18 * mm});
            skCircle(sketch, "E7.0.17.36", {"center": v(-78.2, -153) * mm, "radius": 3.18 * mm});
            skCircle(sketch, "E7.0.17.37", {"center": v(-47.03, -153) * mm, "radius": 3.18 * mm});
            skCircle(sketch, "E7.0.17.38", {"center": v(-109.38, -153) * mm, "radius": 3.18 * mm});
            skCircle(sketch, "E7.0.17.39", {"center": v(-124.97, -153) * mm, "radius": 3.18 * mm});
            skCircle(sketch, "E7.0.17.40", {"center": v(-93.8, -153) * mm, "radius": 3.18 * mm});
            skCircle(sketch, "E7.0.17.41", {"center": v(15.33, -153) * mm, "radius": 3.18 * mm});
            skCircle(sketch, "E7.0.17.42", {"center": v(-15.85, -153) * mm, "radius": 3.18 * mm});
            skCircle(sketch, "E7.0.17.43", {"center": v(-0.26, -153) * mm, "radius": 3.18 * mm});
            skLineSegment(sketch, "E7.direction1", {"start": v(-155.88, 0) * mm, "end": v(-130.88, 0) * mm, "construction": true});
            skLineSegment(sketch, "E7.direction2", {"start": v(-155.88, 0) * mm, "end": v(-155.9, -9) * mm, "construction": true});
            skSolve(sketch);
        }
        {
            var Q0;
            Q0=makeQuery(id+"F0.imprint","IMPRINT",FACE,{"disambiguationData":[TD([[makeQuery(id+"F0.imprint","IMPRINT",EDGE,{"derivedFrom":sQuery(id+"F0.wireOp",EDGE,"E1")}),-1.0]])]});
            extrude(context, id + "F1", {"entities" : qUnion([Q0]), "depth" : 25 * mm, "offsetDistance" : 25 * mm});
        }
        {
            var Q0;
            Q0=makeQuery(id+"F1.opExtrude","CAP_FACE",FACE,{"disambiguationData":[OSD([sQuery(id+"F0.wireOp",EDGE,"E0"),sQuery(id+"F0.wireOp",EDGE,"E1"),sQuery(id+"F0.wireOp",EDGE,"E2"),sQuery(id+"F0.wireOp",EDGE,"E3"),sQuery(id+"F0.wireOp",EDGE,"E4"),sQuery(id+"F0.wireOp",EDGE,"E5.0.1.0"),sQuery(id+"F0.wireOp",EDGE,"E5.0.1.1"),sQuery(id+"F0.wireOp",EDGE,"E5.0.1.2"),sQuery(id+"F0.wireOp",EDGE,"E5.0.1.3"),sQuery(id+"F0.wireOp",EDGE,"E5.0.2.0"),sQuery(id+"F0.wireOp",EDGE,"E5.0.2.1"),sQuery(id+"F0.wireOp",EDGE,"E5.0.2.2"),sQuery(id+"F0.wireOp",EDGE,"E5.0.2.3"),sQuery(id+"F0.wireOp",EDGE,"E5.0.3.0"),sQuery(id+"F0.wireOp",EDGE,"E5.0.3.1"),sQuery(id+"F0.wireOp",EDGE,"E5.0.3.2"),sQuery(id+"F0.wireOp",EDGE,"E5.0.3.3"),sQuery(id+"F0.wireOp",EDGE,"E5.0.4.0"),sQuery(id+"F0.wireOp",EDGE,"E5.0.4.1"),sQuery(id+"F0.wireOp",EDGE,"E5.0.4.2"),sQuery(id+"F0.wireOp",EDGE,"E5.0.4.3"),sQuery(id+"F0.wireOp",EDGE,"E5.0.5.0"),sQuery(id+"F0.wireOp",EDGE,"E5.0.5.1"),sQuery(id+"F0.wireOp",EDGE,"E5.0.5.2"),sQuery(id+"F0.wireOp",EDGE,"E5.0.5.3"),sQuery(id+"F0.wireOp",EDGE,"E5.0.6.0"),sQuery(id+"F0.wireOp",EDGE,"E5.0.6.1"),sQuery(id+"F0.wireOp",EDGE,"E5.0.6.2"),sQuery(id+"F0.wireOp",EDGE,"E5.0.6.3"),sQuery(id+"F0.wireOp",EDGE,"E5.0.7.0"),sQuery(id+"F0.wireOp",EDGE,"E5.0.7.1"),sQuery(id+"F0.wireOp",EDGE,"E5.0.7.2"),sQuery(id+"F0.wireOp",EDGE,"E5.0.7.3"),sQuery(id+"F0.wireOp",EDGE,"E5.0.8.1"),sQuery(id+"F0.wireOp",EDGE,"E5.0.8.2"),sQuery(id+"F0.wireOp",EDGE,"E5.1.0.0"),sQuery(id+"F0.wireOp",EDGE,"E5.1.0.1"),sQuery(id+"F0.wireOp",EDGE,"E5.1.0.2"),sQuery(id+"F0.wireOp",EDGE,"E5.1.0.3"),sQuery(id+"F0.wireOp",EDGE,"E5.1.1.0"),sQuery(id+"F0.wireOp",EDGE,"E5.1.1.1"),sQuery(id+"F0.wireOp",EDGE,"E5.1.1.2"),sQuery(id+"F0.wireOp",EDGE,"E5.1.1.3"),sQuery(id+"F0.wireOp",EDGE,"E5.1.2.0"),sQuery(id+"F0.wireOp",EDGE,"E5.1.2.1"),sQuery(id+"F0.wireOp",EDGE,"E5.1.2.2"),sQuery(id+"F0.wireOp",EDGE,"E5.1.2.3"),sQuery(id+"F0.wireOp",EDGE,"E5.1.3.0"),sQuery(id+"F0.wireOp",EDGE,"E5.1.3.1"),sQuery(id+"F0.wireOp",EDGE,"E5.1.3.2"),sQuery(id+"F0.wireOp",EDGE,"E5.1.3.3"),sQuery(id+"F0.wireOp",EDGE,"E5.1.4.0"),sQuery(id+"F0.wireOp",EDGE,"E5.1.4.1"),sQuery(id+"F0.wireOp",EDGE,"E5.1.4.2"),sQuery(id+"F0.wireOp",EDGE,"E5.1.4.3"),sQuery(id+"F0.wireOp",EDGE,"E5.1.5.0"),sQuery(id+"F0.wireOp",EDGE,"E5.1.5.1"),sQuery(id+"F0.wireOp",EDGE,"E5.1.5.2"),sQuery(id+"F0.wireOp",EDGE,"E5.1.5.3"),sQuery(id+"F0.wireOp",EDGE,"E5.1.6.0"),sQuery(id+"F0.wireOp",EDGE,"E5.1.6.1"),sQuery(id+"F0.wireOp",EDGE,"E5.1.6.2"),sQuery(id+"F0.wireOp",EDGE,"E5.1.6.3"),sQuery(id+"F0.wireOp",EDGE,"E5.1.7.0"),sQuery(id+"F0.wireOp",EDGE,"E5.1.7.1"),sQuery(id+"F0.wireOp",EDGE,"E5.1.7.2"),sQuery(id+"F0.wireOp",EDGE,"E5.1.7.3"),sQuery(id+"F0.wireOp",EDGE,"E5.1.8.1"),sQuery(id+"F0.wireOp",EDGE,"E5.1.8.2"),sQuery(id+"F0.wireOp",EDGE,"E5.2.0.0"),sQuery(id+"F0.wireOp",EDGE,"E5.2.0.1"),sQuery(id+"F0.wireOp",EDGE,"E5.2.0.2"),sQuery(id+"F0.wireOp",EDGE,"E5.2.0.3"),sQuery(id+"F0.wireOp",EDGE,"E5.2.1.0"),sQuery(id+"F0.wireOp",EDGE,"E5.2.1.1"),sQuery(id+"F0.wireOp",EDGE,"E5.2.1.2"),sQuery(id+"F0.wireOp",EDGE,"E5.2.1.3"),sQuery(id+"F0.wireOp",EDGE,"E5.2.2.0"),sQuery(id+"F0.wireOp",EDGE,"E5.2.2.1"),sQuery(id+"F0.wireOp",EDGE,"E5.2.2.2"),sQuery(id+"F0.wireOp",EDGE,"E5.2.2.3"),sQuery(id+"F0.wireOp",EDGE,"E5.2.3.0"),sQuery(id+"F0.wireOp",EDGE,"E5.2.3.1"),sQuery(id+"F0.wireOp",EDGE,"E5.2.3.2"),sQuery(id+"F0.wireOp",EDGE,"E5.2.3.3"),sQuery(id+"F0.wireOp",EDGE,"E5.2.4.0"),sQuery(id+"F0.wireOp",EDGE,"E5.2.4.1"),sQuery(id+"F0.wireOp",EDGE,"E5.2.4.2"),sQuery(id+"F0.wireOp",EDGE,"E5.2.4.3"),sQuery(id+"F0.wireOp",EDGE,"E5.2.5.0"),sQuery(id+"F0.wireOp",EDGE,"E5.2.5.1"),sQuery(id+"F0.wireOp",EDGE,"E5.2.5.2"),sQuery(id+"F0.wireOp",EDGE,"E5.2.5.3"),sQuery(id+"F0.wireOp",EDGE,"E5.2.6.0"),sQuery(id+"F0.wireOp",EDGE,"E5.2.6.1"),sQuery(id+"F0.wireOp",EDGE,"E5.2.6.2"),sQuery(id+"F0.wireOp",EDGE,"E5.2.6.3"),sQuery(id+"F0.wireOp",EDGE,"E5.2.7.0"),sQuery(id+"F0.wireOp",EDGE,"E5.2.7.1"),sQuery(id+"F0.wireOp",EDGE,"E5.2.7.2"),sQuery(id+"F0.wireOp",EDGE,"E5.2.7.3"),sQuery(id+"F0.wireOp",EDGE,"E5.2.8.1"),sQuery(id+"F0.wireOp",EDGE,"E5.2.8.2"),sQuery(id+"F0.wireOp",EDGE,"E5.3.0.0"),sQuery(id+"F0.wireOp",EDGE,"E5.3.0.1"),sQuery(id+"F0.wireOp",EDGE,"E5.3.0.2"),sQuery(id+"F0.wireOp",EDGE,"E5.3.0.3"),sQuery(id+"F0.wireOp",EDGE,"E5.3.1.0"),sQuery(id+"F0.wireOp",EDGE,"E5.3.1.1"),sQuery(id+"F0.wireOp",EDGE,"E5.3.1.2"),sQuery(id+"F0.wireOp",EDGE,"E5.3.1.3"),sQuery(id+"F0.wireOp",EDGE,"E5.3.2.0"),sQuery(id+"F0.wireOp",EDGE,"E5.3.2.1"),sQuery(id+"F0.wireOp",EDGE,"E5.3.2.2"),sQuery(id+"F0.wireOp",EDGE,"E5.3.2.3"),sQuery(id+"F0.wireOp",EDGE,"E5.3.3.0"),sQuery(id+"F0.wireOp",EDGE,"E5.3.3.1"),sQuery(id+"F0.wireOp",EDGE,"E5.3.3.2"),sQuery(id+"F0.wireOp",EDGE,"E5.3.3.3"),sQuery(id+"F0.wireOp",EDGE,"E5.3.4.0"),sQuery(id+"F0.wireOp",EDGE,"E5.3.4.1"),sQuery(id+"F0.wireOp",EDGE,"E5.3.4.2"),sQuery(id+"F0.wireOp",EDGE,"E5.3.4.3"),sQuery(id+"F0.wireOp",EDGE,"E5.3.5.0"),sQuery(id+"F0.wireOp",EDGE,"E5.3.5.1"),sQuery(id+"F0.wireOp",EDGE,"E5.3.5.2"),sQuery(id+"F0.wireOp",EDGE,"E5.3.5.3"),sQuery(id+"F0.wireOp",EDGE,"E5.3.6.0"),sQuery(id+"F0.wireOp",EDGE,"E5.3.6.1"),sQuery(id+"F0.wireOp",EDGE,"E5.3.6.2"),sQuery(id+"F0.wireOp",EDGE,"E5.3.6.3"),sQuery(id+"F0.wireOp",EDGE,"E5.3.7.0"),sQuery(id+"F0.wireOp",EDGE,"E5.3.7.1"),sQuery(id+"F0.wireOp",EDGE,"E5.3.7.2"),sQuery(id+"F0.wireOp",EDGE,"E5.3.7.3"),sQuery(id+"F0.wireOp",EDGE,"E5.4.0.0"),sQuery(id+"F0.wireOp",EDGE,"E5.4.0.1"),sQuery(id+"F0.wireOp",EDGE,"E5.4.0.2"),sQuery(id+"F0.wireOp",EDGE,"E5.4.0.3"),sQuery(id+"F0.wireOp",EDGE,"E5.4.1.0"),sQuery(id+"F0.wireOp",EDGE,"E5.4.1.1"),sQuery(id+"F0.wireOp",EDGE,"E5.4.1.2"),sQuery(id+"F0.wireOp",EDGE,"E5.4.1.3"),sQuery(id+"F0.wireOp",EDGE,"E5.4.2.0"),sQuery(id+"F0.wireOp",EDGE,"E5.4.2.1"),sQuery(id+"F0.wireOp",EDGE,"E5.4.2.2"),sQuery(id+"F0.wireOp",EDGE,"E5.4.2.3"),sQuery(id+"F0.wireOp",EDGE,"E5.4.3.0"),sQuery(id+"F0.wireOp",EDGE,"E5.4.3.1"),sQuery(id+"F0.wireOp",EDGE,"E5.4.3.2"),sQuery(id+"F0.wireOp",EDGE,"E5.4.3.3"),sQuery(id+"F0.wireOp",EDGE,"E5.4.4.0"),sQuery(id+"F0.wireOp",EDGE,"E5.4.4.1"),sQuery(id+"F0.wireOp",EDGE,"E5.4.4.2"),sQuery(id+"F0.wireOp",EDGE,"E5.4.4.3"),sQuery(id+"F0.wireOp",EDGE,"E5.4.5.0"),sQuery(id+"F0.wireOp",EDGE,"E5.4.5.1"),sQuery(id+"F0.wireOp",EDGE,"E5.4.5.2"),sQuery(id+"F0.wireOp",EDGE,"E5.4.5.3"),sQuery(id+"F0.wireOp",EDGE,"E5.4.6.0"),sQuery(id+"F0.wireOp",EDGE,"E5.4.6.1"),sQuery(id+"F0.wireOp",EDGE,"E5.4.6.2"),sQuery(id+"F0.wireOp",EDGE,"E5.4.6.3"),sQuery(id+"F0.wireOp",EDGE,"E5.4.7.1"),sQuery(id+"F0.wireOp",EDGE,"E5.4.7.2"),sQuery(id+"F0.wireOp",EDGE,"E5.5.0.0"),sQuery(id+"F0.wireOp",EDGE,"E5.5.0.1"),sQuery(id+"F0.wireOp",EDGE,"E5.5.0.2"),sQuery(id+"F0.wireOp",EDGE,"E5.5.0.3"),sQuery(id+"F0.wireOp",EDGE,"E5.5.1.0"),sQuery(id+"F0.wireOp",EDGE,"E5.5.1.1"),sQuery(id+"F0.wireOp",EDGE,"E5.5.1.2"),sQuery(id+"F0.wireOp",EDGE,"E5.5.1.3"),sQuery(id+"F0.wireOp",EDGE,"E5.5.2.0"),sQuery(id+"F0.wireOp",EDGE,"E5.5.2.1"),sQuery(id+"F0.wireOp",EDGE,"E5.5.2.2"),sQuery(id+"F0.wireOp",EDGE,"E5.5.2.3"),sQuery(id+"F0.wireOp",EDGE,"E5.5.3.0"),sQuery(id+"F0.wireOp",EDGE,"E5.5.3.1"),sQuery(id+"F0.wireOp",EDGE,"E5.5.3.2"),sQuery(id+"F0.wireOp",EDGE,"E5.5.3.3"),sQuery(id+"F0.wireOp",EDGE,"E5.5.4.0"),sQuery(id+"F0.wireOp",EDGE,"E5.5.4.1"),sQuery(id+"F0.wireOp",EDGE,"E5.5.4.2"),sQuery(id+"F0.wireOp",EDGE,"E5.5.4.3"),sQuery(id+"F0.wireOp",EDGE,"E5.5.5.0"),sQuery(id+"F0.wireOp",EDGE,"E5.5.5.1"),sQuery(id+"F0.wireOp",EDGE,"E5.5.5.2"),sQuery(id+"F0.wireOp",EDGE,"E5.5.5.3"),sQuery(id+"F0.wireOp",EDGE,"E5.5.6.0"),sQuery(id+"F0.wireOp",EDGE,"E5.5.6.1"),sQuery(id+"F0.wireOp",EDGE,"E5.5.6.2"),sQuery(id+"F0.wireOp",EDGE,"E5.5.6.3"),sQuery(id+"F0.wireOp",EDGE,"E5.6.0.0"),sQuery(id+"F0.wireOp",EDGE,"E5.6.0.1"),sQuery(id+"F0.wireOp",EDGE,"E5.6.0.2"),sQuery(id+"F0.wireOp",EDGE,"E5.6.0.3"),sQuery(id+"F0.wireOp",EDGE,"E5.6.1.0"),sQuery(id+"F0.wireOp",EDGE,"E5.6.1.1"),sQuery(id+"F0.wireOp",EDGE,"E5.6.1.2"),sQuery(id+"F0.wireOp",EDGE,"E5.6.1.3"),sQuery(id+"F0.wireOp",EDGE,"E5.6.2.0"),sQuery(id+"F0.wireOp",EDGE,"E5.6.2.1"),sQuery(id+"F0.wireOp",EDGE,"E5.6.2.2"),sQuery(id+"F0.wireOp",EDGE,"E5.6.2.3"),sQuery(id+"F0.wireOp",EDGE,"E5.6.3.0"),sQuery(id+"F0.wireOp",EDGE,"E5.6.3.1"),sQuery(id+"F0.wireOp",EDGE,"E5.6.3.2"),sQuery(id+"F0.wireOp",EDGE,"E5.6.3.3"),sQuery(id+"F0.wireOp",EDGE,"E5.6.4.0"),sQuery(id+"F0.wireOp",EDGE,"E5.6.4.1"),sQuery(id+"F0.wireOp",EDGE,"E5.6.4.2"),sQuery(id+"F0.wireOp",EDGE,"E5.6.4.3"),sQuery(id+"F0.wireOp",EDGE,"E5.6.5.0"),sQuery(id+"F0.wireOp",EDGE,"E5.6.5.1"),sQuery(id+"F0.wireOp",EDGE,"E5.6.5.2"),sQuery(id+"F0.wireOp",EDGE,"E5.6.5.3"),sQuery(id+"F0.wireOp",EDGE,"E5.6.6.1"),sQuery(id+"F0.wireOp",EDGE,"E5.6.6.2"),sQuery(id+"F0.wireOp",EDGE,"E5.7.0.0"),sQuery(id+"F0.wireOp",EDGE,"E5.7.0.1"),sQuery(id+"F0.wireOp",EDGE,"E5.7.0.2"),sQuery(id+"F0.wireOp",EDGE,"E5.7.0.3"),sQuery(id+"F0.wireOp",EDGE,"E5.7.1.0"),sQuery(id+"F0.wireOp",EDGE,"E5.7.1.1"),sQuery(id+"F0.wireOp",EDGE,"E5.7.1.2"),sQuery(id+"F0.wireOp",EDGE,"E5.7.1.3"),sQuery(id+"F0.wireOp",EDGE,"E5.7.2.0"),sQuery(id+"F0.wireOp",EDGE,"E5.7.2.1"),sQuery(id+"F0.wireOp",EDGE,"E5.7.2.2"),sQuery(id+"F0.wireOp",EDGE,"E5.7.2.3"),sQuery(id+"F0.wireOp",EDGE,"E5.7.3.0"),sQuery(id+"F0.wireOp",EDGE,"E5.7.3.1"),sQuery(id+"F0.wireOp",EDGE,"E5.7.3.2"),sQuery(id+"F0.wireOp",EDGE,"E5.7.3.3"),sQuery(id+"F0.wireOp",EDGE,"E5.7.4.0"),sQuery(id+"F0.wireOp",EDGE,"E5.7.4.1"),sQuery(id+"F0.wireOp",EDGE,"E5.7.4.2"),sQuery(id+"F0.wireOp",EDGE,"E5.7.4.3"),sQuery(id+"F0.wireOp",EDGE,"E5.7.5.1"),sQuery(id+"F0.wireOp",EDGE,"E5.7.5.2"),sQuery(id+"F0.wireOp",EDGE,"E5.8.0.0"),sQuery(id+"F0.wireOp",EDGE,"E5.8.0.1"),sQuery(id+"F0.wireOp",EDGE,"E5.8.0.2"),sQuery(id+"F0.wireOp",EDGE,"E5.8.0.3"),sQuery(id+"F0.wireOp",EDGE,"E5.8.1.0"),sQuery(id+"F0.wireOp",EDGE,"E5.8.1.1"),sQuery(id+"F0.wireOp",EDGE,"E5.8.1.2"),sQuery(id+"F0.wireOp",EDGE,"E5.8.1.3"),sQuery(id+"F0.wireOp",EDGE,"E5.8.2.0"),sQuery(id+"F0.wireOp",EDGE,"E5.8.2.1"),sQuery(id+"F0.wireOp",EDGE,"E5.8.2.2"),sQuery(id+"F0.wireOp",EDGE,"E5.8.2.3"),sQuery(id+"F0.wireOp",EDGE,"E5.8.3.0"),sQuery(id+"F0.wireOp",EDGE,"E5.8.3.1"),sQuery(id+"F0.wireOp",EDGE,"E5.8.3.2"),sQuery(id+"F0.wireOp",EDGE,"E5.8.3.3"),sQuery(id+"F0.wireOp",EDGE,"E5.8.4.2"),sQuery(id+"F0.wireOp",EDGE,"E5.9.0.2"),sQuery(id+"F0.wireOp",EDGE,"E5.9.0.3"),sQuery(id+"F0.wireOp",EDGE,"E5.9.1.2"),sQuery(id+"F0.wireOp",EDGE,"E5.9.1.3"),sQuery(id+"F0.wireOp",EDGE,"E5.9.2.2"),sQuery(id+"F0.wireOp",EDGE,"E6.1.0.0"),sQuery(id+"F0.wireOp",EDGE,"E6.1.0.2"),sQuery(id+"F0.wireOp",EDGE,"E6.1.0.3"),sQuery(id+"F0.wireOp",EDGE,"E6.1.0.4"),sQuery(id+"F0.wireOp",EDGE,"E6.1.0.5"),sQuery(id+"F0.wireOp",EDGE,"E6.1.0.6"),sQuery(id+"F0.wireOp",EDGE,"E6.1.0.7"),sQuery(id+"F0.wireOp",EDGE,"E6.1.0.8"),sQuery(id+"F0.wireOp",EDGE,"E6.1.0.10"),sQuery(id+"F0.wireOp",EDGE,"E6.1.0.12"),sQuery(id+"F0.wireOp",EDGE,"E6.1.0.14"),sQuery(id+"F0.wireOp",EDGE,"E6.1.0.16"),sQuery(id+"F0.wireOp",EDGE,"E6.1.0.18"),sQuery(id+"F0.wireOp",EDGE,"E6.1.0.19"),sQuery(id+"F0.wireOp",EDGE,"E6.1.0.20"),sQuery(id+"F0.wireOp",EDGE,"E6.1.0.21"),sQuery(id+"F0.wireOp",EDGE,"E6.1.0.22"),sQuery(id+"F0.wireOp",EDGE,"E6.1.0.23"),sQuery(id+"F0.wireOp",EDGE,"E6.1.0.24"),sQuery(id+"F0.wireOp",EDGE,"E6.1.0.25"),sQuery(id+"F0.wireOp",EDGE,"E6.1.0.27"),sQuery(id+"F0.wireOp",EDGE,"E6.1.0.28"),sQuery(id+"F0.wireOp",EDGE,"E6.1.0.29"),sQuery(id+"F0.wireOp",EDGE,"E6.1.0.30"),sQuery(id+"F0.wireOp",EDGE,"E6.1.0.31"),sQuery(id+"F0.wireOp",EDGE,"E6.1.0.32"),sQuery(id+"F0.wireOp",EDGE,"E6.1.0.33"),sQuery(id+"F0.wireOp",EDGE,"E6.1.0.34"),sQuery(id+"F0.wireOp",EDGE,"E6.1.0.35"),sQuery(id+"F0.wireOp",EDGE,"E6.1.0.36"),sQuery(id+"F0.wireOp",EDGE,"E6.1.0.37"),sQuery(id+"F0.wireOp",EDGE,"E6.1.0.38"),sQuery(id+"F0.wireOp",EDGE,"E6.1.0.39"),sQuery(id+"F0.wireOp",EDGE,"E6.1.0.40"),sQuery(id+"F0.wireOp",EDGE,"E6.2.0.0"),sQuery(id+"F0.wireOp",EDGE,"E6.2.0.2"),sQuery(id+"F0.wireOp",EDGE,"E6.2.0.3"),sQuery(id+"F0.wireOp",EDGE,"E6.2.0.4"),sQuery(id+"F0.wireOp",EDGE,"E6.2.0.5"),sQuery(id+"F0.wireOp",EDGE,"E6.2.0.6"),sQuery(id+"F0.wireOp",EDGE,"E6.2.0.7"),sQuery(id+"F0.wireOp",EDGE,"E6.2.0.8"),sQuery(id+"F0.wireOp",EDGE,"E6.2.0.10"),sQuery(id+"F0.wireOp",EDGE,"E6.2.0.12"),sQuery(id+"F0.wireOp",EDGE,"E6.2.0.14"),sQuery(id+"F0.wireOp",EDGE,"E6.2.0.16"),sQuery(id+"F0.wireOp",EDGE,"E6.2.0.18"),sQuery(id+"F0.wireOp",EDGE,"E6.2.0.19"),sQuery(id+"F0.wireOp",EDGE,"E6.2.0.20"),sQuery(id+"F0.wireOp",EDGE,"E6.2.0.21"),sQuery(id+"F0.wireOp",EDGE,"E6.2.0.22"),sQuery(id+"F0.wireOp",EDGE,"E6.2.0.23"),sQuery(id+"F0.wireOp",EDGE,"E6.2.0.24"),sQuery(id+"F0.wireOp",EDGE,"E6.2.0.25"),sQuery(id+"F0.wireOp",EDGE,"E6.2.0.27"),sQuery(id+"F0.wireOp",EDGE,"E6.2.0.28"),sQuery(id+"F0.wireOp",EDGE,"E6.2.0.29"),sQuery(id+"F0.wireOp",EDGE,"E6.2.0.30"),sQuery(id+"F0.wireOp",EDGE,"E6.2.0.31"),sQuery(id+"F0.wireOp",EDGE,"E6.2.0.32"),sQuery(id+"F0.wireOp",EDGE,"E6.2.0.33"),sQuery(id+"F0.wireOp",EDGE,"E6.2.0.34"),sQuery(id+"F0.wireOp",EDGE,"E6.2.0.35"),sQuery(id+"F0.wireOp",EDGE,"E6.2.0.36"),sQuery(id+"F0.wireOp",EDGE,"E6.2.0.37"),sQuery(id+"F0.wireOp",EDGE,"E6.2.0.38"),sQuery(id+"F0.wireOp",EDGE,"E6.2.0.39"),sQuery(id+"F0.wireOp",EDGE,"E6.2.0.40"),sQuery(id+"F0.wireOp",EDGE,"E6.3.0.0"),sQuery(id+"F0.wireOp",EDGE,"E6.3.0.1"),sQuery(id+"F0.wireOp",EDGE,"E6.3.0.2"),sQuery(id+"F0.wireOp",EDGE,"E6.3.0.3"),sQuery(id+"F0.wireOp",EDGE,"E6.3.0.4"),sQuery(id+"F0.wireOp",EDGE,"E6.3.0.5"),sQuery(id+"F0.wireOp",EDGE,"E6.3.0.6"),sQuery(id+"F0.wireOp",EDGE,"E6.3.0.7"),sQuery(id+"F0.wireOp",EDGE,"E6.3.0.8"),sQuery(id+"F0.wireOp",EDGE,"E6.3.0.10"),sQuery(id+"F0.wireOp",EDGE,"E6.3.0.12"),sQuery(id+"F0.wireOp",EDGE,"E6.3.0.14"),sQuery(id+"F0.wireOp",EDGE,"E6.3.0.16"),sQuery(id+"F0.wireOp",EDGE,"E6.3.0.18"),sQuery(id+"F0.wireOp",EDGE,"E6.3.0.19"),sQuery(id+"F0.wireOp",EDGE,"E6.3.0.20"),sQuery(id+"F0.wireOp",EDGE,"E6.3.0.21"),sQuery(id+"F0.wireOp",EDGE,"E6.3.0.22"),sQuery(id+"F0.wireOp",EDGE,"E6.3.0.23"),sQuery(id+"F0.wireOp",EDGE,"E6.3.0.24"),sQuery(id+"F0.wireOp",EDGE,"E6.3.0.25"),sQuery(id+"F0.wireOp",EDGE,"E6.3.0.27"),sQuery(id+"F0.wireOp",EDGE,"E6.3.0.28"),sQuery(id+"F0.wireOp",EDGE,"E6.3.0.29"),sQuery(id+"F0.wireOp",EDGE,"E6.3.0.30"),sQuery(id+"F0.wireOp",EDGE,"E6.3.0.31"),sQuery(id+"F0.wireOp",EDGE,"E6.3.0.32"),sQuery(id+"F0.wireOp",EDGE,"E6.3.0.33"),sQuery(id+"F0.wireOp",EDGE,"E6.3.0.34"),sQuery(id+"F0.wireOp",EDGE,"E6.3.0.35"),sQuery(id+"F0.wireOp",EDGE,"E6.3.0.36"),sQuery(id+"F0.wireOp",EDGE,"E6.3.0.37"),sQuery(id+"F0.wireOp",EDGE,"E6.3.0.38"),sQuery(id+"F0.wireOp",EDGE,"E6.3.0.39"),sQuery(id+"F0.wireOp",EDGE,"E6.3.0.40"),sQuery(id+"F0.wireOp",EDGE,"E6.4.0.0"),sQuery(id+"F0.wireOp",EDGE,"E6.4.0.2"),sQuery(id+"F0.wireOp",EDGE,"E6.4.0.3"),sQuery(id+"F0.wireOp",EDGE,"E6.4.0.4"),sQuery(id+"F0.wireOp",EDGE,"E6.4.0.5"),sQuery(id+"F0.wireOp",EDGE,"E6.4.0.7"),sQuery(id+"F0.wireOp",EDGE,"E6.4.0.8"),sQuery(id+"F0.wireOp",EDGE,"E6.4.0.10"),sQuery(id+"F0.wireOp",EDGE,"E6.4.0.12"),sQuery(id+"F0.wireOp",EDGE,"E6.4.0.14"),sQuery(id+"F0.wireOp",EDGE,"E6.4.0.16"),sQuery(id+"F0.wireOp",EDGE,"E6.4.0.18"),sQuery(id+"F0.wireOp",EDGE,"E6.4.0.19"),sQuery(id+"F0.wireOp",EDGE,"E6.4.0.20"),sQuery(id+"F0.wireOp",EDGE,"E6.4.0.21"),sQuery(id+"F0.wireOp",EDGE,"E6.4.0.22"),sQuery(id+"F0.wireOp",EDGE,"E6.4.0.23"),sQuery(id+"F0.wireOp",EDGE,"E6.4.0.24"),sQuery(id+"F0.wireOp",EDGE,"E6.4.0.25"),sQuery(id+"F0.wireOp",EDGE,"E6.4.0.27"),sQuery(id+"F0.wireOp",EDGE,"E6.4.0.28"),sQuery(id+"F0.wireOp",EDGE,"E6.4.0.29"),sQuery(id+"F0.wireOp",EDGE,"E6.4.0.30"),sQuery(id+"F0.wireOp",EDGE,"E6.4.0.31"),sQuery(id+"F0.wireOp",EDGE,"E6.4.0.32"),sQuery(id+"F0.wireOp",EDGE,"E6.4.0.33"),sQuery(id+"F0.wireOp",EDGE,"E6.4.0.34"),sQuery(id+"F0.wireOp",EDGE,"E6.4.0.35"),sQuery(id+"F0.wireOp",EDGE,"E6.4.0.36"),sQuery(id+"F0.wireOp",EDGE,"E6.4.0.37"),sQuery(id+"F0.wireOp",EDGE,"E6.4.0.38"),sQuery(id+"F0.wireOp",EDGE,"E6.4.0.39"),sQuery(id+"F0.wireOp",EDGE,"E6.4.0.40"),sQuery(id+"F0.wireOp",EDGE,"E6.5.0.0"),sQuery(id+"F0.wireOp",EDGE,"E6.5.0.3"),sQuery(id+"F0.wireOp",EDGE,"E6.5.0.5"),sQuery(id+"F0.wireOp",EDGE,"E6.5.0.7"),sQuery(id+"F0.wireOp",EDGE,"E6.5.0.8"),sQuery(id+"F0.wireOp",EDGE,"E6.5.0.10"),sQuery(id+"F0.wireOp",EDGE,"E6.5.0.12"),sQuery(id+"F0.wireOp",EDGE,"E6.5.0.14"),sQuery(id+"F0.wireOp",EDGE,"E6.5.0.16"),sQuery(id+"F0.wireOp",EDGE,"E6.5.0.18"),sQuery(id+"F0.wireOp",EDGE,"E6.5.0.19"),sQuery(id+"F0.wireOp",EDGE,"E6.5.0.20"),sQuery(id+"F0.wireOp",EDGE,"E6.5.0.21"),sQuery(id+"F0.wireOp",EDGE,"E6.5.0.22"),sQuery(id+"F0.wireOp",EDGE,"E6.5.0.23"),sQuery(id+"F0.wireOp",EDGE,"E6.5.0.24"),sQuery(id+"F0.wireOp",EDGE,"E6.5.0.25"),sQuery(id+"F0.wireOp",EDGE,"E6.5.0.27"),sQuery(id+"F0.wireOp",EDGE,"E6.5.0.28"),sQuery(id+"F0.wireOp",EDGE,"E6.5.0.29"),sQuery(id+"F0.wireOp",EDGE,"E6.5.0.30"),sQuery(id+"F0.wireOp",EDGE,"E6.5.0.31"),sQuery(id+"F0.wireOp",EDGE,"E6.5.0.32"),sQuery(id+"F0.wireOp",EDGE,"E6.5.0.33"),sQuery(id+"F0.wireOp",EDGE,"E6.5.0.34"),sQuery(id+"F0.wireOp",EDGE,"E6.5.0.35"),sQuery(id+"F0.wireOp",EDGE,"E6.5.0.36"),sQuery(id+"F0.wireOp",EDGE,"E6.5.0.37"),sQuery(id+"F0.wireOp",EDGE,"E6.5.0.38"),sQuery(id+"F0.wireOp",EDGE,"E6.5.0.39"),sQuery(id+"F0.wireOp",EDGE,"E6.5.0.40"),sQuery(id+"F0.wireOp",EDGE,"E6.6.0.0"),sQuery(id+"F0.wireOp",EDGE,"E6.6.0.3"),sQuery(id+"F0.wireOp",EDGE,"E6.6.0.5"),sQuery(id+"F0.wireOp",EDGE,"E6.6.0.7"),sQuery(id+"F0.wireOp",EDGE,"E6.6.0.8"),sQuery(id+"F0.wireOp",EDGE,"E6.6.0.10"),sQuery(id+"F0.wireOp",EDGE,"E6.6.0.12"),sQuery(id+"F0.wireOp",EDGE,"E6.6.0.14"),sQuery(id+"F0.wireOp",EDGE,"E6.6.0.16"),sQuery(id+"F0.wireOp",EDGE,"E6.6.0.19"),sQuery(id+"F0.wireOp",EDGE,"E6.6.0.20"),sQuery(id+"F0.wireOp",EDGE,"E6.6.0.21"),sQuery(id+"F0.wireOp",EDGE,"E6.6.0.22"),sQuery(id+"F0.wireOp",EDGE,"E6.6.0.23"),sQuery(id+"F0.wireOp",EDGE,"E6.6.0.24"),sQuery(id+"F0.wireOp",EDGE,"E6.6.0.25"),sQuery(id+"F0.wireOp",EDGE,"E6.6.0.27"),sQuery(id+"F0.wireOp",EDGE,"E6.6.0.28"),sQuery(id+"F0.wireOp",EDGE,"E6.6.0.29"),sQuery(id+"F0.wireOp",EDGE,"E6.6.0.30"),sQuery(id+"F0.wireOp",EDGE,"E6.6.0.31"),sQuery(id+"F0.wireOp",EDGE,"E6.6.0.32"),sQuery(id+"F0.wireOp",EDGE,"E6.6.0.33"),sQuery(id+"F0.wireOp",EDGE,"E6.6.0.34"),sQuery(id+"F0.wireOp",EDGE,"E6.6.0.35"),sQuery(id+"F0.wireOp",EDGE,"E6.6.0.36"),sQuery(id+"F0.wireOp",EDGE,"E6.6.0.38"),sQuery(id+"F0.wireOp",EDGE,"E6.6.0.39"),sQuery(id+"F0.wireOp",EDGE,"E6.6.0.40"),sQuery(id+"F0.wireOp",EDGE,"E6.7.0.0"),sQuery(id+"F0.wireOp",EDGE,"E6.7.0.3"),sQuery(id+"F0.wireOp",EDGE,"E6.7.0.5"),sQuery(id+"F0.wireOp",EDGE,"E6.7.0.7"),sQuery(id+"F0.wireOp",EDGE,"E6.7.0.8"),sQuery(id+"F0.wireOp",EDGE,"E6.7.0.10"),sQuery(id+"F0.wireOp",EDGE,"E6.7.0.12"),sQuery(id+"F0.wireOp",EDGE,"E6.7.0.14"),sQuery(id+"F0.wireOp",EDGE,"E6.7.0.16"),sQuery(id+"F0.wireOp",EDGE,"E6.7.0.19"),sQuery(id+"F0.wireOp",EDGE,"E6.7.0.20"),sQuery(id+"F0.wireOp",EDGE,"E6.7.0.21"),sQuery(id+"F0.wireOp",EDGE,"E6.7.0.23"),sQuery(id+"F0.wireOp",EDGE,"E6.7.0.24"),sQuery(id+"F0.wireOp",EDGE,"E6.7.0.25"),sQuery(id+"F0.wireOp",EDGE,"E6.7.0.27"),sQuery(id+"F0.wireOp",EDGE,"E6.7.0.28"),sQuery(id+"F0.wireOp",EDGE,"E6.7.0.29"),sQuery(id+"F0.wireOp",EDGE,"E6.7.0.30"),sQuery(id+"F0.wireOp",EDGE,"E6.7.0.31"),sQuery(id+"F0.wireOp",EDGE,"E6.7.0.32"),sQuery(id+"F0.wireOp",EDGE,"E6.7.0.33"),sQuery(id+"F0.wireOp",EDGE,"E6.7.0.34"),sQuery(id+"F0.wireOp",EDGE,"E6.7.0.36"),sQuery(id+"F0.wireOp",EDGE,"E6.7.0.38"),sQuery(id+"F0.wireOp",EDGE,"E6.7.0.39"),sQuery(id+"F0.wireOp",EDGE,"E6.7.0.40"),sQuery(id+"F0.wireOp",EDGE,"E6.8.0.0"),sQuery(id+"F0.wireOp",EDGE,"E6.8.0.3"),sQuery(id+"F0.wireOp",EDGE,"E6.8.0.5"),sQuery(id+"F0.wireOp",EDGE,"E6.8.0.7"),sQuery(id+"F0.wireOp",EDGE,"E6.8.0.8"),sQuery(id+"F0.wireOp",EDGE,"E6.8.0.10"),sQuery(id+"F0.wireOp",EDGE,"E6.8.0.12"),sQuery(id+"F0.wireOp",EDGE,"E6.8.0.14"),sQuery(id+"F0.wireOp",EDGE,"E6.8.0.23"),sQuery(id+"F0.wireOp",EDGE,"E6.8.0.24"),sQuery(id+"F0.wireOp",EDGE,"E6.8.0.25"),sQuery(id+"F0.wireOp",EDGE,"E6.8.0.27"),sQuery(id+"F0.wireOp",EDGE,"E6.8.0.28"),sQuery(id+"F0.wireOp",EDGE,"E6.8.0.29"),sQuery(id+"F0.wireOp",EDGE,"E6.8.0.30"),sQuery(id+"F0.wireOp",EDGE,"E6.8.0.31"),sQuery(id+"F0.wireOp",EDGE,"E6.8.0.32"),sQuery(id+"F0.wireOp",EDGE,"E6.8.0.33"),sQuery(id+"F0.wireOp",EDGE,"E6.8.0.34"),sQuery(id+"F0.wireOp",EDGE,"E6.8.0.36"),sQuery(id+"F0.wireOp",EDGE,"E6.8.0.38"),sQuery(id+"F0.wireOp",EDGE,"E6.8.0.39"),sQuery(id+"F0.wireOp",EDGE,"E6.8.0.40"),sQuery(id+"F0.wireOp",EDGE,"E6.9.0.0"),sQuery(id+"F0.wireOp",EDGE,"E6.9.0.3"),sQuery(id+"F0.wireOp",EDGE,"E6.9.0.5"),sQuery(id+"F0.wireOp",EDGE,"E6.9.0.23"),sQuery(id+"F0.wireOp",EDGE,"E6.9.0.24"),sQuery(id+"F0.wireOp",EDGE,"E6.9.0.25"),sQuery(id+"F0.wireOp",EDGE,"E6.9.0.27"),sQuery(id+"F0.wireOp",EDGE,"E6.9.0.28"),sQuery(id+"F0.wireOp",EDGE,"E6.9.0.29"),sQuery(id+"F0.wireOp",EDGE,"E6.9.0.30"),sQuery(id+"F0.wireOp",EDGE,"E6.9.0.31"),sQuery(id+"F0.wireOp",EDGE,"E6.9.0.32"),sQuery(id+"F0.wireOp",EDGE,"E6.9.0.33"),sQuery(id+"F0.wireOp",EDGE,"E6.9.0.34"),sQuery(id+"F0.wireOp",EDGE,"E6.9.0.36"),sQuery(id+"F0.wireOp",EDGE,"E6.9.0.38"),sQuery(id+"F0.wireOp",EDGE,"E6.9.0.39"),sQuery(id+"F0.wireOp",EDGE,"E6.9.0.40"),sQuery(id+"F0.wireOp",EDGE,"E6.10.0.28"),sQuery(id+"F0.wireOp",EDGE,"E6.10.0.29"),sQuery(id+"F0.wireOp",EDGE,"E6.10.0.30"),sQuery(id+"F0.wireOp",EDGE,"E6.10.0.31"),sQuery(id+"F0.wireOp",EDGE,"E6.10.0.33"),sQuery(id+"F0.wireOp",EDGE,"E6.10.0.34"),sQuery(id+"F0.wireOp",EDGE,"E7.0.1.0"),sQuery(id+"F0.wireOp",EDGE,"E7.0.1.1"),sQuery(id+"F0.wireOp",EDGE,"E7.0.1.2"),sQuery(id+"F0.wireOp",EDGE,"E7.0.1.3"),sQuery(id+"F0.wireOp",EDGE,"E7.0.1.4"),sQuery(id+"F0.wireOp",EDGE,"E7.0.1.5"),sQuery(id+"F0.wireOp",EDGE,"E7.0.1.6"),sQuery(id+"F0.wireOp",EDGE,"E7.0.1.8"),sQuery(id+"F0.wireOp",EDGE,"E7.0.1.9"),sQuery(id+"F0.wireOp",EDGE,"E7.0.1.10"),sQuery(id+"F0.wireOp",EDGE,"E7.0.1.11"),sQuery(id+"F0.wireOp",EDGE,"E7.0.1.12"),sQuery(id+"F0.wireOp",EDGE,"E7.0.1.13"),sQuery(id+"F0.wireOp",EDGE,"E7.0.1.14"),sQuery(id+"F0.wireOp",EDGE,"E7.0.1.15"),sQuery(id+"F0.wireOp",EDGE,"E7.0.1.17"),sQuery(id+"F0.wireOp",EDGE,"E7.0.1.18"),sQuery(id+"F0.wireOp",EDGE,"E7.0.1.19"),sQuery(id+"F0.wireOp",EDGE,"E7.0.1.21"),sQuery(id+"F0.wireOp",EDGE,"E7.0.1.22"),sQuery(id+"F0.wireOp",EDGE,"E7.0.1.23"),sQuery(id+"F0.wireOp",EDGE,"E7.0.1.24"),sQuery(id+"F0.wireOp",EDGE,"E7.0.1.25"),sQuery(id+"F0.wireOp",EDGE,"E7.0.1.26"),sQuery(id+"F0.wireOp",EDGE,"E7.0.1.27"),sQuery(id+"F0.wireOp",EDGE,"E7.0.1.28"),sQuery(id+"F0.wireOp",EDGE,"E7.0.1.29"),sQuery(id+"F0.wireOp",EDGE,"E7.0.1.32"),sQuery(id+"F0.wireOp",EDGE,"E7.0.1.34"),sQuery(id+"F0.wireOp",EDGE,"E7.0.1.35"),sQuery(id+"F0.wireOp",EDGE,"E7.0.1.36"),sQuery(id+"F0.wireOp",EDGE,"E7.0.1.37"),sQuery(id+"F0.wireOp",EDGE,"E7.0.1.38"),sQuery(id+"F0.wireOp",EDGE,"E7.0.1.39"),sQuery(id+"F0.wireOp",EDGE,"E7.0.1.40"),sQuery(id+"F0.wireOp",EDGE,"E7.0.1.41"),sQuery(id+"F0.wireOp",EDGE,"E7.0.1.42"),sQuery(id+"F0.wireOp",EDGE,"E7.0.1.43"),sQuery(id+"F0.wireOp",EDGE,"E7.0.2.0"),sQuery(id+"F0.wireOp",EDGE,"E7.0.2.1"),sQuery(id+"F0.wireOp",EDGE,"E7.0.2.2"),sQuery(id+"F0.wireOp",EDGE,"E7.0.2.3"),sQuery(id+"F0.wireOp",EDGE,"E7.0.2.4"),sQuery(id+"F0.wireOp",EDGE,"E7.0.2.5"),sQuery(id+"F0.wireOp",EDGE,"E7.0.2.6"),sQuery(id+"F0.wireOp",EDGE,"E7.0.2.8"),sQuery(id+"F0.wireOp",EDGE,"E7.0.2.9"),sQuery(id+"F0.wireOp",EDGE,"E7.0.2.10"),sQuery(id+"F0.wireOp",EDGE,"E7.0.2.11"),sQuery(id+"F0.wireOp",EDGE,"E7.0.2.12"),sQuery(id+"F0.wireOp",EDGE,"E7.0.2.13"),sQuery(id+"F0.wireOp",EDGE,"E7.0.2.14"),sQuery(id+"F0.wireOp",EDGE,"E7.0.2.15"),sQuery(id+"F0.wireOp",EDGE,"E7.0.2.17"),sQuery(id+"F0.wireOp",EDGE,"E7.0.2.18"),sQuery(id+"F0.wireOp",EDGE,"E7.0.2.19"),sQuery(id+"F0.wireOp",EDGE,"E7.0.2.21"),sQuery(id+"F0.wireOp",EDGE,"E7.0.2.22"),sQuery(id+"F0.wireOp",EDGE,"E7.0.2.23"),sQuery(id+"F0.wireOp",EDGE,"E7.0.2.24"),sQuery(id+"F0.wireOp",EDGE,"E7.0.2.25"),sQuery(id+"F0.wireOp",EDGE,"E7.0.2.26"),sQuery(id+"F0.wireOp",EDGE,"E7.0.2.27"),sQuery(id+"F0.wireOp",EDGE,"E7.0.2.28"),sQuery(id+"F0.wireOp",EDGE,"E7.0.2.29"),sQuery(id+"F0.wireOp",EDGE,"E7.0.2.32"),sQuery(id+"F0.wireOp",EDGE,"E7.0.2.34"),sQuery(id+"F0.wireOp",EDGE,"E7.0.2.35"),sQuery(id+"F0.wireOp",EDGE,"E7.0.2.36"),sQuery(id+"F0.wireOp",EDGE,"E7.0.2.37"),sQuery(id+"F0.wireOp",EDGE,"E7.0.2.38"),sQuery(id+"F0.wireOp",EDGE,"E7.0.2.39"),sQuery(id+"F0.wireOp",EDGE,"E7.0.2.40"),sQuery(id+"F0.wireOp",EDGE,"E7.0.2.41"),sQuery(id+"F0.wireOp",EDGE,"E7.0.2.42"),sQuery(id+"F0.wireOp",EDGE,"E7.0.2.43"),sQuery(id+"F0.wireOp",EDGE,"E7.0.3.0"),sQuery(id+"F0.wireOp",EDGE,"E7.0.3.1"),sQuery(id+"F0.wireOp",EDGE,"E7.0.3.2"),sQuery(id+"F0.wireOp",EDGE,"E7.0.3.3"),sQuery(id+"F0.wireOp",EDGE,"E7.0.3.4"),sQuery(id+"F0.wireOp",EDGE,"E7.0.3.5"),sQuery(id+"F0.wireOp",EDGE,"E7.0.3.6"),sQuery(id+"F0.wireOp",EDGE,"E7.0.3.8"),sQuery(id+"F0.wireOp",EDGE,"E7.0.3.9"),sQuery(id+"F0.wireOp",EDGE,"E7.0.3.10"),sQuery(id+"F0.wireOp",EDGE,"E7.0.3.11"),sQuery(id+"F0.wireOp",EDGE,"E7.0.3.12"),sQuery(id+"F0.wireOp",EDGE,"E7.0.3.13"),sQuery(id+"F0.wireOp",EDGE,"E7.0.3.14"),sQuery(id+"F0.wireOp",EDGE,"E7.0.3.15"),sQuery(id+"F0.wireOp",EDGE,"E7.0.3.17"),sQuery(id+"F0.wireOp",EDGE,"E7.0.3.18"),sQuery(id+"F0.wireOp",EDGE,"E7.0.3.19"),sQuery(id+"F0.wireOp",EDGE,"E7.0.3.21"),sQuery(id+"F0.wireOp",EDGE,"E7.0.3.22"),sQuery(id+"F0.wireOp",EDGE,"E7.0.3.23"),sQuery(id+"F0.wireOp",EDGE,"E7.0.3.24"),sQuery(id+"F0.wireOp",EDGE,"E7.0.3.25"),sQuery(id+"F0.wireOp",EDGE,"E7.0.3.26"),sQuery(id+"F0.wireOp",EDGE,"E7.0.3.27"),sQuery(id+"F0.wireOp",EDGE,"E7.0.3.28"),sQuery(id+"F0.wireOp",EDGE,"E7.0.3.29"),sQuery(id+"F0.wireOp",EDGE,"E7.0.3.32"),sQuery(id+"F0.wireOp",EDGE,"E7.0.3.34"),sQuery(id+"F0.wireOp",EDGE,"E7.0.3.35"),sQuery(id+"F0.wireOp",EDGE,"E7.0.3.36"),sQuery(id+"F0.wireOp",EDGE,"E7.0.3.37"),sQuery(id+"F0.wireOp",EDGE,"E7.0.3.38"),sQuery(id+"F0.wireOp",EDGE,"E7.0.3.39"),sQuery(id+"F0.wireOp",EDGE,"E7.0.3.40"),sQuery(id+"F0.wireOp",EDGE,"E7.0.3.41"),sQuery(id+"F0.wireOp",EDGE,"E7.0.3.42"),sQuery(id+"F0.wireOp",EDGE,"E7.0.3.43"),sQuery(id+"F0.wireOp",EDGE,"E7.0.4.0"),sQuery(id+"F0.wireOp",EDGE,"E7.0.4.1"),sQuery(id+"F0.wireOp",EDGE,"E7.0.4.2"),sQuery(id+"F0.wireOp",EDGE,"E7.0.4.3"),sQuery(id+"F0.wireOp",EDGE,"E7.0.4.4"),sQuery(id+"F0.wireOp",EDGE,"E7.0.4.5"),sQuery(id+"F0.wireOp",EDGE,"E7.0.4.6"),sQuery(id+"F0.wireOp",EDGE,"E7.0.4.8"),sQuery(id+"F0.wireOp",EDGE,"E7.0.4.9"),sQuery(id+"F0.wireOp",EDGE,"E7.0.4.10"),sQuery(id+"F0.wireOp",EDGE,"E7.0.4.11"),sQuery(id+"F0.wireOp",EDGE,"E7.0.4.12"),sQuery(id+"F0.wireOp",EDGE,"E7.0.4.13"),sQuery(id+"F0.wireOp",EDGE,"E7.0.4.14"),sQuery(id+"F0.wireOp",EDGE,"E7.0.4.15"),sQuery(id+"F0.wireOp",EDGE,"E7.0.4.17"),sQuery(id+"F0.wireOp",EDGE,"E7.0.4.18"),sQuery(id+"F0.wireOp",EDGE,"E7.0.4.19"),sQuery(id+"F0.wireOp",EDGE,"E7.0.4.21"),sQuery(id+"F0.wireOp",EDGE,"E7.0.4.22"),sQuery(id+"F0.wireOp",EDGE,"E7.0.4.23"),sQuery(id+"F0.wireOp",EDGE,"E7.0.4.24"),sQuery(id+"F0.wireOp",EDGE,"E7.0.4.25"),sQuery(id+"F0.wireOp",EDGE,"E7.0.4.26"),sQuery(id+"F0.wireOp",EDGE,"E7.0.4.27"),sQuery(id+"F0.wireOp",EDGE,"E7.0.4.28"),sQuery(id+"F0.wireOp",EDGE,"E7.0.4.29"),sQuery(id+"F0.wireOp",EDGE,"E7.0.4.32"),sQuery(id+"F0.wireOp",EDGE,"E7.0.4.34"),sQuery(id+"F0.wireOp",EDGE,"E7.0.4.35"),sQuery(id+"F0.wireOp",EDGE,"E7.0.4.36"),sQuery(id+"F0.wireOp",EDGE,"E7.0.4.37"),sQuery(id+"F0.wireOp",EDGE,"E7.0.4.38"),sQuery(id+"F0.wireOp",EDGE,"E7.0.4.39"),sQuery(id+"F0.wireOp",EDGE,"E7.0.4.40"),sQuery(id+"F0.wireOp",EDGE,"E7.0.4.41"),sQuery(id+"F0.wireOp",EDGE,"E7.0.4.42"),sQuery(id+"F0.wireOp",EDGE,"E7.0.4.43"),sQuery(id+"F0.wireOp",EDGE,"E7.0.5.0"),sQuery(id+"F0.wireOp",EDGE,"E7.0.5.1"),sQuery(id+"F0.wireOp",EDGE,"E7.0.5.2"),sQuery(id+"F0.wireOp",EDGE,"E7.0.5.3"),sQuery(id+"F0.wireOp",EDGE,"E7.0.5.4"),sQuery(id+"F0.wireOp",EDGE,"E7.0.5.5"),sQuery(id+"F0.wireOp",EDGE,"E7.0.5.6"),sQuery(id+"F0.wireOp",EDGE,"E7.0.5.8"),sQuery(id+"F0.wireOp",EDGE,"E7.0.5.9"),sQuery(id+"F0.wireOp",EDGE,"E7.0.5.10"),sQuery(id+"F0.wireOp",EDGE,"E7.0.5.11"),sQuery(id+"F0.wireOp",EDGE,"E7.0.5.12"),sQuery(id+"F0.wireOp",EDGE,"E7.0.5.13"),sQuery(id+"F0.wireOp",EDGE,"E7.0.5.14"),sQuery(id+"F0.wireOp",EDGE,"E7.0.5.15"),sQuery(id+"F0.wireOp",EDGE,"E7.0.5.17"),sQuery(id+"F0.wireOp",EDGE,"E7.0.5.18"),sQuery(id+"F0.wireOp",EDGE,"E7.0.5.19"),sQuery(id+"F0.wireOp",EDGE,"E7.0.5.21"),sQuery(id+"F0.wireOp",EDGE,"E7.0.5.22"),sQuery(id+"F0.wireOp",EDGE,"E7.0.5.23"),sQuery(id+"F0.wireOp",EDGE,"E7.0.5.24"),sQuery(id+"F0.wireOp",EDGE,"E7.0.5.26"),sQuery(id+"F0.wireOp",EDGE,"E7.0.5.27"),sQuery(id+"F0.wireOp",EDGE,"E7.0.5.28"),sQuery(id+"F0.wireOp",EDGE,"E7.0.5.29"),sQuery(id+"F0.wireOp",EDGE,"E7.0.5.32"),sQuery(id+"F0.wireOp",EDGE,"E7.0.5.34"),sQuery(id+"F0.wireOp",EDGE,"E7.0.5.35"),sQuery(id+"F0.wireOp",EDGE,"E7.0.5.36"),sQuery(id+"F0.wireOp",EDGE,"E7.0.5.37"),sQuery(id+"F0.wireOp",EDGE,"E7.0.5.38"),sQuery(id+"F0.wireOp",EDGE,"E7.0.5.39"),sQuery(id+"F0.wireOp",EDGE,"E7.0.5.40"),sQuery(id+"F0.wireOp",EDGE,"E7.0.5.41"),sQuery(id+"F0.wireOp",EDGE,"E7.0.5.42"),sQuery(id+"F0.wireOp",EDGE,"E7.0.5.43"),sQuery(id+"F0.wireOp",EDGE,"E7.0.6.0"),sQuery(id+"F0.wireOp",EDGE,"E7.0.6.1"),sQuery(id+"F0.wireOp",EDGE,"E7.0.6.2"),sQuery(id+"F0.wireOp",EDGE,"E7.0.6.3"),sQuery(id+"F0.wireOp",EDGE,"E7.0.6.4"),sQuery(id+"F0.wireOp",EDGE,"E7.0.6.5"),sQuery(id+"F0.wireOp",EDGE,"E7.0.6.6"),sQuery(id+"F0.wireOp",EDGE,"E7.0.6.8"),sQuery(id+"F0.wireOp",EDGE,"E7.0.6.9"),sQuery(id+"F0.wireOp",EDGE,"E7.0.6.10"),sQuery(id+"F0.wireOp",EDGE,"E7.0.6.11"),sQuery(id+"F0.wireOp",EDGE,"E7.0.6.12"),sQuery(id+"F0.wireOp",EDGE,"E7.0.6.13"),sQuery(id+"F0.wireOp",EDGE,"E7.0.6.14"),sQuery(id+"F0.wireOp",EDGE,"E7.0.6.15"),sQuery(id+"F0.wireOp",EDGE,"E7.0.6.17"),sQuery(id+"F0.wireOp",EDGE,"E7.0.6.18"),sQuery(id+"F0.wireOp",EDGE,"E7.0.6.19"),sQuery(id+"F0.wireOp",EDGE,"E7.0.6.21"),sQuery(id+"F0.wireOp",EDGE,"E7.0.6.22"),sQuery(id+"F0.wireOp",EDGE,"E7.0.6.23"),sQuery(id+"F0.wireOp",EDGE,"E7.0.6.24"),sQuery(id+"F0.wireOp",EDGE,"E7.0.6.26"),sQuery(id+"F0.wireOp",EDGE,"E7.0.6.27"),sQuery(id+"F0.wireOp",EDGE,"E7.0.6.28"),sQuery(id+"F0.wireOp",EDGE,"E7.0.6.29"),sQuery(id+"F0.wireOp",EDGE,"E7.0.6.32"),sQuery(id+"F0.wireOp",EDGE,"E7.0.6.34"),sQuery(id+"F0.wireOp",EDGE,"E7.0.6.35"),sQuery(id+"F0.wireOp",EDGE,"E7.0.6.36"),sQuery(id+"F0.wireOp",EDGE,"E7.0.6.37"),sQuery(id+"F0.wireOp",EDGE,"E7.0.6.38"),sQuery(id+"F0.wireOp",EDGE,"E7.0.6.39"),sQuery(id+"F0.wireOp",EDGE,"E7.0.6.40"),sQuery(id+"F0.wireOp",EDGE,"E7.0.6.41"),sQuery(id+"F0.wireOp",EDGE,"E7.0.6.42"),sQuery(id+"F0.wireOp",EDGE,"E7.0.6.43"),sQuery(id+"F0.wireOp",EDGE,"E7.0.7.0"),sQuery(id+"F0.wireOp",EDGE,"E7.0.7.1"),sQuery(id+"F0.wireOp",EDGE,"E7.0.7.2"),sQuery(id+"F0.wireOp",EDGE,"E7.0.7.3"),sQuery(id+"F0.wireOp",EDGE,"E7.0.7.4"),sQuery(id+"F0.wireOp",EDGE,"E7.0.7.5"),sQuery(id+"F0.wireOp",EDGE,"E7.0.7.6"),sQuery(id+"F0.wireOp",EDGE,"E7.0.7.8"),sQuery(id+"F0.wireOp",EDGE,"E7.0.7.9"),sQuery(id+"F0.wireOp",EDGE,"E7.0.7.10"),sQuery(id+"F0.wireOp",EDGE,"E7.0.7.11"),sQuery(id+"F0.wireOp",EDGE,"E7.0.7.12"),sQuery(id+"F0.wireOp",EDGE,"E7.0.7.13"),sQuery(id+"F0.wireOp",EDGE,"E7.0.7.14"),sQuery(id+"F0.wireOp",EDGE,"E7.0.7.15"),sQuery(id+"F0.wireOp",EDGE,"E7.0.7.18"),sQuery(id+"F0.wireOp",EDGE,"E7.0.7.19"),sQuery(id+"F0.wireOp",EDGE,"E7.0.7.21"),sQuery(id+"F0.wireOp",EDGE,"E7.0.7.22"),sQuery(id+"F0.wireOp",EDGE,"E7.0.7.23"),sQuery(id+"F0.wireOp",EDGE,"E7.0.7.26"),sQuery(id+"F0.wireOp",EDGE,"E7.0.7.27"),sQuery(id+"F0.wireOp",EDGE,"E7.0.7.28"),sQuery(id+"F0.wireOp",EDGE,"E7.0.7.29"),sQuery(id+"F0.wireOp",EDGE,"E7.0.7.32"),sQuery(id+"F0.wireOp",EDGE,"E7.0.7.34"),sQuery(id+"F0.wireOp",EDGE,"E7.0.7.35"),sQuery(id+"F0.wireOp",EDGE,"E7.0.7.36"),sQuery(id+"F0.wireOp",EDGE,"E7.0.7.37"),sQuery(id+"F0.wireOp",EDGE,"E7.0.7.38"),sQuery(id+"F0.wireOp",EDGE,"E7.0.7.39"),sQuery(id+"F0.wireOp",EDGE,"E7.0.7.40"),sQuery(id+"F0.wireOp",EDGE,"E7.0.7.41"),sQuery(id+"F0.wireOp",EDGE,"E7.0.7.42"),sQuery(id+"F0.wireOp",EDGE,"E7.0.7.43"),sQuery(id+"F0.wireOp",EDGE,"E7.0.8.0"),sQuery(id+"F0.wireOp",EDGE,"E7.0.8.1"),sQuery(id+"F0.wireOp",EDGE,"E7.0.8.2"),sQuery(id+"F0.wireOp",EDGE,"E7.0.8.3"),sQuery(id+"F0.wireOp",EDGE,"E7.0.8.4"),sQuery(id+"F0.wireOp",EDGE,"E7.0.8.5"),sQuery(id+"F0.wireOp",EDGE,"E7.0.8.6"),sQuery(id+"F0.wireOp",EDGE,"E7.0.8.8"),sQuery(id+"F0.wireOp",EDGE,"E7.0.8.9"),sQuery(id+"F0.wireOp",EDGE,"E7.0.8.10"),sQuery(id+"F0.wireOp",EDGE,"E7.0.8.11"),sQuery(id+"F0.wireOp",EDGE,"E7.0.8.12"),sQuery(id+"F0.wireOp",EDGE,"E7.0.8.13"),sQuery(id+"F0.wireOp",EDGE,"E7.0.8.14"),sQuery(id+"F0.wireOp",EDGE,"E7.0.8.15"),sQuery(id+"F0.wireOp",EDGE,"E7.0.8.18"),sQuery(id+"F0.wireOp",EDGE,"E7.0.8.19"),sQuery(id+"F0.wireOp",EDGE,"E7.0.8.21"),sQuery(id+"F0.wireOp",EDGE,"E7.0.8.22"),sQuery(id+"F0.wireOp",EDGE,"E7.0.8.23"),sQuery(id+"F0.wireOp",EDGE,"E7.0.8.26"),sQuery(id+"F0.wireOp",EDGE,"E7.0.8.27"),sQuery(id+"F0.wireOp",EDGE,"E7.0.8.28"),sQuery(id+"F0.wireOp",EDGE,"E7.0.8.29"),sQuery(id+"F0.wireOp",EDGE,"E7.0.8.32"),sQuery(id+"F0.wireOp",EDGE,"E7.0.8.34"),sQuery(id+"F0.wireOp",EDGE,"E7.0.8.36"),sQuery(id+"F0.wireOp",EDGE,"E7.0.8.37"),sQuery(id+"F0.wireOp",EDGE,"E7.0.8.38"),sQuery(id+"F0.wireOp",EDGE,"E7.0.8.39"),sQuery(id+"F0.wireOp",EDGE,"E7.0.8.40"),sQuery(id+"F0.wireOp",EDGE,"E7.0.8.41"),sQuery(id+"F0.wireOp",EDGE,"E7.0.8.42"),sQuery(id+"F0.wireOp",EDGE,"E7.0.8.43"),sQuery(id+"F0.wireOp",EDGE,"E7.0.9.0"),sQuery(id+"F0.wireOp",EDGE,"E7.0.9.1"),sQuery(id+"F0.wireOp",EDGE,"E7.0.9.2"),sQuery(id+"F0.wireOp",EDGE,"E7.0.9.3"),sQuery(id+"F0.wireOp",EDGE,"E7.0.9.4"),sQuery(id+"F0.wireOp",EDGE,"E7.0.9.5"),sQuery(id+"F0.wireOp",EDGE,"E7.0.9.9"),sQuery(id+"F0.wireOp",EDGE,"E7.0.9.10"),sQuery(id+"F0.wireOp",EDGE,"E7.0.9.11"),sQuery(id+"F0.wireOp",EDGE,"E7.0.9.12"),sQuery(id+"F0.wireOp",EDGE,"E7.0.9.13"),sQuery(id+"F0.wireOp",EDGE,"E7.0.9.14"),sQuery(id+"F0.wireOp",EDGE,"E7.0.9.15"),sQuery(id+"F0.wireOp",EDGE,"E7.0.9.18"),sQuery(id+"F0.wireOp",EDGE,"E7.0.9.19"),sQuery(id+"F0.wireOp",EDGE,"E7.0.9.21"),sQuery(id+"F0.wireOp",EDGE,"E7.0.9.22"),sQuery(id+"F0.wireOp",EDGE,"E7.0.9.23"),sQuery(id+"F0.wireOp",EDGE,"E7.0.9.26"),sQuery(id+"F0.wireOp",EDGE,"E7.0.9.27"),sQuery(id+"F0.wireOp",EDGE,"E7.0.9.28"),sQuery(id+"F0.wireOp",EDGE,"E7.0.9.29"),sQuery(id+"F0.wireOp",EDGE,"E7.0.9.32"),sQuery(id+"F0.wireOp",EDGE,"E7.0.9.34"),sQuery(id+"F0.wireOp",EDGE,"E7.0.9.36"),sQuery(id+"F0.wireOp",EDGE,"E7.0.9.37"),sQuery(id+"F0.wireOp",EDGE,"E7.0.9.38"),sQuery(id+"F0.wireOp",EDGE,"E7.0.9.39"),sQuery(id+"F0.wireOp",EDGE,"E7.0.9.40"),sQuery(id+"F0.wireOp",EDGE,"E7.0.9.41"),sQuery(id+"F0.wireOp",EDGE,"E7.0.9.42"),sQuery(id+"F0.wireOp",EDGE,"E7.0.9.43"),sQuery(id+"F0.wireOp",EDGE,"E7.0.10.0"),sQuery(id+"F0.wireOp",EDGE,"E7.0.10.1"),sQuery(id+"F0.wireOp",EDGE,"E7.0.10.2"),sQuery(id+"F0.wireOp",EDGE,"E7.0.10.3"),sQuery(id+"F0.wireOp",EDGE,"E7.0.10.4"),sQuery(id+"F0.wireOp",EDGE,"E7.0.10.5"),sQuery(id+"F0.wireOp",EDGE,"E7.0.10.9"),sQuery(id+"F0.wireOp",EDGE,"E7.0.10.10"),sQuery(id+"F0.wireOp",EDGE,"E7.0.10.11"),sQuery(id+"F0.wireOp",EDGE,"E7.0.10.12"),sQuery(id+"F0.wireOp",EDGE,"E7.0.10.13"),sQuery(id+"F0.wireOp",EDGE,"E7.0.10.14"),sQuery(id+"F0.wireOp",EDGE,"E7.0.10.15"),sQuery(id+"F0.wireOp",EDGE,"E7.0.10.18"),sQuery(id+"F0.wireOp",EDGE,"E7.0.10.21"),sQuery(id+"F0.wireOp",EDGE,"E7.0.10.22"),sQuery(id+"F0.wireOp",EDGE,"E7.0.10.23"),sQuery(id+"F0.wireOp",EDGE,"E7.0.10.26"),sQuery(id+"F0.wireOp",EDGE,"E7.0.10.27"),sQuery(id+"F0.wireOp",EDGE,"E7.0.10.28"),sQuery(id+"F0.wireOp",EDGE,"E7.0.10.29"),sQuery(id+"F0.wireOp",EDGE,"E7.0.10.32"),sQuery(id+"F0.wireOp",EDGE,"E7.0.10.34"),sQuery(id+"F0.wireOp",EDGE,"E7.0.10.36"),sQuery(id+"F0.wireOp",EDGE,"E7.0.10.37"),sQuery(id+"F0.wireOp",EDGE,"E7.0.10.38"),sQuery(id+"F0.wireOp",EDGE,"E7.0.10.39"),sQuery(id+"F0.wireOp",EDGE,"E7.0.10.40"),sQuery(id+"F0.wireOp",EDGE,"E7.0.10.41"),sQuery(id+"F0.wireOp",EDGE,"E7.0.10.42"),sQuery(id+"F0.wireOp",EDGE,"E7.0.10.43"),sQuery(id+"F0.wireOp",EDGE,"E7.0.11.0"),sQuery(id+"F0.wireOp",EDGE,"E7.0.11.1"),sQuery(id+"F0.wireOp",EDGE,"E7.0.11.2"),sQuery(id+"F0.wireOp",EDGE,"E7.0.11.3"),sQuery(id+"F0.wireOp",EDGE,"E7.0.11.4"),sQuery(id+"F0.wireOp",EDGE,"E7.0.11.5"),sQuery(id+"F0.wireOp",EDGE,"E7.0.11.9"),sQuery(id+"F0.wireOp",EDGE,"E7.0.11.10"),sQuery(id+"F0.wireOp",EDGE,"E7.0.11.11"),sQuery(id+"F0.wireOp",EDGE,"E7.0.11.12"),sQuery(id+"F0.wireOp",EDGE,"E7.0.11.13"),sQuery(id+"F0.wireOp",EDGE,"E7.0.11.14"),sQuery(id+"F0.wireOp",EDGE,"E7.0.11.15"),sQuery(id+"F0.wireOp",EDGE,"E7.0.11.18"),sQuery(id+"F0.wireOp",EDGE,"E7.0.11.21"),sQuery(id+"F0.wireOp",EDGE,"E7.0.11.22"),sQuery(id+"F0.wireOp",EDGE,"E7.0.11.23"),sQuery(id+"F0.wireOp",EDGE,"E7.0.11.26"),sQuery(id+"F0.wireOp",EDGE,"E7.0.11.27"),sQuery(id+"F0.wireOp",EDGE,"E7.0.11.28"),sQuery(id+"F0.wireOp",EDGE,"E7.0.11.32"),sQuery(id+"F0.wireOp",EDGE,"E7.0.11.34"),sQuery(id+"F0.wireOp",EDGE,"E7.0.11.36"),sQuery(id+"F0.wireOp",EDGE,"E7.0.11.37"),sQuery(id+"F0.wireOp",EDGE,"E7.0.11.38"),sQuery(id+"F0.wireOp",EDGE,"E7.0.11.40"),sQuery(id+"F0.wireOp",EDGE,"E7.0.11.41"),sQuery(id+"F0.wireOp",EDGE,"E7.0.11.42"),sQuery(id+"F0.wireOp",EDGE,"E7.0.11.43"),sQuery(id+"F0.wireOp",EDGE,"E7.0.12.0"),sQuery(id+"F0.wireOp",EDGE,"E7.0.12.1"),sQuery(id+"F0.wireOp",EDGE,"E7.0.12.2"),sQuery(id+"F0.wireOp",EDGE,"E7.0.12.3"),sQuery(id+"F0.wireOp",EDGE,"E7.0.12.4"),sQuery(id+"F0.wireOp",EDGE,"E7.0.12.5"),sQuery(id+"F0.wireOp",EDGE,"E7.0.12.9"),sQuery(id+"F0.wireOp",EDGE,"E7.0.12.10"),sQuery(id+"F0.wireOp",EDGE,"E7.0.12.11"),sQuery(id+"F0.wireOp",EDGE,"E7.0.12.12"),sQuery(id+"F0.wireOp",EDGE,"E7.0.12.13"),sQuery(id+"F0.wireOp",EDGE,"E7.0.12.14"),sQuery(id+"F0.wireOp",EDGE,"E7.0.12.15"),sQuery(id+"F0.wireOp",EDGE,"E7.0.12.18"),sQuery(id+"F0.wireOp",EDGE,"E7.0.12.21"),sQuery(id+"F0.wireOp",EDGE,"E7.0.12.22"),sQuery(id+"F0.wireOp",EDGE,"E7.0.12.26"),sQuery(id+"F0.wireOp",EDGE,"E7.0.12.27"),sQuery(id+"F0.wireOp",EDGE,"E7.0.12.28"),sQuery(id+"F0.wireOp",EDGE,"E7.0.12.32"),sQuery(id+"F0.wireOp",EDGE,"E7.0.12.34"),sQuery(id+"F0.wireOp",EDGE,"E7.0.12.36"),sQuery(id+"F0.wireOp",EDGE,"E7.0.12.37"),sQuery(id+"F0.wireOp",EDGE,"E7.0.12.38"),sQuery(id+"F0.wireOp",EDGE,"E7.0.12.40"),sQuery(id+"F0.wireOp",EDGE,"E7.0.12.41"),sQuery(id+"F0.wireOp",EDGE,"E7.0.12.42"),sQuery(id+"F0.wireOp",EDGE,"E7.0.12.43"),sQuery(id+"F0.wireOp",EDGE,"E7.0.13.0"),sQuery(id+"F0.wireOp",EDGE,"E7.0.13.1"),sQuery(id+"F0.wireOp",EDGE,"E7.0.13.2"),sQuery(id+"F0.wireOp",EDGE,"E7.0.13.3"),sQuery(id+"F0.wireOp",EDGE,"E7.0.13.4"),sQuery(id+"F0.wireOp",EDGE,"E7.0.13.5"),sQuery(id+"F0.wireOp",EDGE,"E7.0.13.10"),sQuery(id+"F0.wireOp",EDGE,"E7.0.13.12"),sQuery(id+"F0.wireOp",EDGE,"E7.0.13.13"),sQuery(id+"F0.wireOp",EDGE,"E7.0.13.14"),sQuery(id+"F0.wireOp",EDGE,"E7.0.13.15"),sQuery(id+"F0.wireOp",EDGE,"E7.0.13.18"),sQuery(id+"F0.wireOp",EDGE,"E7.0.13.21"),sQuery(id+"F0.wireOp",EDGE,"E7.0.13.22"),sQuery(id+"F0.wireOp",EDGE,"E7.0.13.26"),sQuery(id+"F0.wireOp",EDGE,"E7.0.13.27"),sQuery(id+"F0.wireOp",EDGE,"E7.0.13.28"),sQuery(id+"F0.wireOp",EDGE,"E7.0.13.32"),sQuery(id+"F0.wireOp",EDGE,"E7.0.13.34"),sQuery(id+"F0.wireOp",EDGE,"E7.0.13.36"),sQuery(id+"F0.wireOp",EDGE,"E7.0.13.37"),sQuery(id+"F0.wireOp",EDGE,"E7.0.13.40"),sQuery(id+"F0.wireOp",EDGE,"E7.0.13.41"),sQuery(id+"F0.wireOp",EDGE,"E7.0.13.42"),sQuery(id+"F0.wireOp",EDGE,"E7.0.13.43"),sQuery(id+"F0.wireOp",EDGE,"E7.0.14.0"),sQuery(id+"F0.wireOp",EDGE,"E7.0.14.1"),sQuery(id+"F0.wireOp",EDGE,"E7.0.14.2"),sQuery(id+"F0.wireOp",EDGE,"E7.0.14.3"),sQuery(id+"F0.wireOp",EDGE,"E7.0.14.4"),sQuery(id+"F0.wireOp",EDGE,"E7.0.14.5"),sQuery(id+"F0.wireOp",EDGE,"E7.0.14.10"),sQuery(id+"F0.wireOp",EDGE,"E7.0.14.13"),sQuery(id+"F0.wireOp",EDGE,"E7.0.14.14"),sQuery(id+"F0.wireOp",EDGE,"E7.0.14.15"),sQuery(id+"F0.wireOp",EDGE,"E7.0.14.21"),sQuery(id+"F0.wireOp",EDGE,"E7.0.14.22"),sQuery(id+"F0.wireOp",EDGE,"E7.0.14.26"),sQuery(id+"F0.wireOp",EDGE,"E7.0.14.27"),sQuery(id+"F0.wireOp",EDGE,"E7.0.14.32"),sQuery(id+"F0.wireOp",EDGE,"E7.0.14.34"),sQuery(id+"F0.wireOp",EDGE,"E7.0.14.36"),sQuery(id+"F0.wireOp",EDGE,"E7.0.14.37"),sQuery(id+"F0.wireOp",EDGE,"E7.0.14.41"),sQuery(id+"F0.wireOp",EDGE,"E7.0.14.42"),sQuery(id+"F0.wireOp",EDGE,"E7.0.14.43"),sQuery(id+"F0.wireOp",EDGE,"E7.0.15.0"),sQuery(id+"F0.wireOp",EDGE,"E7.0.15.1"),sQuery(id+"F0.wireOp",EDGE,"E7.0.15.2"),sQuery(id+"F0.wireOp",EDGE,"E7.0.15.4"),sQuery(id+"F0.wireOp",EDGE,"E7.0.15.5"),sQuery(id+"F0.wireOp",EDGE,"E7.0.15.10"),sQuery(id+"F0.wireOp",EDGE,"E7.0.15.13"),sQuery(id+"F0.wireOp",EDGE,"E7.0.15.15"),sQuery(id+"F0.wireOp",EDGE,"E7.0.15.21"),sQuery(id+"F0.wireOp",EDGE,"E7.0.15.26"),sQuery(id+"F0.wireOp",EDGE,"E7.0.15.27"),sQuery(id+"F0.wireOp",EDGE,"E7.0.15.32"),sQuery(id+"F0.wireOp",EDGE,"E7.0.15.34"),sQuery(id+"F0.wireOp",EDGE,"E7.0.15.37"),sQuery(id+"F0.wireOp",EDGE,"E7.0.15.41"),sQuery(id+"F0.wireOp",EDGE,"E7.0.15.42"),sQuery(id+"F0.wireOp",EDGE,"E7.0.15.43"),sQuery(id+"F0.wireOp",EDGE,"E7.0.16.1"),sQuery(id+"F0.wireOp",EDGE,"E7.0.16.2"),sQuery(id+"F0.wireOp",EDGE,"E7.0.16.4"),sQuery(id+"F0.wireOp",EDGE,"E7.0.16.5"),sQuery(id+"F0.wireOp",EDGE,"E7.0.16.10"),sQuery(id+"F0.wireOp",EDGE,"E7.0.16.15"),sQuery(id+"F0.wireOp",EDGE,"E7.0.16.21"),sQuery(id+"F0.wireOp",EDGE,"E7.0.16.26"),sQuery(id+"F0.wireOp",EDGE,"E7.0.16.32"),sQuery(id+"F0.wireOp",EDGE,"E7.0.16.37"),sQuery(id+"F0.wireOp",EDGE,"E7.0.16.41"),sQuery(id+"F0.wireOp",EDGE,"E7.0.16.42"),sQuery(id+"F0.wireOp",EDGE,"E7.0.16.43"),sQuery(id+"F0.wireOp",EDGE,"E7.0.17.41"),sQuery(id+"F0.wireOp",EDGE,"E7.0.17.42"),sQuery(id+"F0.wireOp",EDGE,"E7.0.17.43")])],"isStart":true});
            var sketch = newSketch(context, id + "F2", { "sketchPlane" : qUnion([Q0])});
            skCircle(sketch, "E8", {"center": v(0, 0) * mm, "radius": 158.75 * mm});
            skSolve(sketch);
        }
        {
            var Q0;
            Q0=makeQuery(id+"F2.imprint","IMPRINT",FACE,{"disambiguationData":[TD([[makeQuery(id+"F2.imprint","IMPRINT",EDGE,{"derivedFrom":sQuery(id+"F2.wireOp",EDGE,"E8")}),1.0]])]});
            extrude(context, id + "F3", {"entities" : qUnion([Q0]), "oppositeDirection" : true, "depth" : 25 * mm, "offsetDistance" : 25 * mm});
        }
    });
